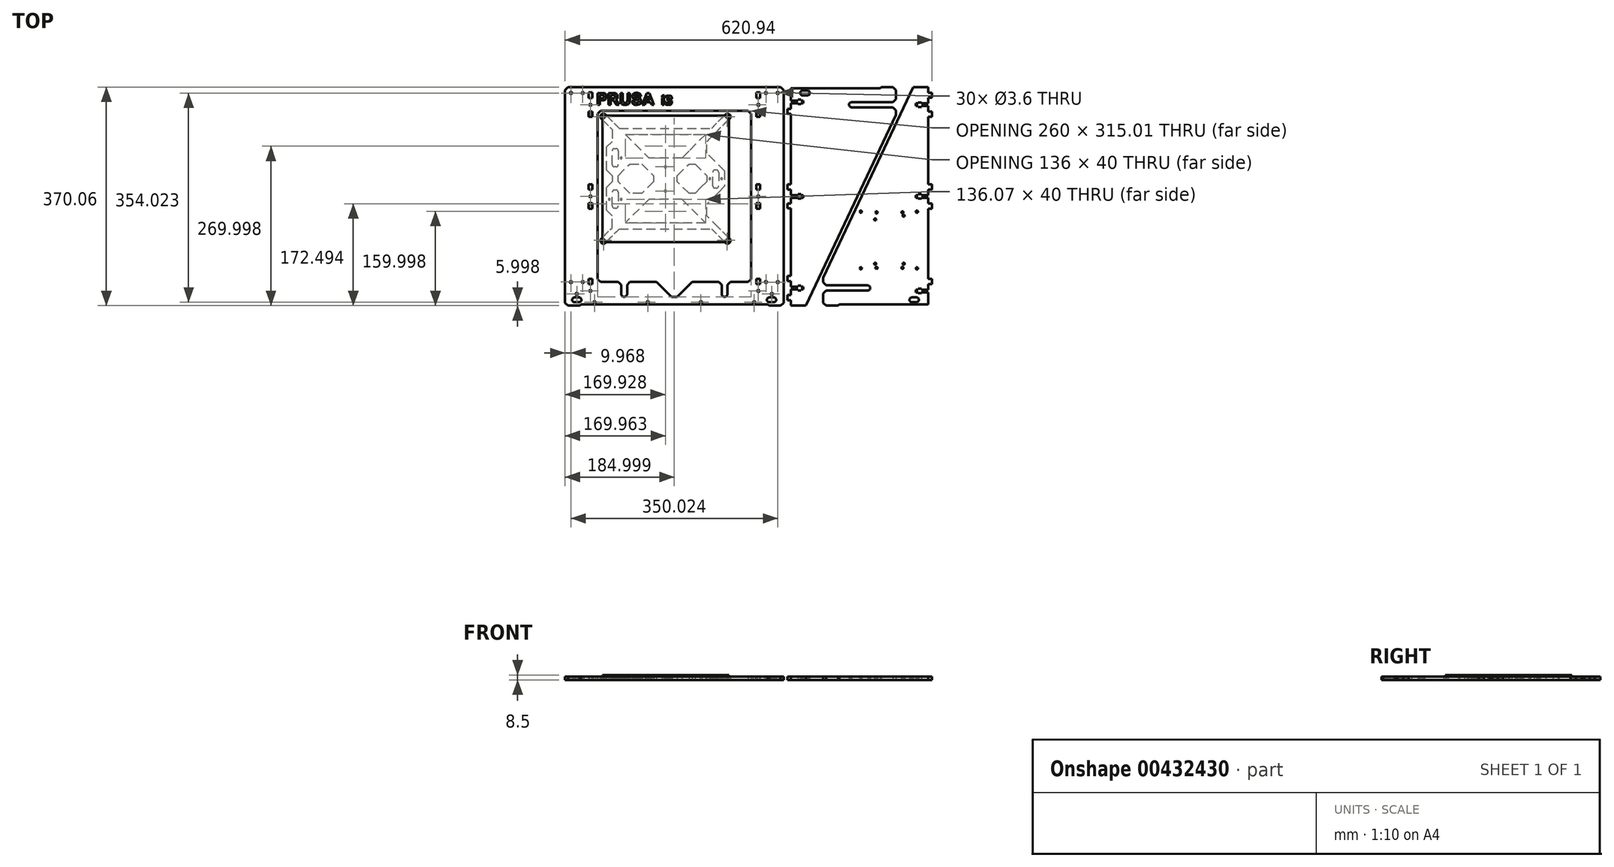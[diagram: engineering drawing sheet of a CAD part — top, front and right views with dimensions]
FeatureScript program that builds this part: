
annotation { "Feature Type Name" : "Feature", "Feature Type Description" : "" }
export const myFeature = defineFeature(function(context is Context, id is Id, definition is map)
    precondition{}
    {
        {
            var Q0;
            Q0=qCreatedBy(makeId("Top.planeOp"),FACE);
            var sketch = newSketch(context, id + "F0", { "sketchPlane" : qUnion([Q0])});
            skLineSegment(sketch, "E0", {"start": v(-112.47, -5.03) * mm, "end": v(-112.54, -5.03) * mm});
            skLineSegment(sketch, "E1", {"start": v(-72.47, -45.03) * mm, "end": v(-72.54, -45.03) * mm});
            skLineSegment(sketch, "E2", {"start": v(-168.47, -5.03) * mm, "end": v(-208.47, -45.03) * mm});
            skLineSegment(sketch, "E3", {"start": v(-112.47, -5.03) * mm, "end": v(-72.47, -45.03) * mm});
            skLineSegment(sketch, "E4", {"start": v(-112.54, -5.03) * mm, "end": v(-72.54, -45.03) * mm});
            skLineSegment(sketch, "E5", {"start": v(-168.54, -5.03) * mm, "end": v(-208.54, -45.03) * mm});
            skLineSegment(sketch, "E6", {"start": v(-208.47, -45.03) * mm, "end": v(-208.54, -45.03) * mm});
            skLineSegment(sketch, "E7", {"start": v(-168.47, -5.03) * mm, "end": v(-168.54, -5.03) * mm});
            skLineSegment(sketch, "E8", {"start": v(-305.47, -185.03) * mm, "end": v(-310.47, -180.22) * mm});
            skLineSegment(sketch, "E9", {"start": v(-310.47, 179.97) * mm, "end": v(-305.47, 184.97) * mm});
            skLineSegment(sketch, "E10", {"start": v(-305.47, 184.97) * mm, "end": v(54.53, 184.97) * mm});
            skLineSegment(sketch, "E11", {"start": v(54.53, 184.97) * mm, "end": v(59.53, 179.97) * mm});
            skLineSegment(sketch, "E12", {"start": v(59.53, -180.03) * mm, "end": v(54.53, -185.03) * mm});
            skLineSegment(sketch, "E13", {"start": v(34.53, -185.03) * mm, "end": v(32.53, -183.03) * mm});
            skLineSegment(sketch, "E14", {"start": v(32.53, -183.03) * mm, "end": v(-283.47, -183.03) * mm});
            skLineSegment(sketch, "E15", {"start": v(-283.47, -183.03) * mm, "end": v(-285.47, -185.03) * mm});
            skLineSegment(sketch, "E16", {"start": v(-230.47, -145.03) * mm, "end": v(-250.47, -145.03) * mm});
            skLineSegment(sketch, "E17", {"start": v(-250.47, -145.03) * mm, "end": v(-255.47, -140.03) * mm});
            skLineSegment(sketch, "E18", {"start": v(-255.47, -140.03) * mm, "end": v(-255.47, 139.97) * mm});
            skLineSegment(sketch, "E19", {"start": v(-255.47, 139.97) * mm, "end": v(-250.47, 144.97) * mm});
            skLineSegment(sketch, "E20", {"start": v(-250.47, 144.97) * mm, "end": v(-0.47, 144.97) * mm});
            skLineSegment(sketch, "E21", {"start": v(-0.47, 144.97) * mm, "end": v(4.53, 139.97) * mm});
            skLineSegment(sketch, "E22", {"start": v(4.53, 139.97) * mm, "end": v(4.53, -140.03) * mm});
            skLineSegment(sketch, "E23", {"start": v(4.53, -140.03) * mm, "end": v(-0.47, -145.03) * mm});
            skLineSegment(sketch, "E24", {"start": v(-0.47, -145.03) * mm, "end": v(-20.47, -145.03) * mm});
            skLineSegment(sketch, "E25", {"start": v(-130.47, -170.03) * mm, "end": v(-120.47, -170.03) * mm});
            skLineSegment(sketch, "E26", {"start": v(-120.47, -170.03) * mm, "end": v(-95.47, -145.03) * mm});
            skLineSegment(sketch, "E27", {"start": v(-130.47, -170.03) * mm, "end": v(-155.47, -145.03) * mm});
            skLineSegment(sketch, "E28", {"start": v(-200.47, -145.03) * mm, "end": v(-155.47, -145.03) * mm});
            skLineSegment(sketch, "E29", {"start": v(-95.47, -145.03) * mm, "end": v(-50.47, -145.03) * mm});
            skLineSegment(sketch, "E30", {"start": v(-80.47, 44.97) * mm, "end": v(-80.47, 44.9) * mm});
            skLineSegment(sketch, "E31", {"start": v(39.53, -179.03) * mm, "end": v(39.8, -179) * mm});
            skLineSegment(sketch, "E32", {"start": v(-310.47, -180.22) * mm, "end": v(-310.47, 179.97) * mm});
            skLineSegment(sketch, "E33", {"start": v(59.53, 179.97) * mm, "end": v(59.53, -180.03) * mm});
            skLineSegment(sketch, "E34", {"start": v(54.53, -185.03) * mm, "end": v(34.53, -185.03) * mm});
            skLineSegment(sketch, "E35", {"start": v(-285.47, -185.03) * mm, "end": v(-305.47, -185.03) * mm});
            skLineSegment(sketch, "E36", {"start": v(31.63, -173) * mm, "end": v(31.23, -173.96) * mm});
            skLineSegment(sketch, "E37", {"start": v(31.1, -175) * mm, "end": v(31.23, -176.03) * mm});
            skLineSegment(sketch, "E38", {"start": v(34.06, -171.13) * mm, "end": v(33.1, -171.53) * mm});
            skLineSegment(sketch, "E39", {"start": v(44.12, -171.13) * mm, "end": v(43.09, -171) * mm});
            skLineSegment(sketch, "E40", {"start": v(45.92, -177.82) * mm, "end": v(46.55, -177) * mm});
            skLineSegment(sketch, "E41", {"start": v(45.09, -178.46) * mm, "end": v(45.92, -177.82) * mm});
            skLineSegment(sketch, "E42", {"start": v(44.12, -178.86) * mm, "end": v(45.09, -178.46) * mm});
            skLineSegment(sketch, "E43", {"start": v(33.1, -178.46) * mm, "end": v(34.06, -178.86) * mm});
            skLineSegment(sketch, "E44", {"start": v(34.06, -178.86) * mm, "end": v(35.1, -179) * mm});
            skLineSegment(sketch, "E45", {"start": v(31.23, -176.03) * mm, "end": v(31.63, -177) * mm});
            skLineSegment(sketch, "E46", {"start": v(45.92, -172.17) * mm, "end": v(45.09, -171.53) * mm});
            skLineSegment(sketch, "E47", {"start": v(46.55, -173) * mm, "end": v(45.92, -172.17) * mm});
            skLineSegment(sketch, "E48", {"start": v(35.1, -171) * mm, "end": v(43.09, -171) * mm});
            skLineSegment(sketch, "E49", {"start": v(33.1, -171.53) * mm, "end": v(32.26, -172.17) * mm});
            skLineSegment(sketch, "E50", {"start": v(32.26, -172.17) * mm, "end": v(31.63, -173) * mm});
            skLineSegment(sketch, "E51", {"start": v(32.26, -177.82) * mm, "end": v(33.1, -178.46) * mm});
            skLineSegment(sketch, "E52", {"start": v(46.95, -173.96) * mm, "end": v(46.55, -173) * mm});
            skLineSegment(sketch, "E53", {"start": v(31.23, -173.96) * mm, "end": v(31.1, -175) * mm});
            skLineSegment(sketch, "E54", {"start": v(31.63, -177) * mm, "end": v(32.26, -177.82) * mm});
            skLineSegment(sketch, "E55", {"start": v(46.95, -176.03) * mm, "end": v(47.09, -175) * mm});
            skLineSegment(sketch, "E56", {"start": v(46.55, -177) * mm, "end": v(46.95, -176.03) * mm});
            skLineSegment(sketch, "E57", {"start": v(35.1, -171) * mm, "end": v(34.06, -171.13) * mm});
            skLineSegment(sketch, "E58", {"start": v(43.16, -179) * mm, "end": v(44.12, -178.86) * mm});
            skLineSegment(sketch, "E59", {"start": v(35.1, -179) * mm, "end": v(39.25, -179) * mm});
            skLineSegment(sketch, "E60", {"start": v(47.09, -175) * mm, "end": v(46.95, -173.96) * mm});
            skLineSegment(sketch, "E61", {"start": v(45.09, -171.53) * mm, "end": v(44.12, -171.13) * mm});
            skLineSegment(sketch, "E62", {"start": v(39.25, -179) * mm, "end": v(39.53, -179.03) * mm});
            skLineSegment(sketch, "E63", {"start": v(39.25, -179) * mm, "end": v(39.8, -179) * mm});
            skLineSegment(sketch, "E64", {"start": v(39.8, -179) * mm, "end": v(43.16, -179) * mm});
            skLineSegment(sketch, "E65", {"start": v(-298.44, -175) * mm, "end": v(-298.3, -176.03) * mm});
            skLineSegment(sketch, "E66", {"start": v(-297.9, -173) * mm, "end": v(-298.3, -173.96) * mm});
            skLineSegment(sketch, "E67", {"start": v(-295.48, -171.13) * mm, "end": v(-296.44, -171.53) * mm});
            skLineSegment(sketch, "E68", {"start": v(-285.41, -171.13) * mm, "end": v(-286.45, -171) * mm});
            skLineSegment(sketch, "E69", {"start": v(-283.62, -177.82) * mm, "end": v(-282.98, -177) * mm});
            skLineSegment(sketch, "E70", {"start": v(-284.45, -178.46) * mm, "end": v(-283.62, -177.82) * mm});
            skLineSegment(sketch, "E71", {"start": v(-285.41, -178.86) * mm, "end": v(-284.45, -178.46) * mm});
            skLineSegment(sketch, "E72", {"start": v(-296.44, -178.46) * mm, "end": v(-295.48, -178.86) * mm});
            skLineSegment(sketch, "E73", {"start": v(-295.48, -178.86) * mm, "end": v(-294.44, -179) * mm});
            skLineSegment(sketch, "E74", {"start": v(-298.3, -176.03) * mm, "end": v(-297.9, -177) * mm});
            skLineSegment(sketch, "E75", {"start": v(-283.62, -172.17) * mm, "end": v(-284.45, -171.53) * mm});
            skLineSegment(sketch, "E76", {"start": v(-282.98, -173) * mm, "end": v(-283.62, -172.17) * mm});
            skLineSegment(sketch, "E77", {"start": v(-294.44, -171) * mm, "end": v(-286.45, -171) * mm});
            skLineSegment(sketch, "E78", {"start": v(-296.44, -171.53) * mm, "end": v(-297.27, -172.17) * mm});
            skLineSegment(sketch, "E79", {"start": v(-297.27, -172.17) * mm, "end": v(-297.9, -173) * mm});
            skLineSegment(sketch, "E80", {"start": v(-297.27, -177.82) * mm, "end": v(-296.44, -178.46) * mm});
            skLineSegment(sketch, "E81", {"start": v(-282.59, -173.96) * mm, "end": v(-282.98, -173) * mm});
            skLineSegment(sketch, "E82", {"start": v(-298.3, -173.96) * mm, "end": v(-298.44, -175) * mm});
            skLineSegment(sketch, "E83", {"start": v(-297.9, -177) * mm, "end": v(-297.27, -177.82) * mm});
            skLineSegment(sketch, "E84", {"start": v(-282.59, -176.03) * mm, "end": v(-282.45, -175) * mm});
            skLineSegment(sketch, "E85", {"start": v(-282.98, -177) * mm, "end": v(-282.59, -176.03) * mm});
            skLineSegment(sketch, "E86", {"start": v(-294.44, -171) * mm, "end": v(-295.48, -171.13) * mm});
            skLineSegment(sketch, "E87", {"start": v(-286.38, -179) * mm, "end": v(-285.41, -178.86) * mm});
            skLineSegment(sketch, "E88", {"start": v(-294.44, -179) * mm, "end": v(-286.38, -179) * mm});
            skLineSegment(sketch, "E89", {"start": v(-282.45, -175) * mm, "end": v(-282.59, -173.96) * mm});
            skLineSegment(sketch, "E90", {"start": v(-284.45, -171.53) * mm, "end": v(-285.41, -171.13) * mm});
            skLineSegment(sketch, "E91", {"start": v(13.28, 166.71) * mm, "end": v(13.28, 175.71) * mm});
            skLineSegment(sketch, "E92", {"start": v(13.28, 175.71) * mm, "end": v(19.78, 175.71) * mm});
            skLineSegment(sketch, "E93", {"start": v(19.78, 175.71) * mm, "end": v(19.78, 166.71) * mm});
            skLineSegment(sketch, "E94", {"start": v(19.78, 166.71) * mm, "end": v(13.28, 166.71) * mm});
            skLineSegment(sketch, "E95", {"start": v(13.28, 134.41) * mm, "end": v(13.28, 143.41) * mm});
            skLineSegment(sketch, "E96", {"start": v(13.28, 143.41) * mm, "end": v(19.78, 143.41) * mm});
            skLineSegment(sketch, "E97", {"start": v(19.78, 143.41) * mm, "end": v(19.78, 134.41) * mm});
            skLineSegment(sketch, "E98", {"start": v(19.78, 134.41) * mm, "end": v(13.28, 134.41) * mm});
            skLineSegment(sketch, "E99", {"start": v(13.28, 11.62) * mm, "end": v(13.28, 20.62) * mm});
            skLineSegment(sketch, "E100", {"start": v(13.28, 20.62) * mm, "end": v(19.78, 20.62) * mm});
            skLineSegment(sketch, "E101", {"start": v(19.78, 20.62) * mm, "end": v(19.78, 11.62) * mm});
            skLineSegment(sketch, "E102", {"start": v(19.78, 11.62) * mm, "end": v(13.28, 11.62) * mm});
            skLineSegment(sketch, "E103", {"start": v(13.28, -20.68) * mm, "end": v(13.28, -11.68) * mm});
            skLineSegment(sketch, "E104", {"start": v(13.28, -11.68) * mm, "end": v(19.78, -11.68) * mm});
            skLineSegment(sketch, "E105", {"start": v(19.78, -11.68) * mm, "end": v(19.78, -20.68) * mm});
            skLineSegment(sketch, "E106", {"start": v(19.78, -20.68) * mm, "end": v(13.28, -20.68) * mm});
            skLineSegment(sketch, "E107", {"start": v(13.28, -148.38) * mm, "end": v(13.28, -139.38) * mm});
            skLineSegment(sketch, "E108", {"start": v(13.28, -139.38) * mm, "end": v(19.78, -139.38) * mm});
            skLineSegment(sketch, "E109", {"start": v(19.78, -139.38) * mm, "end": v(19.78, -148.38) * mm});
            skLineSegment(sketch, "E110", {"start": v(19.78, -148.38) * mm, "end": v(13.28, -148.38) * mm});
            skLineSegment(sketch, "E111", {"start": v(-270.72, 166.71) * mm, "end": v(-270.72, 175.71) * mm});
            skLineSegment(sketch, "E112", {"start": v(-270.72, 175.71) * mm, "end": v(-264.22, 175.71) * mm});
            skLineSegment(sketch, "E113", {"start": v(-264.22, 175.71) * mm, "end": v(-264.22, 166.71) * mm});
            skLineSegment(sketch, "E114", {"start": v(-264.22, 166.71) * mm, "end": v(-270.72, 166.71) * mm});
            skLineSegment(sketch, "E115", {"start": v(-270.72, 134.41) * mm, "end": v(-270.72, 143.41) * mm});
            skLineSegment(sketch, "E116", {"start": v(-270.72, 143.41) * mm, "end": v(-264.22, 143.41) * mm});
            skLineSegment(sketch, "E117", {"start": v(-264.22, 143.41) * mm, "end": v(-264.22, 134.41) * mm});
            skLineSegment(sketch, "E118", {"start": v(-264.22, 134.41) * mm, "end": v(-270.72, 134.41) * mm});
            skLineSegment(sketch, "E119", {"start": v(-270.72, 11.62) * mm, "end": v(-270.72, 20.62) * mm});
            skLineSegment(sketch, "E120", {"start": v(-270.72, 20.62) * mm, "end": v(-264.22, 20.62) * mm});
            skLineSegment(sketch, "E121", {"start": v(-264.22, 20.62) * mm, "end": v(-264.22, 11.62) * mm});
            skLineSegment(sketch, "E122", {"start": v(-264.22, 11.62) * mm, "end": v(-270.72, 11.62) * mm});
            skLineSegment(sketch, "E123", {"start": v(-270.72, -20.68) * mm, "end": v(-270.72, -11.68) * mm});
            skLineSegment(sketch, "E124", {"start": v(-270.72, -11.68) * mm, "end": v(-264.22, -11.68) * mm});
            skLineSegment(sketch, "E125", {"start": v(-264.22, -11.68) * mm, "end": v(-264.22, -20.68) * mm});
            skLineSegment(sketch, "E126", {"start": v(-264.22, -20.68) * mm, "end": v(-270.72, -20.68) * mm});
            skLineSegment(sketch, "E127", {"start": v(-270.72, -148.38) * mm, "end": v(-270.72, -139.38) * mm});
            skLineSegment(sketch, "E128", {"start": v(-270.72, -139.38) * mm, "end": v(-264.22, -139.38) * mm});
            skLineSegment(sketch, "E129", {"start": v(-264.22, -139.38) * mm, "end": v(-264.22, -148.38) * mm});
            skLineSegment(sketch, "E130", {"start": v(-264.22, -148.38) * mm, "end": v(-270.72, -148.38) * mm});
            skLineSegment(sketch, "E131", {"start": v(310.47, 134.51) * mm, "end": v(310.47, 143.31) * mm});
            skLineSegment(sketch, "E132", {"start": v(304.37, -148.28) * mm, "end": v(310.47, -148.28) * mm});
            skLineSegment(sketch, "E133", {"start": v(310.47, -148.28) * mm, "end": v(310.47, -139.48) * mm});
            skLineSegment(sketch, "E134", {"start": v(310.47, -139.48) * mm, "end": v(304.37, -139.48) * mm});
            skLineSegment(sketch, "E135", {"start": v(304.37, -139.48) * mm, "end": v(304.37, -20.58) * mm});
            skLineSegment(sketch, "E136", {"start": v(88.26, 177.03) * mm, "end": v(88.9, 177.86) * mm});
            skLineSegment(sketch, "E137", {"start": v(103.58, 176.07) * mm, "end": v(103.72, 175.03) * mm});
            skLineSegment(sketch, "E138", {"start": v(103.18, 177.03) * mm, "end": v(103.58, 176.07) * mm});
            skLineSegment(sketch, "E139", {"start": v(83.78, 2.23) * mm, "end": v(71.78, 2.23) * mm});
            skLineSegment(sketch, "E140", {"start": v(170.33, 156.17) * mm, "end": v(170.77, 157.23) * mm});
            skLineSegment(sketch, "E141", {"start": v(91.72, 171.03) * mm, "end": v(90.69, 171.17) * mm});
            skLineSegment(sketch, "E142", {"start": v(99.78, 179.03) * mm, "end": v(100.75, 178.9) * mm});
            skLineSegment(sketch, "E143", {"start": v(91.72, 179.03) * mm, "end": v(99.78, 179.03) * mm});
            skLineSegment(sketch, "E144", {"start": v(171.47, 151.92) * mm, "end": v(170.77, 152.83) * mm});
            skLineSegment(sketch, "E145", {"start": v(170.18, 155.03) * mm, "end": v(170.33, 156.17) * mm});
            skLineSegment(sketch, "E146", {"start": v(83.78, -3.97) * mm, "end": v(88.88, -3.97) * mm});
            skLineSegment(sketch, "E147", {"start": v(224.58, 185.03) * mm, "end": v(244.58, 185.03) * mm});
            skLineSegment(sketch, "E148", {"start": v(170.77, 157.23) * mm, "end": v(171.47, 158.14) * mm});
            skLineSegment(sketch, "E149", {"start": v(88.88, 162.24) * mm, "end": v(88.88, 164.04) * mm});
            skLineSegment(sketch, "E150", {"start": v(83.78, 162.24) * mm, "end": v(71.78, 162.24) * mm});
            skLineSegment(sketch, "E151", {"start": v(83.78, 164.04) * mm, "end": v(83.78, 162.24) * mm});
            skLineSegment(sketch, "E152", {"start": v(71.78, 157.84) * mm, "end": v(71.78, 148.28) * mm});
            skLineSegment(sketch, "E153", {"start": v(83.78, -151.05) * mm, "end": v(83.78, -152.85) * mm});
            skLineSegment(sketch, "E154", {"start": v(83.78, -157.25) * mm, "end": v(83.78, -159.05) * mm});
            skLineSegment(sketch, "E155", {"start": v(92.88, -157.25) * mm, "end": v(92.88, -152.85) * mm});
            skLineSegment(sketch, "E156", {"start": v(88.88, -157.25) * mm, "end": v(92.88, -157.25) * mm});
            skLineSegment(sketch, "E157", {"start": v(88.88, -157.25) * mm, "end": v(88.88, -159.05) * mm});
            skLineSegment(sketch, "E158", {"start": v(71.78, -157.25) * mm, "end": v(83.78, -157.25) * mm});
            skLineSegment(sketch, "E159", {"start": v(92.88, -152.85) * mm, "end": v(88.88, -152.85) * mm});
            skLineSegment(sketch, "E160", {"start": v(83.78, -152.85) * mm, "end": v(71.78, -152.85) * mm});
            skLineSegment(sketch, "E161", {"start": v(88.88, -151.05) * mm, "end": v(83.78, -151.05) * mm});
            skLineSegment(sketch, "E162", {"start": v(304.37, -183.03) * mm, "end": v(153.57, -183.03) * mm});
            skLineSegment(sketch, "E163", {"start": v(273.61, -172.2) * mm, "end": v(274.44, -171.57) * mm});
            skLineSegment(sketch, "E164", {"start": v(272.97, -173.03) * mm, "end": v(273.61, -172.2) * mm});
            skLineSegment(sketch, "E165", {"start": v(284.43, -171.03) * mm, "end": v(276.44, -171.03) * mm});
            skLineSegment(sketch, "E166", {"start": v(203.77, -151.22) * mm, "end": v(204.68, -151.92) * mm});
            skLineSegment(sketch, "E167", {"start": v(283.27, -2.23) * mm, "end": v(287.27, -2.23) * mm});
            skLineSegment(sketch, "E168", {"start": v(202.71, -150.78) * mm, "end": v(203.77, -151.22) * mm});
            skLineSegment(sketch, "E169", {"start": v(287.27, -4.03) * mm, "end": v(292.37, -4.03) * mm});
            skLineSegment(sketch, "E170", {"start": v(286.43, -171.57) * mm, "end": v(287.26, -172.2) * mm});
            skLineSegment(sketch, "E171", {"start": v(304.37, -157.84) * mm, "end": v(292.37, -157.84) * mm});
            skLineSegment(sketch, "E172", {"start": v(292.37, -157.84) * mm, "end": v(292.37, -156.04) * mm});
            skLineSegment(sketch, "E173", {"start": v(283.27, -162.24) * mm, "end": v(287.27, -162.24) * mm});
            skLineSegment(sketch, "E174", {"start": v(287.27, -164.04) * mm, "end": v(292.37, -164.04) * mm});
            skLineSegment(sketch, "E175", {"start": v(292.37, -156.04) * mm, "end": v(287.27, -156.04) * mm});
            skLineSegment(sketch, "E176", {"start": v(287.27, -162.24) * mm, "end": v(287.27, -164.04) * mm});
            skLineSegment(sketch, "E177", {"start": v(292.37, -162.24) * mm, "end": v(304.37, -162.24) * mm});
            skLineSegment(sketch, "E178", {"start": v(292.37, -164.04) * mm, "end": v(292.37, -162.24) * mm});
            skLineSegment(sketch, "E179", {"start": v(304.37, -157.84) * mm, "end": v(304.37, -148.28) * mm});
            skLineSegment(sketch, "E180", {"start": v(103.58, 174) * mm, "end": v(103.18, 173.03) * mm});
            skLineSegment(sketch, "E181", {"start": v(273.61, -177.86) * mm, "end": v(272.97, -177.03) * mm});
            skLineSegment(sketch, "E182", {"start": v(274.44, -178.5) * mm, "end": v(273.61, -177.86) * mm});
            skLineSegment(sketch, "E183", {"start": v(275.4, -178.9) * mm, "end": v(274.44, -178.5) * mm});
            skLineSegment(sketch, "E184", {"start": v(304.37, 2.17) * mm, "end": v(292.37, 2.17) * mm});
            skLineSegment(sketch, "E185", {"start": v(286.43, -178.5) * mm, "end": v(285.47, -178.9) * mm});
            skLineSegment(sketch, "E186", {"start": v(285.47, -178.9) * mm, "end": v(284.43, -179.03) * mm});
            skLineSegment(sketch, "E187", {"start": v(288.3, -176.07) * mm, "end": v(287.9, -177.03) * mm});
            skLineSegment(sketch, "E188", {"start": v(203.77, -158.84) * mm, "end": v(202.71, -159.28) * mm});
            skLineSegment(sketch, "E189", {"start": v(71.78, -175.61) * mm, "end": v(71.78, -184.97) * mm});
            skLineSegment(sketch, "E190", {"start": v(65.68, -143.31) * mm, "end": v(71.78, -143.31) * mm});
            skLineSegment(sketch, "E191", {"start": v(71.78, -134.51) * mm, "end": v(65.68, -134.51) * mm});
            skLineSegment(sketch, "E192", {"start": v(65.68, -134.51) * mm, "end": v(65.68, -143.31) * mm});
            skLineSegment(sketch, "E193", {"start": v(71.78, 148.28) * mm, "end": v(65.68, 148.28) * mm});
            skLineSegment(sketch, "E194", {"start": v(65.68, 148.28) * mm, "end": v(65.68, 139.48) * mm});
            skLineSegment(sketch, "E195", {"start": v(65.68, 139.48) * mm, "end": v(71.78, 139.48) * mm});
            skLineSegment(sketch, "E196", {"start": v(71.78, 139.48) * mm, "end": v(71.78, 20.58) * mm});
            skLineSegment(sketch, "E197", {"start": v(83.78, -2.17) * mm, "end": v(83.78, -3.97) * mm});
            skLineSegment(sketch, "E198", {"start": v(244.58, 185.03) * mm, "end": v(249.58, 180.03) * mm});
            skLineSegment(sketch, "E199", {"start": v(222.58, 183.03) * mm, "end": v(224.58, 185.03) * mm});
            skLineSegment(sketch, "E200", {"start": v(87.86, 174) * mm, "end": v(87.72, 175.03) * mm});
            skLineSegment(sketch, "E201", {"start": v(310.47, 20.52) * mm, "end": v(304.37, 20.52) * mm});
            skLineSegment(sketch, "E202", {"start": v(304.37, 20.52) * mm, "end": v(304.37, 134.51) * mm});
            skLineSegment(sketch, "E203", {"start": v(310.47, -11.78) * mm, "end": v(304.37, -11.78) * mm});
            skLineSegment(sketch, "E204", {"start": v(304.37, -20.58) * mm, "end": v(310.47, -20.58) * mm});
            skLineSegment(sketch, "E205", {"start": v(310.47, -20.58) * mm, "end": v(310.47, -11.78) * mm});
            skLineSegment(sketch, "E206", {"start": v(304.37, 11.72) * mm, "end": v(304.37, 2.17) * mm});
            skLineSegment(sketch, "E207", {"start": v(304.37, -2.23) * mm, "end": v(304.37, -11.78) * mm});
            skLineSegment(sketch, "E208", {"start": v(304.37, 166.81) * mm, "end": v(310.47, 166.81) * mm});
            skLineSegment(sketch, "E209", {"start": v(310.47, 166.81) * mm, "end": v(310.47, 175.61) * mm});
            skLineSegment(sketch, "E210", {"start": v(310.47, 175.61) * mm, "end": v(304.37, 175.61) * mm});
            skLineSegment(sketch, "E211", {"start": v(304.37, 175.61) * mm, "end": v(304.37, 184.97) * mm});
            skLineSegment(sketch, "E212", {"start": v(310.47, 143.31) * mm, "end": v(304.37, 143.31) * mm});
            skLineSegment(sketch, "E213", {"start": v(304.37, 134.51) * mm, "end": v(310.47, 134.51) * mm});
            skLineSegment(sketch, "E214", {"start": v(92.88, -2.17) * mm, "end": v(92.88, 2.23) * mm});
            skLineSegment(sketch, "E215", {"start": v(249.58, 138.03) * mm, "end": v(97.18, -184.97) * mm});
            skLineSegment(sketch, "E216", {"start": v(88.88, -2.17) * mm, "end": v(92.88, -2.17) * mm});
            skLineSegment(sketch, "E217", {"start": v(88.88, -2.17) * mm, "end": v(88.88, -3.97) * mm});
            skLineSegment(sketch, "E218", {"start": v(100.75, 171.17) * mm, "end": v(99.72, 171.03) * mm});
            skLineSegment(sketch, "E219", {"start": v(71.78, -184.97) * mm, "end": v(97.18, -184.97) * mm});
            skLineSegment(sketch, "E220", {"start": v(71.78, 2.23) * mm, "end": v(71.78, 11.78) * mm});
            skLineSegment(sketch, "E221", {"start": v(71.78, -166.81) * mm, "end": v(65.68, -166.81) * mm});
            skLineSegment(sketch, "E222", {"start": v(65.68, -166.81) * mm, "end": v(65.68, -175.61) * mm});
            skLineSegment(sketch, "E223", {"start": v(65.68, -175.61) * mm, "end": v(71.78, -175.61) * mm});
            skLineSegment(sketch, "E224", {"start": v(126.57, -180.03) * mm, "end": v(126.57, -164.43) * mm});
            skLineSegment(sketch, "E225", {"start": v(287.9, -173.03) * mm, "end": v(288.3, -174) * mm});
            skLineSegment(sketch, "E226", {"start": v(288.43, -175.03) * mm, "end": v(288.3, -176.07) * mm});
            skLineSegment(sketch, "E227", {"start": v(285.47, -171.17) * mm, "end": v(286.43, -171.57) * mm});
            skLineSegment(sketch, "E228", {"start": v(292.37, -4.03) * mm, "end": v(292.37, -2.23) * mm});
            skLineSegment(sketch, "E229", {"start": v(83.78, -159.05) * mm, "end": v(88.88, -159.05) * mm});
            skLineSegment(sketch, "E230", {"start": v(88.88, -152.85) * mm, "end": v(88.88, -151.05) * mm});
            skLineSegment(sketch, "E231", {"start": v(71.78, -157.25) * mm, "end": v(71.78, -166.81) * mm});
            skLineSegment(sketch, "E232", {"start": v(71.78, -152.85) * mm, "end": v(71.78, -143.31) * mm});
            skLineSegment(sketch, "E233", {"start": v(92.88, 157.84) * mm, "end": v(92.88, 162.24) * mm});
            skLineSegment(sketch, "E234", {"start": v(88.88, 157.84) * mm, "end": v(92.88, 157.84) * mm});
            skLineSegment(sketch, "E235", {"start": v(88.88, 157.84) * mm, "end": v(88.88, 156.04) * mm});
            skLineSegment(sketch, "E236", {"start": v(71.78, 157.84) * mm, "end": v(83.78, 157.84) * mm});
            skLineSegment(sketch, "E237", {"start": v(83.78, 157.84) * mm, "end": v(83.78, 156.04) * mm});
            skLineSegment(sketch, "E238", {"start": v(92.88, 162.24) * mm, "end": v(88.88, 162.24) * mm});
            skLineSegment(sketch, "E239", {"start": v(174.58, 150.63) * mm, "end": v(173.45, 150.78) * mm});
            skLineSegment(sketch, "E240", {"start": v(102.55, 177.86) * mm, "end": v(103.18, 177.03) * mm});
            skLineSegment(sketch, "E241", {"start": v(101.72, 178.5) * mm, "end": v(102.55, 177.86) * mm});
            skLineSegment(sketch, "E242", {"start": v(100.75, 178.9) * mm, "end": v(101.72, 178.5) * mm});
            skLineSegment(sketch, "E243", {"start": v(71.78, -2.17) * mm, "end": v(83.78, -2.17) * mm});
            skLineSegment(sketch, "E244", {"start": v(89.72, 178.5) * mm, "end": v(90.69, 178.9) * mm});
            skLineSegment(sketch, "E245", {"start": v(90.69, 178.9) * mm, "end": v(91.72, 179.03) * mm});
            skLineSegment(sketch, "E246", {"start": v(87.86, 176.07) * mm, "end": v(88.26, 177.03) * mm});
            skLineSegment(sketch, "E247", {"start": v(172.38, 158.84) * mm, "end": v(173.45, 159.28) * mm});
            skLineSegment(sketch, "E248", {"start": v(283.27, 2.17) * mm, "end": v(283.27, -2.23) * mm});
            skLineSegment(sketch, "E249", {"start": v(126.57, -138.03) * mm, "end": v(278.97, 184.97) * mm});
            skLineSegment(sketch, "E250", {"start": v(287.27, 2.17) * mm, "end": v(283.27, 2.17) * mm});
            skLineSegment(sketch, "E251", {"start": v(287.27, 2.17) * mm, "end": v(287.27, 3.97) * mm});
            skLineSegment(sketch, "E252", {"start": v(275.4, -171.17) * mm, "end": v(276.44, -171.03) * mm});
            skLineSegment(sketch, "E253", {"start": v(304.37, 184.97) * mm, "end": v(278.97, 184.97) * mm});
            skLineSegment(sketch, "E254", {"start": v(201.57, -150.63) * mm, "end": v(202.71, -150.78) * mm});
            skLineSegment(sketch, "E255", {"start": v(272.97, -177.03) * mm, "end": v(272.57, -176.07) * mm});
            skLineSegment(sketch, "E256", {"start": v(292.37, -2.23) * mm, "end": v(304.37, -2.23) * mm});
            skLineSegment(sketch, "E257", {"start": v(205.82, -156.17) * mm, "end": v(205.38, -157.23) * mm});
            skLineSegment(sketch, "E258", {"start": v(284.43, -171.03) * mm, "end": v(285.47, -171.17) * mm});
            skLineSegment(sketch, "E259", {"start": v(276.37, -179.03) * mm, "end": v(275.4, -178.9) * mm});
            skLineSegment(sketch, "E260", {"start": v(284.43, -179.03) * mm, "end": v(276.37, -179.03) * mm});
            skLineSegment(sketch, "E261", {"start": v(204.68, -151.92) * mm, "end": v(205.38, -152.83) * mm});
            skLineSegment(sketch, "E262", {"start": v(205.97, -155.03) * mm, "end": v(205.82, -156.17) * mm});
            skLineSegment(sketch, "E263", {"start": v(292.37, 3.97) * mm, "end": v(287.27, 3.97) * mm});
            skLineSegment(sketch, "E264", {"start": v(151.57, -185.03) * mm, "end": v(131.57, -185.03) * mm});
            skLineSegment(sketch, "E265", {"start": v(205.38, -157.23) * mm, "end": v(204.68, -158.14) * mm});
            skLineSegment(sketch, "E266", {"start": v(287.27, -2.23) * mm, "end": v(287.27, -4.03) * mm});
            skLineSegment(sketch, "E267", {"start": v(283.27, 157.25) * mm, "end": v(283.27, 152.85) * mm});
            skLineSegment(sketch, "E268", {"start": v(287.27, 157.25) * mm, "end": v(283.27, 157.25) * mm});
            skLineSegment(sketch, "E269", {"start": v(287.27, 157.25) * mm, "end": v(287.27, 159.05) * mm});
            skLineSegment(sketch, "E270", {"start": v(304.37, 157.25) * mm, "end": v(292.37, 157.25) * mm});
            skLineSegment(sketch, "E271", {"start": v(283.27, 152.85) * mm, "end": v(287.27, 152.85) * mm});
            skLineSegment(sketch, "E272", {"start": v(292.37, 152.85) * mm, "end": v(304.37, 152.85) * mm});
            skLineSegment(sketch, "E273", {"start": v(287.27, 151.05) * mm, "end": v(292.37, 151.05) * mm});
            skLineSegment(sketch, "E274", {"start": v(292.37, 159.05) * mm, "end": v(287.27, 159.05) * mm});
            skLineSegment(sketch, "E275", {"start": v(287.27, 152.85) * mm, "end": v(287.27, 151.05) * mm});
            skLineSegment(sketch, "E276", {"start": v(304.37, 157.25) * mm, "end": v(304.37, 166.81) * mm});
            skLineSegment(sketch, "E277", {"start": v(304.37, 152.85) * mm, "end": v(304.37, 143.31) * mm});
            skLineSegment(sketch, "E278", {"start": v(283.27, -157.84) * mm, "end": v(283.27, -162.24) * mm});
            skLineSegment(sketch, "E279", {"start": v(287.27, -157.84) * mm, "end": v(283.27, -157.84) * mm});
            skLineSegment(sketch, "E280", {"start": v(287.27, -157.84) * mm, "end": v(287.27, -156.04) * mm});
            skLineSegment(sketch, "E281", {"start": v(292.37, 151.05) * mm, "end": v(292.37, 152.85) * mm});
            skLineSegment(sketch, "E282", {"start": v(292.37, 157.25) * mm, "end": v(292.37, 159.05) * mm});
            skLineSegment(sketch, "E283", {"start": v(88.88, 2.23) * mm, "end": v(88.88, 4.03) * mm});
            skLineSegment(sketch, "E284", {"start": v(171.47, 158.14) * mm, "end": v(172.38, 158.84) * mm});
            skLineSegment(sketch, "E285", {"start": v(103.72, 175.03) * mm, "end": v(103.58, 174) * mm});
            skLineSegment(sketch, "E286", {"start": v(101.72, 171.57) * mm, "end": v(100.75, 171.17) * mm});
            skLineSegment(sketch, "E287", {"start": v(244.58, 159.43) * mm, "end": v(174.58, 159.43) * mm});
            skLineSegment(sketch, "E288", {"start": v(244.58, 159.43) * mm, "end": v(249.58, 164.43) * mm});
            skLineSegment(sketch, "E289", {"start": v(244.58, 150.63) * mm, "end": v(174.58, 150.63) * mm});
            skLineSegment(sketch, "E290", {"start": v(249.58, 145.63) * mm, "end": v(249.58, 138.03) * mm});
            skLineSegment(sketch, "E291", {"start": v(244.58, 150.63) * mm, "end": v(249.58, 145.63) * mm});
            skLineSegment(sketch, "E292", {"start": v(71.78, -11.72) * mm, "end": v(65.68, -11.72) * mm});
            skLineSegment(sketch, "E293", {"start": v(65.68, -11.72) * mm, "end": v(65.68, -20.52) * mm});
            skLineSegment(sketch, "E294", {"start": v(65.68, -20.52) * mm, "end": v(71.78, -20.52) * mm});
            skLineSegment(sketch, "E295", {"start": v(71.78, -20.52) * mm, "end": v(71.78, -134.51) * mm});
            skLineSegment(sketch, "E296", {"start": v(65.68, 11.78) * mm, "end": v(71.78, 11.78) * mm});
            skLineSegment(sketch, "E297", {"start": v(71.78, 20.58) * mm, "end": v(65.68, 20.58) * mm});
            skLineSegment(sketch, "E298", {"start": v(65.68, 20.58) * mm, "end": v(65.68, 11.78) * mm});
            skLineSegment(sketch, "E299", {"start": v(71.78, -11.72) * mm, "end": v(71.78, -2.17) * mm});
            skLineSegment(sketch, "E300", {"start": v(88.88, 164.04) * mm, "end": v(83.78, 164.04) * mm});
            skLineSegment(sketch, "E301", {"start": v(91.72, 171.03) * mm, "end": v(99.72, 171.03) * mm});
            skLineSegment(sketch, "E302", {"start": v(172.38, 151.22) * mm, "end": v(171.47, 151.92) * mm});
            skLineSegment(sketch, "E303", {"start": v(92.88, 2.23) * mm, "end": v(88.88, 2.23) * mm});
            skLineSegment(sketch, "E304", {"start": v(173.45, 150.78) * mm, "end": v(172.38, 151.22) * mm});
            skLineSegment(sketch, "E305", {"start": v(88.88, 4.03) * mm, "end": v(83.78, 4.03) * mm});
            skLineSegment(sketch, "E306", {"start": v(83.78, 156.04) * mm, "end": v(88.88, 156.04) * mm});
            skLineSegment(sketch, "E307", {"start": v(89.72, 171.57) * mm, "end": v(88.9, 172.2) * mm});
            skLineSegment(sketch, "E308", {"start": v(88.9, 172.2) * mm, "end": v(88.26, 173.03) * mm});
            skLineSegment(sketch, "E309", {"start": v(88.9, 177.86) * mm, "end": v(89.72, 178.5) * mm});
            skLineSegment(sketch, "E310", {"start": v(170.77, 152.83) * mm, "end": v(170.33, 153.9) * mm});
            skLineSegment(sketch, "E311", {"start": v(170.33, 153.9) * mm, "end": v(170.18, 155.03) * mm});
            skLineSegment(sketch, "E312", {"start": v(71.78, 183.03) * mm, "end": v(71.78, 162.24) * mm});
            skLineSegment(sketch, "E313", {"start": v(173.45, 159.28) * mm, "end": v(174.58, 159.43) * mm});
            skLineSegment(sketch, "E314", {"start": v(249.58, 180.03) * mm, "end": v(249.58, 164.43) * mm});
            skLineSegment(sketch, "E315", {"start": v(88.26, 173.03) * mm, "end": v(87.86, 174) * mm});
            skLineSegment(sketch, "E316", {"start": v(87.72, 175.03) * mm, "end": v(87.86, 176.07) * mm});
            skLineSegment(sketch, "E317", {"start": v(90.69, 171.17) * mm, "end": v(89.72, 171.57) * mm});
            skLineSegment(sketch, "E318", {"start": v(83.78, 4.03) * mm, "end": v(83.78, 2.23) * mm});
            skLineSegment(sketch, "E319", {"start": v(204.68, -158.14) * mm, "end": v(203.77, -158.84) * mm});
            skLineSegment(sketch, "E320", {"start": v(272.44, -175.03) * mm, "end": v(272.57, -174) * mm});
            skLineSegment(sketch, "E321", {"start": v(274.44, -171.57) * mm, "end": v(275.4, -171.17) * mm});
            skLineSegment(sketch, "E322", {"start": v(131.57, -159.43) * mm, "end": v(201.57, -159.43) * mm});
            skLineSegment(sketch, "E323", {"start": v(131.57, -159.43) * mm, "end": v(126.57, -164.43) * mm});
            skLineSegment(sketch, "E324", {"start": v(131.57, -150.63) * mm, "end": v(201.57, -150.63) * mm});
            skLineSegment(sketch, "E325", {"start": v(126.57, -145.63) * mm, "end": v(126.57, -138.03) * mm});
            skLineSegment(sketch, "E326", {"start": v(131.57, -150.63) * mm, "end": v(126.57, -145.63) * mm});
            skLineSegment(sketch, "E327", {"start": v(304.37, 11.72) * mm, "end": v(310.47, 11.72) * mm});
            skLineSegment(sketch, "E328", {"start": v(310.47, 11.72) * mm, "end": v(310.47, 20.52) * mm});
            skLineSegment(sketch, "E329", {"start": v(287.26, -172.2) * mm, "end": v(287.9, -173.03) * mm});
            skLineSegment(sketch, "E330", {"start": v(287.26, -177.86) * mm, "end": v(286.43, -178.5) * mm});
            skLineSegment(sketch, "E331", {"start": v(205.38, -152.83) * mm, "end": v(205.82, -153.9) * mm});
            skLineSegment(sketch, "E332", {"start": v(205.82, -153.9) * mm, "end": v(205.97, -155.03) * mm});
            skLineSegment(sketch, "E333", {"start": v(272.57, -174) * mm, "end": v(272.97, -173.03) * mm});
            skLineSegment(sketch, "E334", {"start": v(292.37, 2.17) * mm, "end": v(292.37, 3.97) * mm});
            skLineSegment(sketch, "E335", {"start": v(131.57, -185.03) * mm, "end": v(126.57, -180.03) * mm});
            skLineSegment(sketch, "E336", {"start": v(153.57, -183.03) * mm, "end": v(151.57, -185.03) * mm});
            skLineSegment(sketch, "E337", {"start": v(288.3, -174) * mm, "end": v(288.43, -175.03) * mm});
            skLineSegment(sketch, "E338", {"start": v(287.9, -177.03) * mm, "end": v(287.26, -177.86) * mm});
            skLineSegment(sketch, "E339", {"start": v(272.57, -176.07) * mm, "end": v(272.44, -175.03) * mm});
            skLineSegment(sketch, "E340", {"start": v(304.37, -183.03) * mm, "end": v(304.37, -162.24) * mm});
            skLineSegment(sketch, "E341", {"start": v(202.71, -159.28) * mm, "end": v(201.57, -159.43) * mm});
            skLineSegment(sketch, "E342", {"start": v(71.78, 183.03) * mm, "end": v(222.58, 183.03) * mm});
            skLineSegment(sketch, "E343", {"start": v(102.55, 172.2) * mm, "end": v(101.72, 171.57) * mm});
            skLineSegment(sketch, "E344", {"start": v(103.18, 173.03) * mm, "end": v(102.55, 172.2) * mm});
            skLineSegment(sketch, "E345", {"start": v(188.2, -26.36) * mm, "end": v(188.15, -25.9) * mm});
            skLineSegment(sketch, "E346", {"start": v(286.7, -121.34) * mm, "end": v(286.76, -121.8) * mm});
            skLineSegment(sketch, "E347", {"start": v(286.52, -120.9) * mm, "end": v(286.7, -121.34) * mm});
            skLineSegment(sketch, "E348", {"start": v(286.24, -120.54) * mm, "end": v(286.52, -120.9) * mm});
            skLineSegment(sketch, "E349", {"start": v(191.68, -26.36) * mm, "end": v(191.5, -26.8) * mm});
            skLineSegment(sketch, "E350", {"start": v(191.24, -123.04) * mm, "end": v(190.87, -123.33) * mm});
            skLineSegment(sketch, "E351", {"start": v(191.53, -122.67) * mm, "end": v(191.24, -123.04) * mm});
            skLineSegment(sketch, "E352", {"start": v(189.07, -123.32) * mm, "end": v(188.7, -123.04) * mm});
            skLineSegment(sketch, "E353", {"start": v(188.41, -122.67) * mm, "end": v(188.23, -122.23) * mm});
            skLineSegment(sketch, "E354", {"start": v(189.5, -120.03) * mm, "end": v(189.9, -119.98) * mm});
            skLineSegment(sketch, "E355", {"start": v(286.74, -25.85) * mm, "end": v(286.68, -26.32) * mm});
            skLineSegment(sketch, "E356", {"start": v(285.4, -27.6) * mm, "end": v(284.94, -27.65) * mm});
            skLineSegment(sketch, "E357", {"start": v(188.39, -25) * mm, "end": v(188.67, -24.63) * mm});
            skLineSegment(sketch, "E358", {"start": v(189.9, -27.7) * mm, "end": v(189.48, -27.64) * mm});
            skLineSegment(sketch, "E359", {"start": v(284.04, -27.41) * mm, "end": v(283.67, -27.13) * mm});
            skLineSegment(sketch, "E360", {"start": v(283.17, -121.84) * mm, "end": v(283.16, -121.8) * mm});
            skLineSegment(sketch, "E361", {"start": v(189.48, -24.16) * mm, "end": v(189.95, -24.1) * mm});
            skLineSegment(sketch, "E362", {"start": v(284.06, -123.37) * mm, "end": v(283.69, -123.08) * mm});
            skLineSegment(sketch, "E363", {"start": v(213.85, -37.27) * mm, "end": v(214.31, -37.2) * mm});
            skLineSegment(sketch, "E364", {"start": v(212.75, -38.1) * mm, "end": v(213.04, -37.74) * mm});
            skLineSegment(sketch, "E365", {"start": v(189.04, -27.46) * mm, "end": v(188.67, -27.17) * mm});
            skLineSegment(sketch, "E366", {"start": v(216.08, -114.42) * mm, "end": v(215.9, -114.85) * mm});
            skLineSegment(sketch, "E367", {"start": v(215.9, -114.85) * mm, "end": v(215.62, -115.23) * mm});
            skLineSegment(sketch, "E368", {"start": v(190.41, -24.16) * mm, "end": v(190.85, -24.34) * mm});
            skLineSegment(sketch, "E369", {"start": v(285.43, -120.07) * mm, "end": v(285.86, -120.25) * mm});
            skLineSegment(sketch, "E370", {"start": v(283.69, -120.54) * mm, "end": v(284.06, -120.25) * mm});
            skLineSegment(sketch, "E371", {"start": v(283.4, -120.9) * mm, "end": v(283.69, -120.54) * mm});
            skLineSegment(sketch, "E372", {"start": v(283.22, -121.34) * mm, "end": v(283.4, -120.9) * mm});
            skLineSegment(sketch, "E373", {"start": v(189.95, -24.1) * mm, "end": v(190.41, -24.16) * mm});
            skLineSegment(sketch, "E374", {"start": v(213.07, -115.23) * mm, "end": v(212.79, -114.85) * mm});
            skLineSegment(sketch, "E375", {"start": v(212.79, -114.85) * mm, "end": v(212.6, -114.42) * mm});
            skLineSegment(sketch, "E376", {"start": v(263.48, -34.27) * mm, "end": v(263.04, -34.45) * mm});
            skLineSegment(sketch, "E377", {"start": v(259.04, -108.12) * mm, "end": v(259.04, -110.32) * mm});
            skLineSegment(sketch, "E378", {"start": v(259.04, -110.32) * mm, "end": v(258.74, -110.32) * mm});
            skLineSegment(sketch, "E379", {"start": v(259.04, -110.32) * mm, "end": v(259.36, -110.32) * mm});
            skLineSegment(sketch, "E380", {"start": v(188.23, -122.23) * mm, "end": v(188.17, -121.77) * mm});
            skLineSegment(sketch, "E381", {"start": v(189.07, -120.2) * mm, "end": v(189.5, -120.03) * mm});
            skLineSegment(sketch, "E382", {"start": v(261.02, -33.6) * mm, "end": v(260.84, -33.17) * mm});
            skLineSegment(sketch, "E383", {"start": v(262.11, -30.97) * mm, "end": v(262.58, -30.9) * mm});
            skLineSegment(sketch, "E384", {"start": v(263.48, -31.15) * mm, "end": v(263.62, -31.26) * mm});
            skLineSegment(sketch, "E385", {"start": v(264.14, -31.8) * mm, "end": v(264.32, -32.24) * mm});
            skLineSegment(sketch, "E386", {"start": v(286.76, -121.8) * mm, "end": v(286.7, -122.28) * mm});
            skLineSegment(sketch, "E387", {"start": v(190.41, -27.64) * mm, "end": v(189.94, -27.7) * mm});
            skLineSegment(sketch, "E388", {"start": v(189.94, -27.7) * mm, "end": v(189.9, -27.7) * mm});
            skLineSegment(sketch, "E389", {"start": v(191.48, -31.81) * mm, "end": v(192.63, -31.81) * mm});
            skLineSegment(sketch, "E390", {"start": v(191.48, -31.81) * mm, "end": v(191.48, -30.71) * mm});
            skLineSegment(sketch, "E391", {"start": v(262.11, -34.45) * mm, "end": v(261.75, -34.3) * mm});
            skLineSegment(sketch, "E392", {"start": v(216.05, -38.54) * mm, "end": v(216.11, -39) * mm});
            skLineSegment(sketch, "E393", {"start": v(213.04, -37.74) * mm, "end": v(213.41, -37.45) * mm});
            skLineSegment(sketch, "E394", {"start": v(213.41, -37.45) * mm, "end": v(213.85, -37.27) * mm});
            skLineSegment(sketch, "E395", {"start": v(190.44, -120.03) * mm, "end": v(190.87, -120.2) * mm});
            skLineSegment(sketch, "E396", {"start": v(189.97, -119.97) * mm, "end": v(190.44, -120.03) * mm});
            skLineSegment(sketch, "E397", {"start": v(284.96, -120) * mm, "end": v(285.43, -120.07) * mm});
            skLineSegment(sketch, "E398", {"start": v(283.22, -122.28) * mm, "end": v(283.17, -121.84) * mm});
            skLineSegment(sketch, "E399", {"start": v(215.87, -39.9) * mm, "end": v(215.59, -40.28) * mm});
            skLineSegment(sketch, "E400", {"start": v(214.78, -40.75) * mm, "end": v(214.31, -40.8) * mm});
            skLineSegment(sketch, "E401", {"start": v(259.18, -36) * mm, "end": v(258.88, -36.3) * mm});
            skLineSegment(sketch, "E402", {"start": v(216.99, -42.2) * mm, "end": v(216.69, -42.51) * mm});
            skLineSegment(sketch, "E403", {"start": v(216.99, -44.4) * mm, "end": v(217.3, -44.4) * mm});
            skLineSegment(sketch, "E404", {"start": v(216.99, -44.4) * mm, "end": v(216.69, -44.4) * mm});
            skLineSegment(sketch, "E405", {"start": v(283.16, -121.8) * mm, "end": v(283.22, -121.34) * mm});
            skLineSegment(sketch, "E406", {"start": v(284.5, -123.55) * mm, "end": v(284.06, -123.37) * mm});
            skLineSegment(sketch, "E407", {"start": v(283.2, -25.39) * mm, "end": v(283.38, -24.95) * mm});
            skLineSegment(sketch, "E408", {"start": v(191.75, -25.9) * mm, "end": v(191.68, -26.36) * mm});
            skLineSegment(sketch, "E409", {"start": v(261.3, -31.44) * mm, "end": v(261.68, -31.15) * mm});
            skLineSegment(sketch, "E410", {"start": v(261.02, -31.8) * mm, "end": v(261.3, -31.44) * mm});
            skLineSegment(sketch, "E411", {"start": v(188.2, -25.43) * mm, "end": v(188.39, -25) * mm});
            skLineSegment(sketch, "E412", {"start": v(260.84, -33.17) * mm, "end": v(260.78, -32.7) * mm});
            skLineSegment(sketch, "E413", {"start": v(193.58, -116.54) * mm, "end": v(194.73, -116.54) * mm});
            skLineSegment(sketch, "E414", {"start": v(193.58, -117.64) * mm, "end": v(194.73, -117.64) * mm});
            skLineSegment(sketch, "E415", {"start": v(194.73, -115.44) * mm, "end": v(193.58, -115.44) * mm});
            skLineSegment(sketch, "E416", {"start": v(193.58, -117.64) * mm, "end": v(193.58, -116.54) * mm});
            skLineSegment(sketch, "E417", {"start": v(282.06, -116.37) * mm, "end": v(282.06, -115.27) * mm});
            skLineSegment(sketch, "E418", {"start": v(280.9, -116.37) * mm, "end": v(282.06, -116.37) * mm});
            skLineSegment(sketch, "E419", {"start": v(280.9, -117.47) * mm, "end": v(280.9, -116.37) * mm});
            skLineSegment(sketch, "E420", {"start": v(191.76, -121.84) * mm, "end": v(191.7, -122.23) * mm});
            skLineSegment(sketch, "E421", {"start": v(283.38, -26.75) * mm, "end": v(283.2, -26.32) * mm});
            skLineSegment(sketch, "E422", {"start": v(191.22, -27.17) * mm, "end": v(190.84, -27.46) * mm});
            skLineSegment(sketch, "E423", {"start": v(264.31, -33.17) * mm, "end": v(264.13, -33.6) * mm});
            skLineSegment(sketch, "E424", {"start": v(285.86, -123.37) * mm, "end": v(285.43, -123.55) * mm});
            skLineSegment(sketch, "E425", {"start": v(286.24, -123.08) * mm, "end": v(285.86, -123.37) * mm});
            skLineSegment(sketch, "E426", {"start": v(286.52, -122.7) * mm, "end": v(286.24, -123.08) * mm});
            skLineSegment(sketch, "E427", {"start": v(286.7, -122.28) * mm, "end": v(286.52, -122.7) * mm});
            skLineSegment(sketch, "E428", {"start": v(264.13, -33.6) * mm, "end": v(263.85, -33.98) * mm});
            skLineSegment(sketch, "E429", {"start": v(263.04, -34.45) * mm, "end": v(262.58, -34.5) * mm});
            skLineSegment(sketch, "E430", {"start": v(212.6, -114.42) * mm, "end": v(212.55, -113.95) * mm});
            skLineSegment(sketch, "E431", {"start": v(215.9, -113.05) * mm, "end": v(216.08, -113.49) * mm});
            skLineSegment(sketch, "E432", {"start": v(261.68, -31.15) * mm, "end": v(262.11, -30.97) * mm});
            skLineSegment(sketch, "E433", {"start": v(261.68, -34.27) * mm, "end": v(261.53, -34.13) * mm});
            skLineSegment(sketch, "E434", {"start": v(285.84, -27.41) * mm, "end": v(285.4, -27.6) * mm});
            skLineSegment(sketch, "E435", {"start": v(286.68, -26.32) * mm, "end": v(286.5, -26.75) * mm});
            skLineSegment(sketch, "E436", {"start": v(283.38, -24.95) * mm, "end": v(283.67, -24.58) * mm});
            skLineSegment(sketch, "E437", {"start": v(280.9, -117.47) * mm, "end": v(282.06, -117.47) * mm});
            skLineSegment(sketch, "E438", {"start": v(282.06, -115.27) * mm, "end": v(280.9, -115.27) * mm});
            skLineSegment(sketch, "E439", {"start": v(259.18, -38.2) * mm, "end": v(259.5, -38.2) * mm});
            skLineSegment(sketch, "E440", {"start": v(259.18, -38.2) * mm, "end": v(258.88, -38.2) * mm});
            skLineSegment(sketch, "E441", {"start": v(259.18, -36) * mm, "end": v(259.18, -38.2) * mm});
            skLineSegment(sketch, "E442", {"start": v(215.25, -112.4) * mm, "end": v(215.36, -112.48) * mm});
            skLineSegment(sketch, "E443", {"start": v(190.84, -27.46) * mm, "end": v(190.41, -27.64) * mm});
            skLineSegment(sketch, "E444", {"start": v(188.39, -26.8) * mm, "end": v(188.2, -26.36) * mm});
            skLineSegment(sketch, "E445", {"start": v(190.87, -120.2) * mm, "end": v(191.24, -120.5) * mm});
            skLineSegment(sketch, "E446", {"start": v(218.12, -110.06) * mm, "end": v(218.44, -110.06) * mm});
            skLineSegment(sketch, "E447", {"start": v(218.12, -107.86) * mm, "end": v(217.82, -108.17) * mm});
            skLineSegment(sketch, "E448", {"start": v(218.12, -110.06) * mm, "end": v(217.82, -110.06) * mm});
            skLineSegment(sketch, "E449", {"start": v(218.12, -107.86) * mm, "end": v(218.12, -110.06) * mm});
            skLineSegment(sketch, "E450", {"start": v(259.04, -108.12) * mm, "end": v(258.74, -108.43) * mm});
            skLineSegment(sketch, "E451", {"start": v(263.04, -30.97) * mm, "end": v(263.48, -31.15) * mm});
            skLineSegment(sketch, "E452", {"start": v(283.4, -122.7) * mm, "end": v(283.22, -122.28) * mm});
            skLineSegment(sketch, "E453", {"start": v(284.5, -120.07) * mm, "end": v(284.9, -120.02) * mm});
            skLineSegment(sketch, "E454", {"start": v(212.57, -39.47) * mm, "end": v(212.51, -39) * mm});
            skLineSegment(sketch, "E455", {"start": v(261.7, -112.47) * mm, "end": v(262.14, -112.29) * mm});
            skLineSegment(sketch, "E456", {"start": v(260.87, -114.5) * mm, "end": v(260.8, -114.02) * mm});
            skLineSegment(sketch, "E457", {"start": v(213.07, -112.68) * mm, "end": v(213.45, -112.4) * mm});
            skLineSegment(sketch, "E458", {"start": v(214.31, -40.8) * mm, "end": v(213.85, -40.75) * mm});
            skLineSegment(sketch, "E459", {"start": v(213.85, -40.75) * mm, "end": v(213.46, -40.59) * mm});
            skLineSegment(sketch, "E460", {"start": v(264.32, -32.24) * mm, "end": v(264.38, -32.7) * mm});
            skLineSegment(sketch, "E461", {"start": v(262.14, -115.76) * mm, "end": v(261.96, -115.67) * mm});
            skLineSegment(sketch, "E462", {"start": v(261.7, -115.58) * mm, "end": v(261.33, -115.3) * mm});
            skLineSegment(sketch, "E463", {"start": v(261.33, -115.3) * mm, "end": v(261.05, -114.92) * mm});
            skLineSegment(sketch, "E464", {"start": v(190.85, -24.34) * mm, "end": v(191.22, -24.63) * mm});
            skLineSegment(sketch, "E465", {"start": v(191.22, -24.63) * mm, "end": v(191.5, -25) * mm});
            skLineSegment(sketch, "E466", {"start": v(213.41, -40.57) * mm, "end": v(213.3, -40.47) * mm});
            skLineSegment(sketch, "E467", {"start": v(213.04, -40.28) * mm, "end": v(212.75, -39.9) * mm});
            skLineSegment(sketch, "E468", {"start": v(212.75, -39.9) * mm, "end": v(212.57, -39.47) * mm});
            skLineSegment(sketch, "E469", {"start": v(190.87, -123.33) * mm, "end": v(190.44, -123.5) * mm});
            skLineSegment(sketch, "E470", {"start": v(190.44, -123.5) * mm, "end": v(189.97, -123.57) * mm});
            skLineSegment(sketch, "E471", {"start": v(189.97, -123.57) * mm, "end": v(189.5, -123.5) * mm});
            skLineSegment(sketch, "E472", {"start": v(284.06, -120.25) * mm, "end": v(284.5, -120.07) * mm});
            skLineSegment(sketch, "E473", {"start": v(188.17, -121.77) * mm, "end": v(188.23, -121.3) * mm});
            skLineSegment(sketch, "E474", {"start": v(189.5, -123.5) * mm, "end": v(189.07, -123.32) * mm});
            skLineSegment(sketch, "E475", {"start": v(189.9, -119.98) * mm, "end": v(189.97, -119.97) * mm});
            skLineSegment(sketch, "E476", {"start": v(284.96, -123.6) * mm, "end": v(284.5, -123.55) * mm});
            skLineSegment(sketch, "E477", {"start": v(188.15, -25.9) * mm, "end": v(188.2, -25.43) * mm});
            skLineSegment(sketch, "E478", {"start": v(285.43, -123.55) * mm, "end": v(284.96, -123.6) * mm});
            skLineSegment(sketch, "E479", {"start": v(188.7, -120.5) * mm, "end": v(189.07, -120.2) * mm});
            skLineSegment(sketch, "E480", {"start": v(188.41, -120.87) * mm, "end": v(188.7, -120.5) * mm});
            skLineSegment(sketch, "E481", {"start": v(188.23, -121.3) * mm, "end": v(188.41, -120.87) * mm});
            skLineSegment(sketch, "E482", {"start": v(213.88, -112.21) * mm, "end": v(214.35, -112.15) * mm});
            skLineSegment(sketch, "E483", {"start": v(214.35, -112.15) * mm, "end": v(214.81, -112.21) * mm});
            skLineSegment(sketch, "E484", {"start": v(213.45, -112.4) * mm, "end": v(213.88, -112.21) * mm});
            skLineSegment(sketch, "E485", {"start": v(212.79, -113.05) * mm, "end": v(213.07, -112.68) * mm});
            skLineSegment(sketch, "E486", {"start": v(284.47, -24.11) * mm, "end": v(284.94, -24.05) * mm});
            skLineSegment(sketch, "E487", {"start": v(215.87, -38.1) * mm, "end": v(216.05, -38.54) * mm});
            skLineSegment(sketch, "E488", {"start": v(216.05, -39.48) * mm, "end": v(215.87, -39.9) * mm});
            skLineSegment(sketch, "E489", {"start": v(214.81, -115.7) * mm, "end": v(214.35, -115.75) * mm});
            skLineSegment(sketch, "E490", {"start": v(214.35, -115.75) * mm, "end": v(213.88, -115.7) * mm});
            skLineSegment(sketch, "E491", {"start": v(212.57, -38.54) * mm, "end": v(212.75, -38.1) * mm});
            skLineSegment(sketch, "E492", {"start": v(212.51, -39) * mm, "end": v(212.57, -38.54) * mm});
            skLineSegment(sketch, "E493", {"start": v(280.79, -32.1) * mm, "end": v(280.79, -31) * mm});
            skLineSegment(sketch, "E494", {"start": v(280.79, -31) * mm, "end": v(281.94, -31) * mm});
            skLineSegment(sketch, "E495", {"start": v(281.94, -29.9) * mm, "end": v(280.79, -29.9) * mm});
            skLineSegment(sketch, "E496", {"start": v(280.79, -32.1) * mm, "end": v(281.94, -32.1) * mm});
            skLineSegment(sketch, "E497", {"start": v(194.73, -116.54) * mm, "end": v(194.73, -115.44) * mm});
            skLineSegment(sketch, "E498", {"start": v(189.05, -24.34) * mm, "end": v(189.48, -24.16) * mm});
            skLineSegment(sketch, "E499", {"start": v(262.6, -112.22) * mm, "end": v(263.07, -112.29) * mm});
            skLineSegment(sketch, "E500", {"start": v(263.07, -112.29) * mm, "end": v(263.27, -112.37) * mm});
            skLineSegment(sketch, "E501", {"start": v(263.5, -112.47) * mm, "end": v(263.88, -112.75) * mm});
            skLineSegment(sketch, "E502", {"start": v(263.88, -112.75) * mm, "end": v(264.17, -113.13) * mm});
            skLineSegment(sketch, "E503", {"start": v(264.38, -32.7) * mm, "end": v(264.31, -33.17) * mm});
            skLineSegment(sketch, "E504", {"start": v(264.34, -114.5) * mm, "end": v(264.16, -114.93) * mm});
            skLineSegment(sketch, "E505", {"start": v(264.16, -114.93) * mm, "end": v(263.88, -115.3) * mm});
            skLineSegment(sketch, "E506", {"start": v(263.88, -115.3) * mm, "end": v(263.5, -115.58) * mm});
            skLineSegment(sketch, "E507", {"start": v(262.14, -112.29) * mm, "end": v(262.6, -112.22) * mm});
            skLineSegment(sketch, "E508", {"start": v(263.85, -33.98) * mm, "end": v(263.48, -34.27) * mm});
            skLineSegment(sketch, "E509", {"start": v(212.6, -113.49) * mm, "end": v(212.79, -113.05) * mm});
            skLineSegment(sketch, "E510", {"start": v(212.55, -113.95) * mm, "end": v(212.6, -113.49) * mm});
            skLineSegment(sketch, "E511", {"start": v(262.58, -30.9) * mm, "end": v(263.04, -30.97) * mm});
            skLineSegment(sketch, "E512", {"start": v(283.14, -25.85) * mm, "end": v(283.2, -25.39) * mm});
            skLineSegment(sketch, "E513", {"start": v(285.84, -24.3) * mm, "end": v(286.21, -24.58) * mm});
            skLineSegment(sketch, "E514", {"start": v(284.04, -24.3) * mm, "end": v(284.47, -24.11) * mm});
            skLineSegment(sketch, "E515", {"start": v(284.9, -120.02) * mm, "end": v(284.96, -120) * mm});
            skLineSegment(sketch, "E516", {"start": v(188.67, -27.17) * mm, "end": v(188.39, -26.8) * mm});
            skLineSegment(sketch, "E517", {"start": v(188.7, -123.04) * mm, "end": v(188.41, -122.67) * mm});
            skLineSegment(sketch, "E518", {"start": v(263.5, -115.58) * mm, "end": v(263.07, -115.76) * mm});
            skLineSegment(sketch, "E519", {"start": v(263.07, -115.76) * mm, "end": v(262.6, -115.82) * mm});
            skLineSegment(sketch, "E520", {"start": v(262.6, -115.82) * mm, "end": v(262.2, -115.77) * mm});
            skLineSegment(sketch, "E521", {"start": v(215.62, -115.23) * mm, "end": v(215.25, -115.51) * mm});
            skLineSegment(sketch, "E522", {"start": v(215.25, -115.51) * mm, "end": v(214.81, -115.7) * mm});
            skLineSegment(sketch, "E523", {"start": v(191.5, -26.8) * mm, "end": v(191.22, -27.17) * mm});
            skLineSegment(sketch, "E524", {"start": v(284.9, -27.65) * mm, "end": v(284.47, -27.6) * mm});
            skLineSegment(sketch, "E525", {"start": v(189.48, -27.64) * mm, "end": v(189.04, -27.46) * mm});
            skLineSegment(sketch, "E526", {"start": v(285.86, -120.25) * mm, "end": v(286.24, -120.54) * mm});
            skLineSegment(sketch, "E527", {"start": v(285.4, -24.11) * mm, "end": v(285.84, -24.3) * mm});
            skLineSegment(sketch, "E528", {"start": v(286.5, -24.95) * mm, "end": v(286.68, -25.39) * mm});
            skLineSegment(sketch, "E529", {"start": v(191.7, -122.23) * mm, "end": v(191.53, -122.67) * mm});
            skLineSegment(sketch, "E530", {"start": v(191.77, -121.77) * mm, "end": v(191.76, -121.84) * mm});
            skLineSegment(sketch, "E531", {"start": v(213.88, -115.7) * mm, "end": v(213.52, -115.54) * mm});
            skLineSegment(sketch, "E532", {"start": v(213.45, -115.51) * mm, "end": v(213.26, -115.34) * mm});
            skLineSegment(sketch, "E533", {"start": v(214.31, -37.2) * mm, "end": v(214.78, -37.27) * mm});
            skLineSegment(sketch, "E534", {"start": v(214.78, -37.27) * mm, "end": v(215.21, -37.45) * mm});
            skLineSegment(sketch, "E535", {"start": v(215.21, -37.45) * mm, "end": v(215.43, -37.62) * mm});
            skLineSegment(sketch, "E536", {"start": v(284.94, -24.05) * mm, "end": v(285.4, -24.11) * mm});
            skLineSegment(sketch, "E537", {"start": v(283.2, -26.32) * mm, "end": v(283.14, -25.85) * mm});
            skLineSegment(sketch, "E538", {"start": v(283.67, -24.58) * mm, "end": v(284.04, -24.3) * mm});
            skLineSegment(sketch, "E539", {"start": v(216.08, -113.49) * mm, "end": v(216.15, -113.95) * mm});
            skLineSegment(sketch, "E540", {"start": v(216.15, -113.95) * mm, "end": v(216.08, -114.42) * mm});
            skLineSegment(sketch, "E541", {"start": v(192.63, -29.61) * mm, "end": v(191.48, -29.61) * mm});
            skLineSegment(sketch, "E542", {"start": v(191.48, -30.71) * mm, "end": v(192.63, -30.71) * mm});
            skLineSegment(sketch, "E543", {"start": v(192.63, -30.71) * mm, "end": v(192.63, -29.61) * mm});
            skLineSegment(sketch, "E544", {"start": v(281.94, -31) * mm, "end": v(281.94, -29.9) * mm});
            skLineSegment(sketch, "E545", {"start": v(260.8, -114.02) * mm, "end": v(260.87, -113.56) * mm});
            skLineSegment(sketch, "E546", {"start": v(260.87, -113.56) * mm, "end": v(261.05, -113.12) * mm});
            skLineSegment(sketch, "E547", {"start": v(261.05, -113.12) * mm, "end": v(261.33, -112.75) * mm});
            skLineSegment(sketch, "E548", {"start": v(261.33, -112.75) * mm, "end": v(261.7, -112.47) * mm});
            skLineSegment(sketch, "E549", {"start": v(191.7, -121.3) * mm, "end": v(191.77, -121.77) * mm});
            skLineSegment(sketch, "E550", {"start": v(191.53, -120.87) * mm, "end": v(191.7, -121.3) * mm});
            skLineSegment(sketch, "E551", {"start": v(191.24, -120.5) * mm, "end": v(191.53, -120.87) * mm});
            skLineSegment(sketch, "E552", {"start": v(283.69, -123.08) * mm, "end": v(283.4, -122.7) * mm});
            skLineSegment(sketch, "E553", {"start": v(188.67, -24.63) * mm, "end": v(189.05, -24.34) * mm});
            skLineSegment(sketch, "E554", {"start": v(191.5, -25) * mm, "end": v(191.68, -25.43) * mm});
            skLineSegment(sketch, "E555", {"start": v(191.68, -25.43) * mm, "end": v(191.74, -25.84) * mm});
            skLineSegment(sketch, "E556", {"start": v(191.74, -25.84) * mm, "end": v(191.75, -25.9) * mm});
            skLineSegment(sketch, "E557", {"start": v(286.21, -24.58) * mm, "end": v(286.5, -24.95) * mm});
            skLineSegment(sketch, "E558", {"start": v(286.21, -27.13) * mm, "end": v(285.84, -27.41) * mm});
            skLineSegment(sketch, "E559", {"start": v(286.5, -26.75) * mm, "end": v(286.21, -27.13) * mm});
            skLineSegment(sketch, "E560", {"start": v(215.21, -40.57) * mm, "end": v(214.78, -40.75) * mm});
            skLineSegment(sketch, "E561", {"start": v(215.59, -37.74) * mm, "end": v(215.87, -38.1) * mm});
            skLineSegment(sketch, "E562", {"start": v(260.84, -32.24) * mm, "end": v(261.02, -31.8) * mm});
            skLineSegment(sketch, "E563", {"start": v(260.78, -32.7) * mm, "end": v(260.84, -32.24) * mm});
            skLineSegment(sketch, "E564", {"start": v(261.05, -114.92) * mm, "end": v(260.87, -114.5) * mm});
            skLineSegment(sketch, "E565", {"start": v(264.17, -113.13) * mm, "end": v(264.34, -113.56) * mm});
            skLineSegment(sketch, "E566", {"start": v(264.34, -113.56) * mm, "end": v(264.4, -114.03) * mm});
            skLineSegment(sketch, "E567", {"start": v(264.4, -114.03) * mm, "end": v(264.34, -114.5) * mm});
            skLineSegment(sketch, "E568", {"start": v(263.85, -31.44) * mm, "end": v(264.14, -31.8) * mm});
            skLineSegment(sketch, "E569", {"start": v(261.3, -33.98) * mm, "end": v(261.02, -33.6) * mm});
            skLineSegment(sketch, "E570", {"start": v(262.58, -34.5) * mm, "end": v(262.11, -34.45) * mm});
            skLineSegment(sketch, "E571", {"start": v(216.11, -39) * mm, "end": v(216.05, -39.48) * mm});
            skLineSegment(sketch, "E572", {"start": v(215.59, -40.28) * mm, "end": v(215.21, -40.57) * mm});
            skLineSegment(sketch, "E573", {"start": v(283.67, -27.13) * mm, "end": v(283.38, -26.75) * mm});
            skLineSegment(sketch, "E574", {"start": v(284.94, -27.65) * mm, "end": v(284.9, -27.65) * mm});
            skLineSegment(sketch, "E575", {"start": v(284.47, -27.6) * mm, "end": v(284.04, -27.41) * mm});
            skLineSegment(sketch, "E576", {"start": v(286.68, -25.39) * mm, "end": v(286.74, -25.85) * mm});
            skLineSegment(sketch, "E577", {"start": v(214.81, -112.21) * mm, "end": v(215.25, -112.4) * mm});
            skLineSegment(sketch, "E578", {"start": v(215.62, -112.68) * mm, "end": v(215.9, -113.05) * mm});
            skLineSegment(sketch, "E579", {"start": v(263.62, -31.26) * mm, "end": v(263.7, -31.3) * mm});
            skLineSegment(sketch, "E580", {"start": v(261.75, -34.3) * mm, "end": v(261.68, -34.27) * mm});
            skLineSegment(sketch, "E581", {"start": v(261.53, -34.13) * mm, "end": v(261.3, -33.98) * mm});
            skLineSegment(sketch, "E582", {"start": v(215.43, -112.51) * mm, "end": v(215.62, -112.68) * mm});
            skLineSegment(sketch, "E583", {"start": v(215.36, -112.48) * mm, "end": v(215.43, -112.51) * mm});
            skLineSegment(sketch, "E584", {"start": v(213.46, -40.59) * mm, "end": v(213.41, -40.57) * mm});
            skLineSegment(sketch, "E585", {"start": v(261.96, -115.67) * mm, "end": v(261.7, -115.58) * mm});
            skLineSegment(sketch, "E586", {"start": v(213.3, -40.47) * mm, "end": v(213.04, -40.28) * mm});
            skLineSegment(sketch, "E587", {"start": v(263.33, -112.38) * mm, "end": v(263.5, -112.47) * mm});
            skLineSegment(sketch, "E588", {"start": v(263.27, -112.37) * mm, "end": v(263.33, -112.38) * mm});
            skLineSegment(sketch, "E589", {"start": v(262.2, -115.77) * mm, "end": v(262.14, -115.76) * mm});
            skLineSegment(sketch, "E590", {"start": v(213.52, -115.54) * mm, "end": v(213.45, -115.51) * mm});
            skLineSegment(sketch, "E591", {"start": v(213.26, -115.34) * mm, "end": v(213.07, -115.23) * mm});
            skLineSegment(sketch, "E592", {"start": v(215.48, -37.63) * mm, "end": v(215.59, -37.74) * mm});
            skLineSegment(sketch, "E593", {"start": v(215.43, -37.62) * mm, "end": v(215.48, -37.63) * mm});
            skLineSegment(sketch, "E594", {"start": v(263.7, -31.3) * mm, "end": v(263.85, -31.44) * mm});
            skLineSegment(sketch, "E595", {"start": v(-142.74, 154.97) * mm, "end": v(-146.26, 154.97) * mm});
            skLineSegment(sketch, "E596", {"start": v(-146.26, 154.97) * mm, "end": v(-146.26, 166.26) * mm});
            skLineSegment(sketch, "E597", {"start": v(-146.26, 166.26) * mm, "end": v(-142.74, 166.26) * mm});
            skLineSegment(sketch, "E598", {"start": v(-142.74, 166.26) * mm, "end": v(-142.74, 154.97) * mm});
            skLineSegment(sketch, "E599", {"start": v(-142.63, 167.87) * mm, "end": v(-146.36, 167.87) * mm});
            skLineSegment(sketch, "E600", {"start": v(-146.36, 167.87) * mm, "end": v(-146.36, 170.62) * mm});
            skLineSegment(sketch, "E601", {"start": v(-146.36, 170.62) * mm, "end": v(-142.63, 170.62) * mm});
            skLineSegment(sketch, "E602", {"start": v(-142.63, 170.62) * mm, "end": v(-142.63, 167.87) * mm});
            skLineSegment(sketch, "E603", {"start": v(-129.24, 159.82) * mm, "end": v(-129.34, 158.77) * mm});
            skLineSegment(sketch, "E604", {"start": v(-129.34, 158.77) * mm, "end": v(-129.64, 157.81) * mm});
            skLineSegment(sketch, "E605", {"start": v(-129.64, 157.81) * mm, "end": v(-130.15, 156.98) * mm});
            skLineSegment(sketch, "E606", {"start": v(-130.15, 156.98) * mm, "end": v(-130.84, 156.28) * mm});
            skLineSegment(sketch, "E607", {"start": v(-130.84, 156.28) * mm, "end": v(-131.7, 155.72) * mm});
            skLineSegment(sketch, "E608", {"start": v(-131.7, 155.72) * mm, "end": v(-132.7, 155.3) * mm});
            skLineSegment(sketch, "E609", {"start": v(-132.7, 155.3) * mm, "end": v(-133.9, 155.05) * mm});
            skLineSegment(sketch, "E610", {"start": v(-133.9, 155.05) * mm, "end": v(-135.31, 154.97) * mm});
            skLineSegment(sketch, "E611", {"start": v(-135.31, 154.97) * mm, "end": v(-136.94, 155.04) * mm});
            skLineSegment(sketch, "E612", {"start": v(-136.94, 155.04) * mm, "end": v(-138.31, 155.26) * mm});
            skLineSegment(sketch, "E613", {"start": v(-138.31, 155.26) * mm, "end": v(-140.35, 155.91) * mm});
            skLineSegment(sketch, "E614", {"start": v(-140.35, 155.91) * mm, "end": v(-140.35, 159.16) * mm});
            skLineSegment(sketch, "E615", {"start": v(-140.35, 159.16) * mm, "end": v(-139.99, 159.16) * mm});
            skLineSegment(sketch, "E616", {"start": v(-139.99, 159.16) * mm, "end": v(-139.1, 158.67) * mm});
            skLineSegment(sketch, "E617", {"start": v(-139.1, 158.67) * mm, "end": v(-138.05, 158.26) * mm});
            skLineSegment(sketch, "E618", {"start": v(-138.05, 158.26) * mm, "end": v(-137, 157.97) * mm});
            skLineSegment(sketch, "E619", {"start": v(-137, 157.97) * mm, "end": v(-136.03, 157.87) * mm});
            skLineSegment(sketch, "E620", {"start": v(-136.03, 157.87) * mm, "end": v(-134.84, 157.97) * mm});
            skLineSegment(sketch, "E621", {"start": v(-134.84, 157.97) * mm, "end": v(-134.26, 158.12) * mm});
            skLineSegment(sketch, "E622", {"start": v(-134.26, 158.12) * mm, "end": v(-133.77, 158.39) * mm});
            skLineSegment(sketch, "E623", {"start": v(-133.77, 158.39) * mm, "end": v(-133.23, 159) * mm});
            skLineSegment(sketch, "E624", {"start": v(-133.23, 159) * mm, "end": v(-133.07, 159.45) * mm});
            skLineSegment(sketch, "E625", {"start": v(-133.07, 159.45) * mm, "end": v(-133.02, 160.05) * mm});
            skLineSegment(sketch, "E626", {"start": v(-133.02, 160.05) * mm, "end": v(-133.1, 160.63) * mm});
            skLineSegment(sketch, "E627", {"start": v(-133.1, 160.63) * mm, "end": v(-133.31, 161.07) * mm});
            skLineSegment(sketch, "E628", {"start": v(-133.31, 161.07) * mm, "end": v(-133.65, 161.38) * mm});
            skLineSegment(sketch, "E629", {"start": v(-133.65, 161.38) * mm, "end": v(-134.09, 161.59) * mm});
            skLineSegment(sketch, "E630", {"start": v(-134.09, 161.59) * mm, "end": v(-135.24, 161.78) * mm});
            skLineSegment(sketch, "E631", {"start": v(-135.24, 161.78) * mm, "end": v(-136.43, 161.8) * mm});
            skLineSegment(sketch, "E632", {"start": v(-136.43, 161.8) * mm, "end": v(-137.07, 161.8) * mm});
            skLineSegment(sketch, "E633", {"start": v(-137.07, 161.8) * mm, "end": v(-137.07, 164.43) * mm});
            skLineSegment(sketch, "E634", {"start": v(-137.07, 164.43) * mm, "end": v(-136.48, 164.43) * mm});
            skLineSegment(sketch, "E635", {"start": v(-136.48, 164.43) * mm, "end": v(-135.22, 164.5) * mm});
            skLineSegment(sketch, "E636", {"start": v(-135.22, 164.5) * mm, "end": v(-134.25, 164.73) * mm});
            skLineSegment(sketch, "E637", {"start": v(-134.25, 164.73) * mm, "end": v(-133.62, 165.27) * mm});
            skLineSegment(sketch, "E638", {"start": v(-133.62, 165.27) * mm, "end": v(-133.45, 165.67) * mm});
            skLineSegment(sketch, "E639", {"start": v(-133.45, 165.67) * mm, "end": v(-133.4, 166.2) * mm});
            skLineSegment(sketch, "E640", {"start": v(-133.4, 166.2) * mm, "end": v(-133.44, 166.6) * mm});
            skLineSegment(sketch, "E641", {"start": v(-133.44, 166.6) * mm, "end": v(-133.6, 166.93) * mm});
            skLineSegment(sketch, "E642", {"start": v(-133.6, 166.93) * mm, "end": v(-134.13, 167.38) * mm});
            skLineSegment(sketch, "E643", {"start": v(-134.13, 167.38) * mm, "end": v(-134.97, 167.62) * mm});
            skLineSegment(sketch, "E644", {"start": v(-134.97, 167.62) * mm, "end": v(-135.8, 167.68) * mm});
            skLineSegment(sketch, "E645", {"start": v(-135.8, 167.68) * mm, "end": v(-136.92, 167.55) * mm});
            skLineSegment(sketch, "E646", {"start": v(-136.92, 167.55) * mm, "end": v(-138.04, 167.22) * mm});
            skLineSegment(sketch, "E647", {"start": v(-138.04, 167.22) * mm, "end": v(-138.92, 166.8) * mm});
            skLineSegment(sketch, "E648", {"start": v(-138.92, 166.8) * mm, "end": v(-139.6, 166.41) * mm});
            skLineSegment(sketch, "E649", {"start": v(-139.6, 166.41) * mm, "end": v(-139.92, 166.41) * mm});
            skLineSegment(sketch, "E650", {"start": v(-139.92, 166.41) * mm, "end": v(-139.92, 169.62) * mm});
            skLineSegment(sketch, "E651", {"start": v(-139.92, 169.62) * mm, "end": v(-137.83, 170.26) * mm});
            skLineSegment(sketch, "E652", {"start": v(-137.83, 170.26) * mm, "end": v(-136.5, 170.5) * mm});
            skLineSegment(sketch, "E653", {"start": v(-136.5, 170.5) * mm, "end": v(-135.15, 170.57) * mm});
            skLineSegment(sketch, "E654", {"start": v(-135.15, 170.57) * mm, "end": v(-133.9, 170.51) * mm});
            skLineSegment(sketch, "E655", {"start": v(-133.9, 170.51) * mm, "end": v(-132.83, 170.34) * mm});
            skLineSegment(sketch, "E656", {"start": v(-132.83, 170.34) * mm, "end": v(-131.92, 170.05) * mm});
            skLineSegment(sketch, "E657", {"start": v(-131.92, 170.05) * mm, "end": v(-131.16, 169.66) * mm});
            skLineSegment(sketch, "E658", {"start": v(-131.16, 169.66) * mm, "end": v(-130.49, 169.13) * mm});
            skLineSegment(sketch, "E659", {"start": v(-130.49, 169.13) * mm, "end": v(-130.01, 168.46) * mm});
            skLineSegment(sketch, "E660", {"start": v(-130.01, 168.46) * mm, "end": v(-129.73, 167.69) * mm});
            skLineSegment(sketch, "E661", {"start": v(-129.73, 167.69) * mm, "end": v(-129.63, 166.82) * mm});
            skLineSegment(sketch, "E662", {"start": v(-129.63, 166.82) * mm, "end": v(-129.81, 165.62) * mm});
            skLineSegment(sketch, "E663", {"start": v(-129.81, 165.62) * mm, "end": v(-130.37, 164.58) * mm});
            skLineSegment(sketch, "E664", {"start": v(-130.37, 164.58) * mm, "end": v(-131.23, 163.79) * mm});
            skLineSegment(sketch, "E665", {"start": v(-131.23, 163.79) * mm, "end": v(-132.32, 163.34) * mm});
            skLineSegment(sketch, "E666", {"start": v(-132.32, 163.34) * mm, "end": v(-132.32, 163.2) * mm});
            skLineSegment(sketch, "E667", {"start": v(-132.32, 163.2) * mm, "end": v(-131.27, 162.92) * mm});
            skLineSegment(sketch, "E668", {"start": v(-131.27, 162.92) * mm, "end": v(-130.28, 162.3) * mm});
            skLineSegment(sketch, "E669", {"start": v(-130.28, 162.3) * mm, "end": v(-129.87, 161.85) * mm});
            skLineSegment(sketch, "E670", {"start": v(-129.87, 161.85) * mm, "end": v(-129.53, 161.29) * mm});
            skLineSegment(sketch, "E671", {"start": v(-129.53, 161.29) * mm, "end": v(-129.31, 160.61) * mm});
            skLineSegment(sketch, "E672", {"start": v(-129.31, 160.61) * mm, "end": v(-129.24, 159.82) * mm});
            skLineSegment(sketch, "E673", {"start": v(216.99, -42.2) * mm, "end": v(216.99, -44.4) * mm});
            skLineSegment(sketch, "E674", {"start": v(214.86, -27.58) * mm, "end": v(214.8, -27.12) * mm});
            skLineSegment(sketch, "E675", {"start": v(215.7, -25.56) * mm, "end": v(216.14, -25.38) * mm});
            skLineSegment(sketch, "E676", {"start": v(215.33, -28.4) * mm, "end": v(215.04, -28.02) * mm});
            skLineSegment(sketch, "E677", {"start": v(218.16, -28.02) * mm, "end": v(217.87, -28.4) * mm});
            skLineSegment(sketch, "E678", {"start": v(216.13, -28.86) * mm, "end": v(215.7, -28.68) * mm});
            skLineSegment(sketch, "E679", {"start": v(215.33, -25.85) * mm, "end": v(215.7, -25.56) * mm});
            skLineSegment(sketch, "E680", {"start": v(217.07, -28.86) * mm, "end": v(216.6, -28.92) * mm});
            skLineSegment(sketch, "E681", {"start": v(216.6, -28.92) * mm, "end": v(216.55, -28.91) * mm});
            skLineSegment(sketch, "E682", {"start": v(218.4, -27.12) * mm, "end": v(218.34, -27.58) * mm});
            skLineSegment(sketch, "E683", {"start": v(214.86, -26.65) * mm, "end": v(215.04, -26.22) * mm});
            skLineSegment(sketch, "E684", {"start": v(217.87, -28.4) * mm, "end": v(217.5, -28.68) * mm});
            skLineSegment(sketch, "E685", {"start": v(218.16, -26.22) * mm, "end": v(218.34, -26.65) * mm});
            skLineSegment(sketch, "E686", {"start": v(218.34, -26.65) * mm, "end": v(218.4, -27.06) * mm});
            skLineSegment(sketch, "E687", {"start": v(218.4, -27.06) * mm, "end": v(218.4, -27.12) * mm});
            skLineSegment(sketch, "E688", {"start": v(217.5, -28.68) * mm, "end": v(217.07, -28.86) * mm});
            skLineSegment(sketch, "E689", {"start": v(215.04, -28.02) * mm, "end": v(214.86, -27.58) * mm});
            skLineSegment(sketch, "E690", {"start": v(217.5, -25.56) * mm, "end": v(217.87, -25.85) * mm});
            skLineSegment(sketch, "E691", {"start": v(217.87, -25.85) * mm, "end": v(218.16, -26.22) * mm});
            skLineSegment(sketch, "E692", {"start": v(214.8, -27.12) * mm, "end": v(214.86, -26.65) * mm});
            skLineSegment(sketch, "E693", {"start": v(216.55, -28.91) * mm, "end": v(216.13, -28.86) * mm});
            skLineSegment(sketch, "E694", {"start": v(216.14, -25.38) * mm, "end": v(216.6, -25.32) * mm});
            skLineSegment(sketch, "E695", {"start": v(215.7, -28.68) * mm, "end": v(215.33, -28.4) * mm});
            skLineSegment(sketch, "E696", {"start": v(217.07, -25.38) * mm, "end": v(217.5, -25.56) * mm});
            skLineSegment(sketch, "E697", {"start": v(216.6, -25.32) * mm, "end": v(217.07, -25.38) * mm});
            skLineSegment(sketch, "E698", {"start": v(215.04, -26.22) * mm, "end": v(215.33, -25.85) * mm});
            skLineSegment(sketch, "E699", {"start": v(218.34, -27.58) * mm, "end": v(218.16, -28.02) * mm});
            skLineSegment(sketch, "E700", {"start": v(260.38, -28.82) * mm, "end": v(259.97, -28.76) * mm});
            skLineSegment(sketch, "E701", {"start": v(258.64, -27.03) * mm, "end": v(258.7, -26.56) * mm});
            skLineSegment(sketch, "E702", {"start": v(259.54, -25.47) * mm, "end": v(259.97, -25.29) * mm});
            skLineSegment(sketch, "E703", {"start": v(259.16, -28.3) * mm, "end": v(258.88, -27.93) * mm});
            skLineSegment(sketch, "E704", {"start": v(262, -27.93) * mm, "end": v(261.7, -28.3) * mm});
            skLineSegment(sketch, "E705", {"start": v(259.97, -28.76) * mm, "end": v(259.53, -28.58) * mm});
            skLineSegment(sketch, "E706", {"start": v(259.16, -25.75) * mm, "end": v(259.54, -25.47) * mm});
            skLineSegment(sketch, "E707", {"start": v(261.7, -28.3) * mm, "end": v(261.33, -28.58) * mm});
            skLineSegment(sketch, "E708", {"start": v(258.7, -26.56) * mm, "end": v(258.88, -26.13) * mm});
            skLineSegment(sketch, "E709", {"start": v(261.33, -28.58) * mm, "end": v(260.9, -28.76) * mm});
            skLineSegment(sketch, "E710", {"start": v(258.88, -27.93) * mm, "end": v(258.7, -27.5) * mm});
            skLineSegment(sketch, "E711", {"start": v(261.34, -25.47) * mm, "end": v(261.7, -25.75) * mm});
            skLineSegment(sketch, "E712", {"start": v(261.7, -25.75) * mm, "end": v(262, -26.13) * mm});
            skLineSegment(sketch, "E713", {"start": v(262.24, -27.03) * mm, "end": v(262.17, -27.5) * mm});
            skLineSegment(sketch, "E714", {"start": v(260.43, -28.83) * mm, "end": v(260.38, -28.82) * mm});
            skLineSegment(sketch, "E715", {"start": v(260.9, -28.76) * mm, "end": v(260.54, -28.81) * mm});
            skLineSegment(sketch, "E716", {"start": v(260.44, -25.23) * mm, "end": v(260.9, -25.29) * mm});
            skLineSegment(sketch, "E717", {"start": v(260.9, -25.29) * mm, "end": v(261.34, -25.47) * mm});
            skLineSegment(sketch, "E718", {"start": v(258.88, -26.13) * mm, "end": v(259.16, -25.75) * mm});
            skLineSegment(sketch, "E719", {"start": v(262.17, -27.5) * mm, "end": v(262, -27.93) * mm});
            skLineSegment(sketch, "E720", {"start": v(258.7, -27.5) * mm, "end": v(258.64, -27.08) * mm});
            skLineSegment(sketch, "E721", {"start": v(259.97, -25.29) * mm, "end": v(260.44, -25.23) * mm});
            skLineSegment(sketch, "E722", {"start": v(262, -26.13) * mm, "end": v(262.17, -26.56) * mm});
            skLineSegment(sketch, "E723", {"start": v(262.17, -26.56) * mm, "end": v(262.23, -26.97) * mm});
            skLineSegment(sketch, "E724", {"start": v(262.23, -26.97) * mm, "end": v(262.24, -27.03) * mm});
            skLineSegment(sketch, "E725", {"start": v(259.53, -28.58) * mm, "end": v(259.16, -28.3) * mm});
            skLineSegment(sketch, "E726", {"start": v(260.54, -28.81) * mm, "end": v(260.43, -28.83) * mm});
            skLineSegment(sketch, "E727", {"start": v(258.64, -27.08) * mm, "end": v(258.64, -27.03) * mm});
            skLineSegment(sketch, "E728", {"start": v(215.63, -122.6) * mm, "end": v(215.26, -122.32) * mm});
            skLineSegment(sketch, "E729", {"start": v(214.98, -120.14) * mm, "end": v(215.26, -119.77) * mm});
            skLineSegment(sketch, "E730", {"start": v(218.27, -120.58) * mm, "end": v(218.33, -120.99) * mm});
            skLineSegment(sketch, "E731", {"start": v(218.33, -120.99) * mm, "end": v(218.34, -121.04) * mm});
            skLineSegment(sketch, "E732", {"start": v(217, -119.3) * mm, "end": v(217.44, -119.48) * mm});
            skLineSegment(sketch, "E733", {"start": v(214.74, -121.04) * mm, "end": v(214.8, -120.58) * mm});
            skLineSegment(sketch, "E734", {"start": v(215.64, -119.48) * mm, "end": v(216.07, -119.3) * mm});
            skLineSegment(sketch, "E735", {"start": v(215.26, -122.32) * mm, "end": v(214.98, -121.94) * mm});
            skLineSegment(sketch, "E736", {"start": v(218.1, -121.94) * mm, "end": v(217.8, -122.32) * mm});
            skLineSegment(sketch, "E737", {"start": v(216.07, -122.78) * mm, "end": v(215.63, -122.6) * mm});
            skLineSegment(sketch, "E738", {"start": v(215.26, -119.77) * mm, "end": v(215.64, -119.48) * mm});
            skLineSegment(sketch, "E739", {"start": v(218.1, -120.14) * mm, "end": v(218.27, -120.58) * mm});
            skLineSegment(sketch, "E740", {"start": v(214.8, -121.5) * mm, "end": v(214.74, -121.04) * mm});
            skLineSegment(sketch, "E741", {"start": v(214.8, -120.58) * mm, "end": v(214.98, -120.14) * mm});
            skLineSegment(sketch, "E742", {"start": v(216.54, -119.24) * mm, "end": v(217, -119.3) * mm});
            skLineSegment(sketch, "E743", {"start": v(217, -122.78) * mm, "end": v(216.53, -122.84) * mm});
            skLineSegment(sketch, "E744", {"start": v(216.07, -119.3) * mm, "end": v(216.54, -119.24) * mm});
            skLineSegment(sketch, "E745", {"start": v(217.8, -122.32) * mm, "end": v(217.43, -122.6) * mm});
            skLineSegment(sketch, "E746", {"start": v(217.43, -122.6) * mm, "end": v(217, -122.78) * mm});
            skLineSegment(sketch, "E747", {"start": v(214.98, -121.94) * mm, "end": v(214.8, -121.5) * mm});
            skLineSegment(sketch, "E748", {"start": v(218.27, -121.5) * mm, "end": v(218.1, -121.94) * mm});
            skLineSegment(sketch, "E749", {"start": v(216.48, -122.84) * mm, "end": v(216.07, -122.78) * mm});
            skLineSegment(sketch, "E750", {"start": v(217.44, -119.48) * mm, "end": v(217.8, -119.77) * mm});
            skLineSegment(sketch, "E751", {"start": v(217.8, -119.77) * mm, "end": v(218.1, -120.14) * mm});
            skLineSegment(sketch, "E752", {"start": v(216.53, -122.84) * mm, "end": v(216.48, -122.84) * mm});
            skLineSegment(sketch, "E753", {"start": v(218.34, -121.04) * mm, "end": v(218.33, -121.08) * mm});
            skLineSegment(sketch, "E754", {"start": v(218.33, -121.08) * mm, "end": v(218.27, -121.5) * mm});
            skLineSegment(sketch, "E755", {"start": v(261.37, -122.6) * mm, "end": v(260.93, -122.78) * mm});
            skLineSegment(sketch, "E756", {"start": v(258.9, -121.94) * mm, "end": v(258.73, -121.5) * mm});
            skLineSegment(sketch, "E757", {"start": v(261.37, -119.48) * mm, "end": v(261.74, -119.77) * mm});
            skLineSegment(sketch, "E758", {"start": v(261.74, -119.77) * mm, "end": v(262.03, -120.14) * mm});
            skLineSegment(sketch, "E759", {"start": v(258.67, -121.04) * mm, "end": v(258.73, -120.58) * mm});
            skLineSegment(sketch, "E760", {"start": v(259.57, -119.48) * mm, "end": v(260, -119.3) * mm});
            skLineSegment(sketch, "E761", {"start": v(259.2, -122.32) * mm, "end": v(258.9, -121.94) * mm});
            skLineSegment(sketch, "E762", {"start": v(262.03, -121.94) * mm, "end": v(261.74, -122.32) * mm});
            skLineSegment(sketch, "E763", {"start": v(260, -122.78) * mm, "end": v(259.57, -122.6) * mm});
            skLineSegment(sketch, "E764", {"start": v(259.2, -119.77) * mm, "end": v(259.57, -119.48) * mm});
            skLineSegment(sketch, "E765", {"start": v(262.03, -120.14) * mm, "end": v(262.2, -120.58) * mm});
            skLineSegment(sketch, "E766", {"start": v(262.2, -120.58) * mm, "end": v(262.26, -120.99) * mm});
            skLineSegment(sketch, "E767", {"start": v(262.26, -120.99) * mm, "end": v(262.27, -121.04) * mm});
            skLineSegment(sketch, "E768", {"start": v(260.93, -119.3) * mm, "end": v(261.37, -119.48) * mm});
            skLineSegment(sketch, "E769", {"start": v(260.47, -119.24) * mm, "end": v(260.54, -119.25) * mm});
            skLineSegment(sketch, "E770", {"start": v(260.93, -122.78) * mm, "end": v(260.47, -122.84) * mm});
            skLineSegment(sketch, "E771", {"start": v(259.57, -122.6) * mm, "end": v(259.2, -122.32) * mm});
            skLineSegment(sketch, "E772", {"start": v(258.73, -121.5) * mm, "end": v(258.67, -121.08) * mm});
            skLineSegment(sketch, "E773", {"start": v(262.2, -121.5) * mm, "end": v(262.03, -121.94) * mm});
            skLineSegment(sketch, "E774", {"start": v(260, -119.3) * mm, "end": v(260.47, -119.24) * mm});
            skLineSegment(sketch, "E775", {"start": v(260.47, -122.84) * mm, "end": v(260.41, -122.84) * mm});
            skLineSegment(sketch, "E776", {"start": v(262.27, -121.04) * mm, "end": v(262.2, -121.5) * mm});
            skLineSegment(sketch, "E777", {"start": v(258.73, -120.58) * mm, "end": v(258.9, -120.14) * mm});
            skLineSegment(sketch, "E778", {"start": v(261.74, -122.32) * mm, "end": v(261.37, -122.6) * mm});
            skLineSegment(sketch, "E779", {"start": v(258.9, -120.14) * mm, "end": v(259.2, -119.77) * mm});
            skLineSegment(sketch, "E780", {"start": v(260.41, -122.84) * mm, "end": v(260, -122.78) * mm});
            skLineSegment(sketch, "E781", {"start": v(260.54, -119.25) * mm, "end": v(260.93, -119.3) * mm});
            skLineSegment(sketch, "E782", {"start": v(258.67, -121.08) * mm, "end": v(258.67, -121.04) * mm});
            skLineSegment(sketch, "E783", {"start": v(218.2, -32.59) * mm, "end": v(219.35, -32.59) * mm});
            skLineSegment(sketch, "E784", {"start": v(218.2, -31.49) * mm, "end": v(219.35, -31.49) * mm});
            skLineSegment(sketch, "E785", {"start": v(219.35, -30.39) * mm, "end": v(218.2, -30.39) * mm});
            skLineSegment(sketch, "E786", {"start": v(219.35, -30.39) * mm, "end": v(219.35, -31.49) * mm});
            skLineSegment(sketch, "E787", {"start": v(219.35, -31.49) * mm, "end": v(219.35, -32.59) * mm});
            skLineSegment(sketch, "E788", {"start": v(257.86, -30.84) * mm, "end": v(257.86, -31.94) * mm});
            skLineSegment(sketch, "E789", {"start": v(257.86, -30.84) * mm, "end": v(256.71, -30.84) * mm});
            skLineSegment(sketch, "E790", {"start": v(257.86, -31.94) * mm, "end": v(257.86, -33.04) * mm});
            skLineSegment(sketch, "E791", {"start": v(256.71, -33.04) * mm, "end": v(257.86, -33.04) * mm});
            skLineSegment(sketch, "E792", {"start": v(256.71, -31.94) * mm, "end": v(257.86, -31.94) * mm});
            skLineSegment(sketch, "E793", {"start": v(255.87, -116.27) * mm, "end": v(257.02, -116.27) * mm});
            skLineSegment(sketch, "E794", {"start": v(257.02, -115.17) * mm, "end": v(257.02, -116.27) * mm});
            skLineSegment(sketch, "E795", {"start": v(255.87, -117.37) * mm, "end": v(257.02, -117.37) * mm});
            skLineSegment(sketch, "E796", {"start": v(257.02, -115.17) * mm, "end": v(255.87, -115.17) * mm});
            skLineSegment(sketch, "E797", {"start": v(257.02, -116.27) * mm, "end": v(257.02, -117.37) * mm});
            skLineSegment(sketch, "E798", {"start": v(221.1, -114.8) * mm, "end": v(221.1, -115.9) * mm});
            skLineSegment(sketch, "E799", {"start": v(221.1, -114.8) * mm, "end": v(219.94, -114.8) * mm});
            skLineSegment(sketch, "E800", {"start": v(221.1, -115.9) * mm, "end": v(221.1, -117) * mm});
            skLineSegment(sketch, "E801", {"start": v(219.94, -117) * mm, "end": v(221.1, -117) * mm});
            skLineSegment(sketch, "E802", {"start": v(219.94, -115.9) * mm, "end": v(221.1, -115.9) * mm});
            skLineSegment(sketch, "E803", {"start": v(-230.54, 112.97) * mm, "end": v(-230.54, 92.97) * mm});
            skLineSegment(sketch, "E804", {"start": v(-40.54, 16.97) * mm, "end": v(-50.54, 6.97) * mm});
            skLineSegment(sketch, "E805", {"start": v(-220.54, 76.98) * mm, "end": v(-220.54, 53.98) * mm});
            skLineSegment(sketch, "E806", {"start": v(-227.58, 10.83) * mm, "end": v(-228.07, 10.66) * mm});
            skLineSegment(sketch, "E807", {"start": v(-224.54, 49.98) * mm, "end": v(-226.54, 49.98) * mm});
            skLineSegment(sketch, "E808", {"start": v(-227.58, 80.84) * mm, "end": v(-228.07, 80.67) * mm});
            skLineSegment(sketch, "E809", {"start": v(-228.07, 10.66) * mm, "end": v(-228.54, 10.43) * mm});
            skLineSegment(sketch, "E810", {"start": v(-228.98, 10.14) * mm, "end": v(-229.37, 9.8) * mm});
            skLineSegment(sketch, "E811", {"start": v(-228.54, 10.43) * mm, "end": v(-228.98, 10.14) * mm});
            skLineSegment(sketch, "E812", {"start": v(-243.54, -80.03) * mm, "end": v(-218.54, -55.03) * mm});
            skLineSegment(sketch, "E813", {"start": v(-226.54, 80.98) * mm, "end": v(-227.06, 80.94) * mm});
            skLineSegment(sketch, "E814", {"start": v(-223.01, 50.28) * mm, "end": v(-222.54, 50.51) * mm});
            skLineSegment(sketch, "E815", {"start": v(-240.54, -23.03) * mm, "end": v(-230.54, -33.03) * mm});
            skLineSegment(sketch, "E816", {"start": v(-230.54, 92.97) * mm, "end": v(-240.54, 82.97) * mm});
            skLineSegment(sketch, "E817", {"start": v(-250.54, -73.03) * mm, "end": v(-250.54, -77.03) * mm});
            skLineSegment(sketch, "E818", {"start": v(-208.54, 104.97) * mm, "end": v(-72.54, 104.97) * mm});
            skLineSegment(sketch, "E819", {"start": v(-229.72, 9.4) * mm, "end": v(-230, 8.97) * mm});
            skLineSegment(sketch, "E820", {"start": v(-229.37, 9.8) * mm, "end": v(-229.72, 9.4) * mm});
            skLineSegment(sketch, "E821", {"start": v(-250.54, 134.97) * mm, "end": v(-250.54, 132.97) * mm});
            skLineSegment(sketch, "E822", {"start": v(-60.4, 16.8) * mm, "end": v(-60.24, 16.3) * mm});
            skLineSegment(sketch, "E823", {"start": v(-60.5, 17.3) * mm, "end": v(-60.4, 16.8) * mm});
            skLineSegment(sketch, "E824", {"start": v(-223.01, 80.67) * mm, "end": v(-223.5, 80.84) * mm});
            skLineSegment(sketch, "E825", {"start": v(-221.37, 9.4) * mm, "end": v(-221.71, 9.8) * mm});
            skLineSegment(sketch, "E826", {"start": v(-58.07, 14.14) * mm, "end": v(-57.58, 13.97) * mm});
            skLineSegment(sketch, "E827", {"start": v(-230.24, 52.44) * mm, "end": v(-230, 51.98) * mm});
            skLineSegment(sketch, "E828", {"start": v(-230, 51.98) * mm, "end": v(-229.72, 51.54) * mm});
            skLineSegment(sketch, "E829", {"start": v(-229.72, 51.54) * mm, "end": v(-229.37, 51.15) * mm});
            skLineSegment(sketch, "E830", {"start": v(-229.37, 51.15) * mm, "end": v(-228.98, 50.8) * mm});
            skLineSegment(sketch, "E831", {"start": v(-250.54, -73.03) * mm, "end": v(-230.54, -53.03) * mm});
            skLineSegment(sketch, "E832", {"start": v(-53.5, 13.97) * mm, "end": v(-53.01, 14.14) * mm});
            skLineSegment(sketch, "E833", {"start": v(-54.02, 13.87) * mm, "end": v(-53.5, 13.97) * mm});
            skLineSegment(sketch, "E834", {"start": v(-54.54, 13.83) * mm, "end": v(-54.02, 13.87) * mm});
            skLineSegment(sketch, "E835", {"start": v(-160.54, 34.97) * mm, "end": v(-160.54, 24.97) * mm});
            skLineSegment(sketch, "E836", {"start": v(-230.54, 34.97) * mm, "end": v(-230.54, 24.97) * mm});
            skLineSegment(sketch, "E837", {"start": v(-230.54, 53.98) * mm, "end": v(-230.54, 76.98) * mm});
            skLineSegment(sketch, "E838", {"start": v(-37.54, -80.03) * mm, "end": v(-35.47, -80.03) * mm});
            skLineSegment(sketch, "E839", {"start": v(-228.54, 50.51) * mm, "end": v(-228.07, 50.28) * mm});
            skLineSegment(sketch, "E840", {"start": v(-228.98, 50.8) * mm, "end": v(-228.54, 50.51) * mm});
            skLineSegment(sketch, "E841", {"start": v(-230.4, 52.94) * mm, "end": v(-230.24, 52.44) * mm});
            skLineSegment(sketch, "E842", {"start": v(-230.54, 53.98) * mm, "end": v(-230.5, 53.45) * mm});
            skLineSegment(sketch, "E843", {"start": v(-224.02, 80.94) * mm, "end": v(-224.54, 80.98) * mm});
            skLineSegment(sketch, "E844", {"start": v(-223.5, 80.84) * mm, "end": v(-224.02, 80.94) * mm});
            skLineSegment(sketch, "E845", {"start": v(-222.1, 80.15) * mm, "end": v(-222.54, 80.44) * mm});
            skLineSegment(sketch, "E846", {"start": v(-221.71, 79.8) * mm, "end": v(-222.1, 80.15) * mm});
            skLineSegment(sketch, "E847", {"start": v(-221.08, 78.98) * mm, "end": v(-221.37, 79.41) * mm});
            skLineSegment(sketch, "E848", {"start": v(-223.5, -19.9) * mm, "end": v(-223.01, -19.73) * mm});
            skLineSegment(sketch, "E849", {"start": v(-33.54, -80.03) * mm, "end": v(-30.54, -77.03) * mm});
            skLineSegment(sketch, "E850", {"start": v(-220.85, -17.56) * mm, "end": v(-220.68, -17.07) * mm});
            skLineSegment(sketch, "E851", {"start": v(-220.68, -17.07) * mm, "end": v(-220.58, -16.55) * mm});
            skLineSegment(sketch, "E852", {"start": v(-220.58, -16.55) * mm, "end": v(-220.54, -16.03) * mm});
            skLineSegment(sketch, "E853", {"start": v(-218.54, 114.97) * mm, "end": v(-62.54, 114.97) * mm});
            skLineSegment(sketch, "E854", {"start": v(-223.01, -19.73) * mm, "end": v(-222.54, -19.5) * mm});
            skLineSegment(sketch, "E855", {"start": v(-222.54, -19.5) * mm, "end": v(-222.1, -19.2) * mm});
            skLineSegment(sketch, "E856", {"start": v(-222.1, -19.2) * mm, "end": v(-221.71, -18.86) * mm});
            skLineSegment(sketch, "E857", {"start": v(-220.54, 24.97) * mm, "end": v(-220.54, 34.97) * mm});
            skLineSegment(sketch, "E858", {"start": v(-230.54, 24.97) * mm, "end": v(-240.54, 14.97) * mm});
            skLineSegment(sketch, "E859", {"start": v(-57.58, 13.97) * mm, "end": v(-57.06, 13.87) * mm});
            skLineSegment(sketch, "E860", {"start": v(-57.06, 13.87) * mm, "end": v(-56.54, 13.83) * mm});
            skLineSegment(sketch, "E861", {"start": v(-54.54, 13.83) * mm, "end": v(-56.54, 13.83) * mm});
            skLineSegment(sketch, "E862", {"start": v(-221.71, -18.86) * mm, "end": v(-221.37, -18.47) * mm});
            skLineSegment(sketch, "E863", {"start": v(-221.37, -18.47) * mm, "end": v(-221.08, -18.03) * mm});
            skLineSegment(sketch, "E864", {"start": v(-221.08, -18.03) * mm, "end": v(-220.85, -17.56) * mm});
            skLineSegment(sketch, "E865", {"start": v(-180.54, 54.97) * mm, "end": v(-160.54, 34.97) * mm});
            skLineSegment(sketch, "E866", {"start": v(-230.4, -17.07) * mm, "end": v(-230.24, -17.56) * mm});
            skLineSegment(sketch, "E867", {"start": v(-59.72, 15.4) * mm, "end": v(-59.37, 15) * mm});
            skLineSegment(sketch, "E868", {"start": v(-240.54, 44.97) * mm, "end": v(-230.54, 34.97) * mm});
            skLineSegment(sketch, "E869", {"start": v(-223.01, 10.66) * mm, "end": v(-223.5, 10.83) * mm});
            skLineSegment(sketch, "E870", {"start": v(-223.5, 10.83) * mm, "end": v(-224.02, 10.93) * mm});
            skLineSegment(sketch, "E871", {"start": v(-224.02, 10.93) * mm, "end": v(-224.54, 10.97) * mm});
            skLineSegment(sketch, "E872", {"start": v(-250.54, 136.97) * mm, "end": v(-250.54, 134.97) * mm});
            skLineSegment(sketch, "E873", {"start": v(-250.54, -77.03) * mm, "end": v(-247.54, -80.03) * mm});
            skLineSegment(sketch, "E874", {"start": v(-60.54, 17.83) * mm, "end": v(-60.5, 17.3) * mm});
            skLineSegment(sketch, "E875", {"start": v(-226.54, 10.97) * mm, "end": v(-227.06, 10.93) * mm});
            skLineSegment(sketch, "E876", {"start": v(-227.06, 10.93) * mm, "end": v(-227.58, 10.83) * mm});
            skLineSegment(sketch, "E877", {"start": v(-230.54, -16.03) * mm, "end": v(-230.54, 6.97) * mm});
            skLineSegment(sketch, "E878", {"start": v(-230.54, -16.03) * mm, "end": v(-230.5, -16.55) * mm});
            skLineSegment(sketch, "E879", {"start": v(-230.5, -16.55) * mm, "end": v(-230.4, -17.07) * mm});
            skLineSegment(sketch, "E880", {"start": v(-50.54, 6.97) * mm, "end": v(-70.54, -13.03) * mm});
            skLineSegment(sketch, "E881", {"start": v(-30.54, 136.97) * mm, "end": v(-33.54, 139.97) * mm});
            skLineSegment(sketch, "E882", {"start": v(-240.54, 82.97) * mm, "end": v(-240.54, 44.97) * mm});
            skLineSegment(sketch, "E883", {"start": v(-224.54, -20.03) * mm, "end": v(-224.02, -20) * mm});
            skLineSegment(sketch, "E884", {"start": v(-227.58, -19.9) * mm, "end": v(-227.06, -20) * mm});
            skLineSegment(sketch, "E885", {"start": v(-227.06, -20) * mm, "end": v(-226.54, -20.03) * mm});
            skLineSegment(sketch, "E886", {"start": v(-30.54, -73.03) * mm, "end": v(-50.54, -53.03) * mm});
            skLineSegment(sketch, "E887", {"start": v(-50.54, -53.03) * mm, "end": v(-70.54, -33.03) * mm});
            skLineSegment(sketch, "E888", {"start": v(-70.54, -33.03) * mm, "end": v(-70.54, -13.03) * mm});
            skLineSegment(sketch, "E889", {"start": v(-50.58, 41.35) * mm, "end": v(-50.68, 41.87) * mm});
            skLineSegment(sketch, "E890", {"start": v(-50.54, 40.83) * mm, "end": v(-50.58, 41.35) * mm});
            skLineSegment(sketch, "E891", {"start": v(-222.54, 10.43) * mm, "end": v(-223.01, 10.66) * mm});
            skLineSegment(sketch, "E892", {"start": v(-222.1, 10.14) * mm, "end": v(-222.54, 10.43) * mm});
            skLineSegment(sketch, "E893", {"start": v(-221.71, 9.8) * mm, "end": v(-222.1, 10.14) * mm});
            skLineSegment(sketch, "E894", {"start": v(-37.54, 139.97) * mm, "end": v(-60.54, 116.97) * mm});
            skLineSegment(sketch, "E895", {"start": v(-180.54, 4.97) * mm, "end": v(-200.54, 4.97) * mm});
            skLineSegment(sketch, "E896", {"start": v(-247.54, 139.97) * mm, "end": v(-250.54, 136.97) * mm});
            skLineSegment(sketch, "E897", {"start": v(-33.54, 139.97) * mm, "end": v(-37.54, 139.97) * mm});
            skLineSegment(sketch, "E898", {"start": v(-245.54, 139.97) * mm, "end": v(-245.47, 139.97) * mm});
            skLineSegment(sketch, "E899", {"start": v(-243.54, -80.03) * mm, "end": v(-245.47, -80.03) * mm});
            skLineSegment(sketch, "E900", {"start": v(-30.54, 132.97) * mm, "end": v(-70.54, 92.97) * mm});
            skLineSegment(sketch, "E901", {"start": v(-59.37, 43.66) * mm, "end": v(-59.72, 43.27) * mm});
            skLineSegment(sketch, "E902", {"start": v(-58.98, 44) * mm, "end": v(-59.37, 43.66) * mm});
            skLineSegment(sketch, "E903", {"start": v(-58.07, 44.53) * mm, "end": v(-58.54, 44.3) * mm});
            skLineSegment(sketch, "E904", {"start": v(-57.58, 44.7) * mm, "end": v(-58.07, 44.53) * mm});
            skLineSegment(sketch, "E905", {"start": v(-52.1, 14.66) * mm, "end": v(-51.71, 15) * mm});
            skLineSegment(sketch, "E906", {"start": v(-220.85, 8.5) * mm, "end": v(-221.08, 8.97) * mm});
            skLineSegment(sketch, "E907", {"start": v(-221.08, 8.97) * mm, "end": v(-221.37, 9.4) * mm});
            skLineSegment(sketch, "E908", {"start": v(-30.54, -73.03) * mm, "end": v(-30.54, -77.03) * mm});
            skLineSegment(sketch, "E909", {"start": v(-230.54, -53.03) * mm, "end": v(-230.54, -33.03) * mm});
            skLineSegment(sketch, "E910", {"start": v(-245.54, 139.97) * mm, "end": v(-247.54, 139.97) * mm});
            skLineSegment(sketch, "E911", {"start": v(-70.54, 72.97) * mm, "end": v(-70.54, 92.97) * mm});
            skLineSegment(sketch, "E912", {"start": v(-50.54, 52.97) * mm, "end": v(-70.54, 72.97) * mm});
            skLineSegment(sketch, "E913", {"start": v(-50.58, 17.3) * mm, "end": v(-50.54, 17.83) * mm});
            skLineSegment(sketch, "E914", {"start": v(-50.54, 40.83) * mm, "end": v(-50.54, 17.83) * mm});
            skLineSegment(sketch, "E915", {"start": v(-54.02, 44.8) * mm, "end": v(-54.54, 44.83) * mm});
            skLineSegment(sketch, "E916", {"start": v(-53.5, 44.7) * mm, "end": v(-54.02, 44.8) * mm});
            skLineSegment(sketch, "E917", {"start": v(-218.54, -55.03) * mm, "end": v(-62.54, -55.03) * mm});
            skLineSegment(sketch, "E918", {"start": v(-230.24, 8.5) * mm, "end": v(-230.4, 8) * mm});
            skLineSegment(sketch, "E919", {"start": v(-230.4, 8) * mm, "end": v(-230.5, 7.5) * mm});
            skLineSegment(sketch, "E920", {"start": v(-230.5, 7.5) * mm, "end": v(-230.54, 6.97) * mm});
            skLineSegment(sketch, "E921", {"start": v(-226.54, 10.97) * mm, "end": v(-224.54, 10.97) * mm});
            skLineSegment(sketch, "E922", {"start": v(-37.54, -80.03) * mm, "end": v(-62.54, -55.03) * mm});
            skLineSegment(sketch, "E923", {"start": v(-40.54, 42.97) * mm, "end": v(-50.54, 52.97) * mm});
            skLineSegment(sketch, "E924", {"start": v(-30.54, 135.97) * mm, "end": v(-30.54, 136.97) * mm});
            skLineSegment(sketch, "E925", {"start": v(-243.54, 139.97) * mm, "end": v(-218.54, 114.97) * mm});
            skLineSegment(sketch, "E926", {"start": v(-40.54, 42.97) * mm, "end": v(-40.54, 16.97) * mm});
            skLineSegment(sketch, "E927", {"start": v(-35.47, -80.03) * mm, "end": v(-33.54, -80.03) * mm});
            skLineSegment(sketch, "E928", {"start": v(-240.54, 14.97) * mm, "end": v(-240.54, -23.03) * mm});
            skLineSegment(sketch, "E929", {"start": v(-245.47, 139.97) * mm, "end": v(-243.54, 139.97) * mm});
            skLineSegment(sketch, "E930", {"start": v(-245.47, -80.03) * mm, "end": v(-247.54, -80.03) * mm});
            skLineSegment(sketch, "E931", {"start": v(-30.54, 135.97) * mm, "end": v(-30.54, 132.97) * mm});
            skLineSegment(sketch, "E932", {"start": v(-250.54, 132.97) * mm, "end": v(-230.54, 112.97) * mm});
            skLineSegment(sketch, "E933", {"start": v(-60.54, 116.97) * mm, "end": v(-62.54, 114.97) * mm});
            skLineSegment(sketch, "E934", {"start": v(-100.54, 76.97) * mm, "end": v(-102.54, 74.97) * mm});
            skLineSegment(sketch, "E935", {"start": v(-102.54, 74.97) * mm, "end": v(-112.54, 64.97) * mm});
            skLineSegment(sketch, "E936", {"start": v(-72.54, 104.97) * mm, "end": v(-100.54, 76.97) * mm});
            skLineSegment(sketch, "E937", {"start": v(-112.47, 64.97) * mm, "end": v(-112.54, 64.97) * mm});
            skLineSegment(sketch, "E938", {"start": v(-112.54, 64.97) * mm, "end": v(-168.54, 64.97) * mm});
            skLineSegment(sketch, "E939", {"start": v(-208.54, 104.97) * mm, "end": v(-168.54, 64.97) * mm});
            skLineSegment(sketch, "E940", {"start": v(-160.54, 24.97) * mm, "end": v(-180.54, 4.97) * mm});
            skLineSegment(sketch, "E941", {"start": v(-180.54, 54.97) * mm, "end": v(-180.47, 54.97) * mm});
            skLineSegment(sketch, "E942", {"start": v(-220.54, 34.97) * mm, "end": v(-200.54, 54.97) * mm});
            skLineSegment(sketch, "E943", {"start": v(-200.54, 54.97) * mm, "end": v(-180.54, 54.97) * mm});
            skLineSegment(sketch, "E944", {"start": v(-200.54, 4.97) * mm, "end": v(-220.54, 24.97) * mm});
            skLineSegment(sketch, "E945", {"start": v(-70.54, 34.97) * mm, "end": v(-70.54, 24.97) * mm});
            skLineSegment(sketch, "E946", {"start": v(-120.54, 24.97) * mm, "end": v(-120.54, 34.97) * mm});
            skLineSegment(sketch, "E947", {"start": v(-80.47, 44.9) * mm, "end": v(-70.54, 34.97) * mm});
            skLineSegment(sketch, "E948", {"start": v(-90.54, 54.97) * mm, "end": v(-80.47, 44.9) * mm});
            skLineSegment(sketch, "E949", {"start": v(-70.54, 24.97) * mm, "end": v(-80.47, 15.04) * mm});
            skLineSegment(sketch, "E950", {"start": v(-100.54, 4.97) * mm, "end": v(-120.54, 24.97) * mm});
            skLineSegment(sketch, "E951", {"start": v(-120.54, 34.97) * mm, "end": v(-100.54, 54.97) * mm});
            skLineSegment(sketch, "E952", {"start": v(-80.47, 15.04) * mm, "end": v(-90.54, 4.97) * mm});
            skLineSegment(sketch, "E953", {"start": v(-100.54, 54.97) * mm, "end": v(-90.54, 54.97) * mm});
            skLineSegment(sketch, "E954", {"start": v(-80.47, 15.04) * mm, "end": v(-80.47, 14.97) * mm});
            skLineSegment(sketch, "E955", {"start": v(-90.54, 4.97) * mm, "end": v(-100.54, 4.97) * mm});
            skLineSegment(sketch, "E956", {"start": v(-72.54, -45.03) * mm, "end": v(-208.47, -45.03) * mm});
            skLineSegment(sketch, "E957", {"start": v(-112.54, -5.03) * mm, "end": v(-168.47, -5.03) * mm});
            skLineSegment(sketch, "E958", {"start": v(-72.54, 104.97) * mm, "end": v(-72.47, 104.97) * mm});
            skLineSegment(sketch, "E959", {"start": v(-50.68, 41.87) * mm, "end": v(-50.85, 42.36) * mm});
            skLineSegment(sketch, "E960", {"start": v(-60.5, 41.35) * mm, "end": v(-60.54, 40.83) * mm});
            skLineSegment(sketch, "E961", {"start": v(-59.72, 43.27) * mm, "end": v(-60, 42.83) * mm});
            skLineSegment(sketch, "E962", {"start": v(-57.06, 44.8) * mm, "end": v(-57.58, 44.7) * mm});
            skLineSegment(sketch, "E963", {"start": v(-56.54, 44.83) * mm, "end": v(-57.06, 44.8) * mm});
            skLineSegment(sketch, "E964", {"start": v(-56.54, 44.83) * mm, "end": v(-54.54, 44.83) * mm});
            skLineSegment(sketch, "E965", {"start": v(-60.54, 17.83) * mm, "end": v(-60.54, 40.83) * mm});
            skLineSegment(sketch, "E966", {"start": v(-60, 15.83) * mm, "end": v(-59.72, 15.4) * mm});
            skLineSegment(sketch, "E967", {"start": v(-60.4, 41.87) * mm, "end": v(-60.5, 41.35) * mm});
            skLineSegment(sketch, "E968", {"start": v(-60.24, 42.36) * mm, "end": v(-60.4, 41.87) * mm});
            skLineSegment(sketch, "E969", {"start": v(-60, 42.83) * mm, "end": v(-60.24, 42.36) * mm});
            skLineSegment(sketch, "E970", {"start": v(-52.1, 44) * mm, "end": v(-52.54, 44.3) * mm});
            skLineSegment(sketch, "E971", {"start": v(-52.54, 44.3) * mm, "end": v(-53.01, 44.53) * mm});
            skLineSegment(sketch, "E972", {"start": v(-53.01, 44.53) * mm, "end": v(-53.5, 44.7) * mm});
            skLineSegment(sketch, "E973", {"start": v(-50.85, 42.36) * mm, "end": v(-51.08, 42.83) * mm});
            skLineSegment(sketch, "E974", {"start": v(-59.37, 15) * mm, "end": v(-58.98, 14.66) * mm});
            skLineSegment(sketch, "E975", {"start": v(-51.08, 42.83) * mm, "end": v(-51.37, 43.27) * mm});
            skLineSegment(sketch, "E976", {"start": v(-51.37, 43.27) * mm, "end": v(-51.71, 43.66) * mm});
            skLineSegment(sketch, "E977", {"start": v(-51.71, 43.66) * mm, "end": v(-52.1, 44) * mm});
            skLineSegment(sketch, "E978", {"start": v(-51.37, 15.4) * mm, "end": v(-51.08, 15.83) * mm});
            skLineSegment(sketch, "E979", {"start": v(-58.54, 44.3) * mm, "end": v(-58.98, 44) * mm});
            skLineSegment(sketch, "E980", {"start": v(-60.24, 16.3) * mm, "end": v(-60, 15.83) * mm});
            skLineSegment(sketch, "E981", {"start": v(-51.08, 15.83) * mm, "end": v(-50.85, 16.3) * mm});
            skLineSegment(sketch, "E982", {"start": v(-50.85, 16.3) * mm, "end": v(-50.68, 16.8) * mm});
            skLineSegment(sketch, "E983", {"start": v(-50.68, 16.8) * mm, "end": v(-50.58, 17.3) * mm});
            skLineSegment(sketch, "E984", {"start": v(-51.71, 15) * mm, "end": v(-51.37, 15.4) * mm});
            skLineSegment(sketch, "E985", {"start": v(-52.54, 14.37) * mm, "end": v(-52.1, 14.66) * mm});
            skLineSegment(sketch, "E986", {"start": v(-53.01, 14.14) * mm, "end": v(-52.54, 14.37) * mm});
            skLineSegment(sketch, "E987", {"start": v(-58.54, 14.37) * mm, "end": v(-58.07, 14.14) * mm});
            skLineSegment(sketch, "E988", {"start": v(-58.98, 14.66) * mm, "end": v(-58.54, 14.37) * mm});
            skLineSegment(sketch, "E989", {"start": v(-220.58, 53.45) * mm, "end": v(-220.54, 53.98) * mm});
            skLineSegment(sketch, "E990", {"start": v(-220.68, 52.94) * mm, "end": v(-220.58, 53.45) * mm});
            skLineSegment(sketch, "E991", {"start": v(-224.02, 50) * mm, "end": v(-223.5, 50.11) * mm});
            skLineSegment(sketch, "E992", {"start": v(-222.54, 50.51) * mm, "end": v(-222.1, 50.8) * mm});
            skLineSegment(sketch, "E993", {"start": v(-222.1, 50.8) * mm, "end": v(-221.71, 51.15) * mm});
            skLineSegment(sketch, "E994", {"start": v(-221.71, 51.15) * mm, "end": v(-221.37, 51.54) * mm});
            skLineSegment(sketch, "E995", {"start": v(-220.85, 52.44) * mm, "end": v(-220.68, 52.94) * mm});
            skLineSegment(sketch, "E996", {"start": v(-221.37, 51.54) * mm, "end": v(-221.08, 51.98) * mm});
            skLineSegment(sketch, "E997", {"start": v(-221.08, 51.98) * mm, "end": v(-220.85, 52.44) * mm});
            skLineSegment(sketch, "E998", {"start": v(-228.54, 80.44) * mm, "end": v(-228.98, 80.15) * mm});
            skLineSegment(sketch, "E999", {"start": v(-228.98, 80.15) * mm, "end": v(-229.37, 79.8) * mm});
            skLineSegment(sketch, "E1000", {"start": v(-229.37, 79.8) * mm, "end": v(-229.72, 79.41) * mm});
            skLineSegment(sketch, "E1001", {"start": v(-229.72, 79.41) * mm, "end": v(-230, 78.98) * mm});
            skLineSegment(sketch, "E1002", {"start": v(-230, 78.98) * mm, "end": v(-230.24, 78.5) * mm});
            skLineSegment(sketch, "E1003", {"start": v(-230.24, 78.5) * mm, "end": v(-230.4, 78.01) * mm});
            skLineSegment(sketch, "E1004", {"start": v(-230.4, 78.01) * mm, "end": v(-230.5, 77.5) * mm});
            skLineSegment(sketch, "E1005", {"start": v(-230.5, 77.5) * mm, "end": v(-230.54, 76.98) * mm});
            skLineSegment(sketch, "E1006", {"start": v(-220.58, 77.5) * mm, "end": v(-220.68, 78.01) * mm});
            skLineSegment(sketch, "E1007", {"start": v(-220.68, 78.01) * mm, "end": v(-220.85, 78.5) * mm});
            skLineSegment(sketch, "E1008", {"start": v(-220.85, 78.5) * mm, "end": v(-221.08, 78.98) * mm});
            skLineSegment(sketch, "E1009", {"start": v(-221.37, 79.41) * mm, "end": v(-221.71, 79.8) * mm});
            skLineSegment(sketch, "E1010", {"start": v(-228.07, 50.28) * mm, "end": v(-227.58, 50.11) * mm});
            skLineSegment(sketch, "E1011", {"start": v(-227.58, 50.11) * mm, "end": v(-227.06, 50) * mm});
            skLineSegment(sketch, "E1012", {"start": v(-227.06, 50) * mm, "end": v(-226.54, 49.98) * mm});
            skLineSegment(sketch, "E1013", {"start": v(-220.54, 76.98) * mm, "end": v(-220.58, 77.5) * mm});
            skLineSegment(sketch, "E1014", {"start": v(-227.06, 80.94) * mm, "end": v(-227.58, 80.84) * mm});
            skLineSegment(sketch, "E1015", {"start": v(-230.5, 53.45) * mm, "end": v(-230.4, 52.94) * mm});
            skLineSegment(sketch, "E1016", {"start": v(-223.5, 50.11) * mm, "end": v(-223.01, 50.28) * mm});
            skLineSegment(sketch, "E1017", {"start": v(-226.54, 80.98) * mm, "end": v(-224.54, 80.98) * mm});
            skLineSegment(sketch, "E1018", {"start": v(-222.54, 80.44) * mm, "end": v(-223.01, 80.67) * mm});
            skLineSegment(sketch, "E1019", {"start": v(-224.54, 49.98) * mm, "end": v(-224.02, 50) * mm});
            skLineSegment(sketch, "E1020", {"start": v(-228.07, 80.67) * mm, "end": v(-228.54, 80.44) * mm});
            skLineSegment(sketch, "E1021", {"start": v(-228.07, -19.73) * mm, "end": v(-227.58, -19.9) * mm});
            skLineSegment(sketch, "E1022", {"start": v(-228.54, -19.5) * mm, "end": v(-228.07, -19.73) * mm});
            skLineSegment(sketch, "E1023", {"start": v(-228.98, -19.2) * mm, "end": v(-228.54, -19.5) * mm});
            skLineSegment(sketch, "E1024", {"start": v(-229.37, -18.86) * mm, "end": v(-228.98, -19.2) * mm});
            skLineSegment(sketch, "E1025", {"start": v(-224.54, -20.03) * mm, "end": v(-226.54, -20.03) * mm});
            skLineSegment(sketch, "E1026", {"start": v(-220.68, 8) * mm, "end": v(-220.85, 8.5) * mm});
            skLineSegment(sketch, "E1027", {"start": v(-220.58, 7.5) * mm, "end": v(-220.68, 8) * mm});
            skLineSegment(sketch, "E1028", {"start": v(-220.54, 6.97) * mm, "end": v(-220.58, 7.5) * mm});
            skLineSegment(sketch, "E1029", {"start": v(-224.02, -20) * mm, "end": v(-223.5, -19.9) * mm});
            skLineSegment(sketch, "E1030", {"start": v(-230.24, -17.56) * mm, "end": v(-230, -18.03) * mm});
            skLineSegment(sketch, "E1031", {"start": v(-230, -18.03) * mm, "end": v(-229.72, -18.47) * mm});
            skLineSegment(sketch, "E1032", {"start": v(-229.72, -18.47) * mm, "end": v(-229.37, -18.86) * mm});
            skLineSegment(sketch, "E1033", {"start": v(-220.54, 6.97) * mm, "end": v(-220.54, -16.03) * mm});
            skLineSegment(sketch, "E1034", {"start": v(-230, 8.97) * mm, "end": v(-230.24, 8.5) * mm});
            skLineSegment(sketch, "E1035", {"start": v(-191.55, 164.03) * mm, "end": v(-186.98, 162.9) * mm});
            skLineSegment(sketch, "E1036", {"start": v(-186.98, 162.9) * mm, "end": v(-185.72, 162.15) * mm});
            skLineSegment(sketch, "E1037", {"start": v(-185.72, 162.15) * mm, "end": v(-185.36, 161.13) * mm});
            skLineSegment(sketch, "E1038", {"start": v(-185.36, 161.13) * mm, "end": v(-185.41, 159.97) * mm});
            skLineSegment(sketch, "E1039", {"start": v(-185.41, 159.97) * mm, "end": v(-186.22, 158.9) * mm});
            skLineSegment(sketch, "E1040", {"start": v(-186.22, 158.9) * mm, "end": v(-187.44, 158.19) * mm});
            skLineSegment(sketch, "E1041", {"start": v(-187.44, 158.19) * mm, "end": v(-189.07, 158.04) * mm});
            skLineSegment(sketch, "E1042", {"start": v(-189.07, 158.04) * mm, "end": v(-191, 158.4) * mm});
            skLineSegment(sketch, "E1043", {"start": v(-191, 158.4) * mm, "end": v(-192.47, 159.3) * mm});
            skLineSegment(sketch, "E1044", {"start": v(-192.47, 159.3) * mm, "end": v(-193.38, 160.88) * mm});
            skLineSegment(sketch, "E1045", {"start": v(-193.38, 160.88) * mm, "end": v(-193.58, 161.74) * mm});
            skLineSegment(sketch, "E1046", {"start": v(-193.58, 161.74) * mm, "end": v(-197.49, 161.39) * mm});
            skLineSegment(sketch, "E1047", {"start": v(-224.67, 174.37) * mm, "end": v(-225.57, 174.67) * mm});
            skLineSegment(sketch, "E1048", {"start": v(-225.57, 174.67) * mm, "end": v(-227.07, 174.87) * mm});
            skLineSegment(sketch, "E1049", {"start": v(-227.07, 174.87) * mm, "end": v(-228.47, 174.97) * mm});
            skLineSegment(sketch, "E1050", {"start": v(-228.47, 174.97) * mm, "end": v(-236.87, 174.97) * mm});
            skLineSegment(sketch, "E1051", {"start": v(-236.87, 174.97) * mm, "end": v(-236.87, 154.97) * mm});
            skLineSegment(sketch, "E1052", {"start": v(-236.87, 154.97) * mm, "end": v(-232.87, 154.97) * mm});
            skLineSegment(sketch, "E1053", {"start": v(-232.87, 154.97) * mm, "end": v(-232.87, 171.57) * mm});
            skLineSegment(sketch, "E1054", {"start": v(-232.87, 171.57) * mm, "end": v(-228.57, 171.57) * mm});
            skLineSegment(sketch, "E1055", {"start": v(-228.57, 171.57) * mm, "end": v(-227.57, 171.37) * mm});
            skLineSegment(sketch, "E1056", {"start": v(-227.57, 171.37) * mm, "end": v(-226.77, 170.97) * mm});
            skLineSegment(sketch, "E1057", {"start": v(-226.77, 170.97) * mm, "end": v(-226.17, 170.37) * mm});
            skLineSegment(sketch, "E1058", {"start": v(-226.17, 170.37) * mm, "end": v(-225.87, 169.77) * mm});
            skLineSegment(sketch, "E1059", {"start": v(-223.74, 154.97) * mm, "end": v(-228.98, 162.57) * mm});
            skLineSegment(sketch, "E1060", {"start": v(-204.77, 163.02) * mm, "end": v(-204.9, 161.3) * mm});
            skLineSegment(sketch, "E1061", {"start": v(-204.9, 161.3) * mm, "end": v(-205.26, 159.57) * mm});
            skLineSegment(sketch, "E1062", {"start": v(-205.26, 159.57) * mm, "end": v(-206.16, 158.69) * mm});
            skLineSegment(sketch, "E1063", {"start": v(-206.16, 158.69) * mm, "end": v(-207.36, 158.17) * mm});
            skLineSegment(sketch, "E1064", {"start": v(-207.36, 158.17) * mm, "end": v(-208.8, 158.07) * mm});
            skLineSegment(sketch, "E1065", {"start": v(-208.8, 158.07) * mm, "end": v(-210.3, 158.32) * mm});
            skLineSegment(sketch, "E1066", {"start": v(-210.3, 158.32) * mm, "end": v(-211.52, 159.05) * mm});
            skLineSegment(sketch, "E1067", {"start": v(-211.52, 159.05) * mm, "end": v(-212.33, 160.28) * mm});
            skLineSegment(sketch, "E1068", {"start": v(-212.33, 160.28) * mm, "end": v(-212.65, 162.18) * mm});
            skLineSegment(sketch, "E1069", {"start": v(-212.65, 162.18) * mm, "end": v(-212.62, 170.14) * mm});
            skLineSegment(sketch, "E1070", {"start": v(-212.62, 170.14) * mm, "end": v(-212.62, 174.96) * mm});
            skLineSegment(sketch, "E1071", {"start": v(-212.62, 174.96) * mm, "end": v(-216.67, 174.97) * mm});
            skLineSegment(sketch, "E1072", {"start": v(-179.93, 154.94) * mm, "end": v(-172.06, 174.89) * mm});
            skLineSegment(sketch, "E1073", {"start": v(-186.63, 166.87) * mm, "end": v(-190.18, 167.78) * mm});
            skLineSegment(sketch, "E1074", {"start": v(-190.18, 167.78) * mm, "end": v(-192.52, 168.8) * mm});
            skLineSegment(sketch, "E1075", {"start": v(-192.52, 168.8) * mm, "end": v(-192.82, 169.7) * mm});
            skLineSegment(sketch, "E1076", {"start": v(-192.82, 169.7) * mm, "end": v(-192.82, 170.47) * mm});
            skLineSegment(sketch, "E1077", {"start": v(-192.82, 170.47) * mm, "end": v(-192.35, 171.18) * mm});
            skLineSegment(sketch, "E1078", {"start": v(-192.35, 171.18) * mm, "end": v(-191.5, 171.68) * mm});
            skLineSegment(sketch, "E1079", {"start": v(-191.5, 171.68) * mm, "end": v(-190.47, 171.94) * mm});
            skLineSegment(sketch, "E1080", {"start": v(-190.47, 171.94) * mm, "end": v(-189.09, 172) * mm});
            skLineSegment(sketch, "E1081", {"start": v(-189.09, 172) * mm, "end": v(-187.8, 171.8) * mm});
            skLineSegment(sketch, "E1082", {"start": v(-187.8, 171.8) * mm, "end": v(-186.65, 171.15) * mm});
            skLineSegment(sketch, "E1083", {"start": v(-186.65, 171.15) * mm, "end": v(-186.12, 170.3) * mm});
            skLineSegment(sketch, "E1084", {"start": v(-186.12, 170.3) * mm, "end": v(-185.83, 169) * mm});
            skLineSegment(sketch, "E1085", {"start": v(-185.83, 169) * mm, "end": v(-181.76, 169.25) * mm});
            skLineSegment(sketch, "E1086", {"start": v(-183.28, 173.21) * mm, "end": v(-184.85, 174.33) * mm});
            skLineSegment(sketch, "E1087", {"start": v(-184.85, 174.33) * mm, "end": v(-186.88, 175.09) * mm});
            skLineSegment(sketch, "E1088", {"start": v(-186.88, 175.09) * mm, "end": v(-189.01, 175.24) * mm});
            skLineSegment(sketch, "E1089", {"start": v(-189.01, 175.24) * mm, "end": v(-190.69, 175.24) * mm});
            skLineSegment(sketch, "E1090", {"start": v(-190.69, 175.24) * mm, "end": v(-193.33, 174.63) * mm});
            skLineSegment(sketch, "E1091", {"start": v(-193.33, 174.63) * mm, "end": v(-195.2, 173.47) * mm});
            skLineSegment(sketch, "E1092", {"start": v(-195.2, 173.47) * mm, "end": v(-196.42, 171.64) * mm});
            skLineSegment(sketch, "E1093", {"start": v(-196.42, 171.64) * mm, "end": v(-196.83, 170.32) * mm});
            skLineSegment(sketch, "E1094", {"start": v(-196.83, 170.32) * mm, "end": v(-196.63, 168.34) * mm});
            skLineSegment(sketch, "E1095", {"start": v(-196.63, 168.34) * mm, "end": v(-195.81, 166.56) * mm});
            skLineSegment(sketch, "E1096", {"start": v(-195.81, 166.56) * mm, "end": v(-194.4, 165.3) * mm});
            skLineSegment(sketch, "E1097", {"start": v(-194.4, 165.3) * mm, "end": v(-191.55, 164.03) * mm});
            skLineSegment(sketch, "E1098", {"start": v(-213.33, 155.56) * mm, "end": v(-211.6, 154.93) * mm});
            skLineSegment(sketch, "E1099", {"start": v(-211.6, 154.93) * mm, "end": v(-208.98, 154.58) * mm});
            skLineSegment(sketch, "E1100", {"start": v(-208.98, 154.58) * mm, "end": v(-206.36, 154.78) * mm});
            skLineSegment(sketch, "E1101", {"start": v(-206.36, 154.78) * mm, "end": v(-204.25, 155.44) * mm});
            skLineSegment(sketch, "E1102", {"start": v(-204.25, 155.44) * mm, "end": v(-202.93, 156.3) * mm});
            skLineSegment(sketch, "E1103", {"start": v(-202.93, 156.3) * mm, "end": v(-201.78, 157.42) * mm});
            skLineSegment(sketch, "E1104", {"start": v(-201.78, 157.42) * mm, "end": v(-201.05, 159.47) * mm});
            skLineSegment(sketch, "E1105", {"start": v(-201.05, 159.47) * mm, "end": v(-200.7, 162.23) * mm});
            skLineSegment(sketch, "E1106", {"start": v(-200.7, 162.23) * mm, "end": v(-200.7, 166.15) * mm});
            skLineSegment(sketch, "E1107", {"start": v(-200.7, 166.15) * mm, "end": v(-200.73, 174.96) * mm});
            skLineSegment(sketch, "E1108", {"start": v(-200.73, 174.96) * mm, "end": v(-204.8, 174.96) * mm});
            skLineSegment(sketch, "E1109", {"start": v(-204.8, 174.96) * mm, "end": v(-204.77, 163.02) * mm});
            skLineSegment(sketch, "E1110", {"start": v(-246.17, 171.37) * mm, "end": v(-245.37, 170.97) * mm});
            skLineSegment(sketch, "E1111", {"start": v(-245.37, 170.97) * mm, "end": v(-244.77, 170.37) * mm});
            skLineSegment(sketch, "E1112", {"start": v(-244.77, 170.37) * mm, "end": v(-244.47, 169.77) * mm});
            skLineSegment(sketch, "E1113", {"start": v(-244.47, 169.77) * mm, "end": v(-244.27, 168.97) * mm});
            skLineSegment(sketch, "E1114", {"start": v(-244.27, 168.97) * mm, "end": v(-244.37, 168.07) * mm});
            skLineSegment(sketch, "E1115", {"start": v(-244.37, 168.07) * mm, "end": v(-244.77, 167.27) * mm});
            skLineSegment(sketch, "E1116", {"start": v(-244.77, 167.27) * mm, "end": v(-245.27, 166.67) * mm});
            skLineSegment(sketch, "E1117", {"start": v(-245.27, 166.67) * mm, "end": v(-246.17, 166.17) * mm});
            skLineSegment(sketch, "E1118", {"start": v(-246.17, 166.17) * mm, "end": v(-247.07, 165.97) * mm});
            skLineSegment(sketch, "E1119", {"start": v(-247.07, 165.97) * mm, "end": v(-248.37, 165.97) * mm});
            skLineSegment(sketch, "E1120", {"start": v(-248.37, 165.97) * mm, "end": v(-249.97, 165.97) * mm});
            skLineSegment(sketch, "E1121", {"start": v(-241.97, 173.47) * mm, "end": v(-243.27, 174.37) * mm});
            skLineSegment(sketch, "E1122", {"start": v(-243.27, 174.37) * mm, "end": v(-244.17, 174.67) * mm});
            skLineSegment(sketch, "E1123", {"start": v(-244.17, 174.67) * mm, "end": v(-245.67, 174.87) * mm});
            skLineSegment(sketch, "E1124", {"start": v(-245.67, 174.87) * mm, "end": v(-247.07, 174.97) * mm});
            skLineSegment(sketch, "E1125", {"start": v(-247.07, 174.97) * mm, "end": v(-255.47, 174.97) * mm});
            skLineSegment(sketch, "E1126", {"start": v(-225.87, 169.77) * mm, "end": v(-225.67, 168.97) * mm});
            skLineSegment(sketch, "E1127", {"start": v(-225.67, 168.97) * mm, "end": v(-225.77, 168.07) * mm});
            skLineSegment(sketch, "E1128", {"start": v(-225.77, 168.07) * mm, "end": v(-226.17, 167.27) * mm});
            skLineSegment(sketch, "E1129", {"start": v(-226.17, 167.27) * mm, "end": v(-226.67, 166.67) * mm});
            skLineSegment(sketch, "E1130", {"start": v(-226.67, 166.67) * mm, "end": v(-227.57, 166.17) * mm});
            skLineSegment(sketch, "E1131", {"start": v(-227.57, 166.17) * mm, "end": v(-228.47, 165.97) * mm});
            skLineSegment(sketch, "E1132", {"start": v(-228.47, 165.97) * mm, "end": v(-229.77, 165.97) * mm});
            skLineSegment(sketch, "E1133", {"start": v(-172.06, 174.89) * mm, "end": v(-167.8, 174.89) * mm});
            skLineSegment(sketch, "E1134", {"start": v(-167.8, 174.89) * mm, "end": v(-159.88, 155) * mm});
            skLineSegment(sketch, "E1135", {"start": v(-159.88, 155) * mm, "end": v(-164.2, 155.04) * mm});
            skLineSegment(sketch, "E1136", {"start": v(-179.93, 154.94) * mm, "end": v(-175.57, 154.94) * mm});
            skLineSegment(sketch, "E1137", {"start": v(-175.57, 154.94) * mm, "end": v(-170.03, 170.22) * mm});
            skLineSegment(sketch, "E1138", {"start": v(-170.03, 170.22) * mm, "end": v(-167.24, 162.9) * mm});
            skLineSegment(sketch, "E1139", {"start": v(-167.24, 162.9) * mm, "end": v(-171.6, 162.86) * mm});
            skLineSegment(sketch, "E1140", {"start": v(-171.6, 162.86) * mm, "end": v(-172.77, 159.56) * mm});
            skLineSegment(sketch, "E1141", {"start": v(-172.77, 159.56) * mm, "end": v(-165.92, 159.56) * mm});
            skLineSegment(sketch, "E1142", {"start": v(-165.92, 159.56) * mm, "end": v(-164.2, 155.04) * mm});
            skLineSegment(sketch, "E1143", {"start": v(-181.76, 169.25) * mm, "end": v(-182.16, 171.23) * mm});
            skLineSegment(sketch, "E1144", {"start": v(-182.16, 171.23) * mm, "end": v(-183.28, 173.21) * mm});
            skLineSegment(sketch, "E1145", {"start": v(-197.49, 161.39) * mm, "end": v(-196.88, 159.1) * mm});
            skLineSegment(sketch, "E1146", {"start": v(-196.88, 159.1) * mm, "end": v(-195.4, 156.72) * mm});
            skLineSegment(sketch, "E1147", {"start": v(-195.4, 156.72) * mm, "end": v(-192.92, 155.2) * mm});
            skLineSegment(sketch, "E1148", {"start": v(-192.92, 155.2) * mm, "end": v(-190.28, 154.64) * mm});
            skLineSegment(sketch, "E1149", {"start": v(-190.28, 154.64) * mm, "end": v(-187.75, 154.74) * mm});
            skLineSegment(sketch, "E1150", {"start": v(-187.75, 154.74) * mm, "end": v(-184.45, 155.55) * mm});
            skLineSegment(sketch, "E1151", {"start": v(-184.45, 155.55) * mm, "end": v(-182.32, 157.43) * mm});
            skLineSegment(sketch, "E1152", {"start": v(-182.32, 157.43) * mm, "end": v(-181.3, 159.36) * mm});
            skLineSegment(sketch, "E1153", {"start": v(-181.3, 159.36) * mm, "end": v(-181.3, 161.9) * mm});
            skLineSegment(sketch, "E1154", {"start": v(-181.3, 161.9) * mm, "end": v(-182.01, 163.92) * mm});
            skLineSegment(sketch, "E1155", {"start": v(-182.01, 163.92) * mm, "end": v(-183.63, 165.7) * mm});
            skLineSegment(sketch, "E1156", {"start": v(-183.63, 165.7) * mm, "end": v(-186.63, 166.87) * mm});
            skLineSegment(sketch, "E1157", {"start": v(-249.97, 165.97) * mm, "end": v(-249.97, 162.57) * mm});
            skLineSegment(sketch, "E1158", {"start": v(-249.97, 162.57) * mm, "end": v(-247.07, 162.57) * mm});
            skLineSegment(sketch, "E1159", {"start": v(-247.07, 162.57) * mm, "end": v(-245.37, 162.67) * mm});
            skLineSegment(sketch, "E1160", {"start": v(-245.37, 162.67) * mm, "end": v(-243.37, 163.27) * mm});
            skLineSegment(sketch, "E1161", {"start": v(-243.37, 163.27) * mm, "end": v(-241.87, 164.27) * mm});
            skLineSegment(sketch, "E1162", {"start": v(-241.87, 164.27) * mm, "end": v(-240.97, 165.37) * mm});
            skLineSegment(sketch, "E1163", {"start": v(-240.97, 165.37) * mm, "end": v(-240.37, 166.67) * mm});
            skLineSegment(sketch, "E1164", {"start": v(-240.37, 166.67) * mm, "end": v(-240.17, 167.97) * mm});
            skLineSegment(sketch, "E1165", {"start": v(-240.17, 167.97) * mm, "end": v(-240.17, 169.67) * mm});
            skLineSegment(sketch, "E1166", {"start": v(-240.17, 169.67) * mm, "end": v(-240.47, 171.17) * mm});
            skLineSegment(sketch, "E1167", {"start": v(-240.47, 171.17) * mm, "end": v(-241.17, 172.47) * mm});
            skLineSegment(sketch, "E1168", {"start": v(-241.17, 172.47) * mm, "end": v(-241.97, 173.47) * mm});
            skLineSegment(sketch, "E1169", {"start": v(-223.74, 154.97) * mm, "end": v(-218.86, 154.97) * mm});
            skLineSegment(sketch, "E1170", {"start": v(-218.86, 154.97) * mm, "end": v(-223.04, 161.62) * mm});
            skLineSegment(sketch, "E1171", {"start": v(-223.04, 161.62) * mm, "end": v(-224, 162.58) * mm});
            skLineSegment(sketch, "E1172", {"start": v(-224, 162.58) * mm, "end": v(-224.77, 163.27) * mm});
            skLineSegment(sketch, "E1173", {"start": v(-231.37, 162.57) * mm, "end": v(-228.98, 162.57) * mm});
            skLineSegment(sketch, "E1174", {"start": v(-216.67, 174.97) * mm, "end": v(-216.71, 163.98) * mm});
            skLineSegment(sketch, "E1175", {"start": v(-216.71, 163.98) * mm, "end": v(-216.5, 160.36) * mm});
            skLineSegment(sketch, "E1176", {"start": v(-216.5, 160.36) * mm, "end": v(-216.1, 158.7) * mm});
            skLineSegment(sketch, "E1177", {"start": v(-216.1, 158.7) * mm, "end": v(-215.51, 157.5) * mm});
            skLineSegment(sketch, "E1178", {"start": v(-215.51, 157.5) * mm, "end": v(-214.58, 156.4) * mm});
            skLineSegment(sketch, "E1179", {"start": v(-214.58, 156.4) * mm, "end": v(-213.33, 155.56) * mm});
            skLineSegment(sketch, "E1180", {"start": v(-229.77, 165.97) * mm, "end": v(-231.37, 165.97) * mm});
            skLineSegment(sketch, "E1181", {"start": v(-231.37, 165.97) * mm, "end": v(-231.37, 162.57) * mm});
            skLineSegment(sketch, "E1182", {"start": v(-224.77, 163.27) * mm, "end": v(-223.27, 164.27) * mm});
            skLineSegment(sketch, "E1183", {"start": v(-223.27, 164.27) * mm, "end": v(-222.37, 165.37) * mm});
            skLineSegment(sketch, "E1184", {"start": v(-222.37, 165.37) * mm, "end": v(-221.77, 166.67) * mm});
            skLineSegment(sketch, "E1185", {"start": v(-221.77, 166.67) * mm, "end": v(-221.57, 167.97) * mm});
            skLineSegment(sketch, "E1186", {"start": v(-221.57, 167.97) * mm, "end": v(-221.57, 169.67) * mm});
            skLineSegment(sketch, "E1187", {"start": v(-221.57, 169.67) * mm, "end": v(-221.87, 171.17) * mm});
            skLineSegment(sketch, "E1188", {"start": v(-221.87, 171.17) * mm, "end": v(-222.57, 172.47) * mm});
            skLineSegment(sketch, "E1189", {"start": v(-222.57, 172.47) * mm, "end": v(-223.37, 173.47) * mm});
            skLineSegment(sketch, "E1190", {"start": v(-223.37, 173.47) * mm, "end": v(-224.67, 174.37) * mm});
            skLineSegment(sketch, "E1191", {"start": v(-255.47, 174.97) * mm, "end": v(-255.47, 154.97) * mm});
            skLineSegment(sketch, "E1192", {"start": v(-255.47, 154.97) * mm, "end": v(-251.47, 154.97) * mm});
            skLineSegment(sketch, "E1193", {"start": v(-251.47, 154.97) * mm, "end": v(-251.47, 171.57) * mm});
            skLineSegment(sketch, "E1194", {"start": v(-251.47, 171.57) * mm, "end": v(-247.17, 171.57) * mm});
            skLineSegment(sketch, "E1195", {"start": v(-247.17, 171.57) * mm, "end": v(-246.17, 171.37) * mm});
            skLineSegment(sketch, "E1196", {"start": v(-215.47, -151.03) * mm, "end": v(-215.47, -165.1) * mm});
            skLineSegment(sketch, "E1197", {"start": v(-205.47, -165.1) * mm, "end": v(-205.47, -151.03) * mm});
            skLineSegment(sketch, "E1198", {"start": v(-215.47, -151.03) * mm, "end": v(-215.47, -150.03) * mm});
            skLineSegment(sketch, "E1199", {"start": v(-205.47, -150.03) * mm, "end": v(-200.47, -145.03) * mm});
            skLineSegment(sketch, "E1200", {"start": v(-205.47, -151.03) * mm, "end": v(-205.47, -150.03) * mm});
            skLineSegment(sketch, "E1201", {"start": v(-45.47, -151.03) * mm, "end": v(-45.47, -165.1) * mm});
            skLineSegment(sketch, "E1202", {"start": v(-35.47, -165.1) * mm, "end": v(-35.47, -151.03) * mm});
            skLineSegment(sketch, "E1203", {"start": v(-45.47, -150.03) * mm, "end": v(-50.47, -145.03) * mm});
            skLineSegment(sketch, "E1204", {"start": v(-45.47, -151.03) * mm, "end": v(-45.47, -150.03) * mm});
            skLineSegment(sketch, "E1205", {"start": v(-35.47, -151.03) * mm, "end": v(-35.47, -150.03) * mm});
            skLineSegment(sketch, "E1206", {"start": v(-230.47, -145.03) * mm, "end": v(-220.47, -145.03) * mm});
            skLineSegment(sketch, "E1207", {"start": v(-220.47, -145.03) * mm, "end": v(-215.47, -150.03) * mm});
            skLineSegment(sketch, "E1208", {"start": v(-20.47, -145.03) * mm, "end": v(-30.47, -145.03) * mm});
            skLineSegment(sketch, "E1209", {"start": v(-35.47, -150.03) * mm, "end": v(-30.47, -145.03) * mm});
            skCircle(sketch, "E1210", {"center": v(29.54, -145.04) * mm, "radius": 1.8 * mm});
            skCircle(sketch, "E1211", {"center": v(49.52, -145.09) * mm, "radius": 1.8 * mm});
            skCircle(sketch, "E1212", {"center": v(39.53, -165.06) * mm, "radius": 1.8 * mm});
            skCircle(sketch, "E1213", {"center": v(16.53, -160.03) * mm, "radius": 1.8 * mm});
            skCircle(sketch, "E1214", {"center": v(-290.5, -165.02) * mm, "radius": 1.8 * mm});
            skCircle(sketch, "E1215", {"center": v(-267.49, -160.02) * mm, "radius": 1.8 * mm});
            skCircle(sketch, "E1216", {"center": v(-280.49, -145.01) * mm, "radius": 1.8 * mm});
            skCircle(sketch, "E1217", {"center": v(-300.5, -145.01) * mm, "radius": 1.8 * mm});
            skArc(sketch, "E1218", {"start": v(-215.47, -165.1) * mm, "mid": v(-210.47, -170.04) * mm, "end": v(-205.47, -165.1) * mm});
            skArc(sketch, "E1219", {"start": v(-45.47, -165.1) * mm, "mid": v(-40.47, -170.04) * mm, "end": v(-35.47, -165.1) * mm});
            skCircle(sketch, "E1220", {"center": v(-245.05, -74.52) * mm, "radius": 1.8 * mm});
            skCircle(sketch, "E1221", {"center": v(-36.03, -74.54) * mm, "radius": 1.8 * mm});
            skCircle(sketch, "E1222", {"center": v(-45.54, 29.97) * mm, "radius": 1.5 * mm});
            skCircle(sketch, "E1223", {"center": v(-65.54, 29.97) * mm, "radius": 1.5 * mm});
            skCircle(sketch, "E1224", {"center": v(-140.5, 49.95) * mm, "radius": 1.8 * mm});
            skCircle(sketch, "E1225", {"center": v(-140.5, 8.97) * mm, "radius": 1.8 * mm});
            skCircle(sketch, "E1226", {"center": v(-215.54, -5.03) * mm, "radius": 1.5 * mm});
            skCircle(sketch, "E1227", {"center": v(-235.54, -5.03) * mm, "radius": 1.5 * mm});
            skCircle(sketch, "E1228", {"center": v(-215.54, 64.97) * mm, "radius": 1.5 * mm});
            skCircle(sketch, "E1229", {"center": v(-245.05, 134.48) * mm, "radius": 1.8 * mm});
            skCircle(sketch, "E1230", {"center": v(-36.03, 134.48) * mm, "radius": 1.8 * mm});
            skCircle(sketch, "E1231", {"center": v(-267.45, -0.03) * mm, "radius": 1.8 * mm});
            skCircle(sketch, "E1232", {"center": v(-267.45, 154.96) * mm, "radius": 1.8 * mm});
            skCircle(sketch, "E1233", {"center": v(-280.45, 174.98) * mm, "radius": 1.8 * mm});
            skCircle(sketch, "E1234", {"center": v(-300.47, 174.98) * mm, "radius": 1.8 * mm});
            skCircle(sketch, "E1235", {"center": v(16.54, 154.96) * mm, "radius": 1.8 * mm});
            skCircle(sketch, "E1236", {"center": v(29.53, 174.96) * mm, "radius": 1.8 * mm});
            skCircle(sketch, "E1237", {"center": v(49.5, 175) * mm, "radius": 1.8 * mm});
            skCircle(sketch, "E1238", {"center": v(16.53, -0.03) * mm, "radius": 1.8 * mm});
            skCircle(sketch, "E1239", {"center": v(9.53, -179.03) * mm, "radius": 1.8 * mm});
            skCircle(sketch, "E1240", {"center": v(-80.47, -179.03) * mm, "radius": 1.8 * mm});
            skCircle(sketch, "E1241", {"center": v(-170.47, -179.03) * mm, "radius": 1.8 * mm});
            skCircle(sketch, "E1242", {"center": v(-260.47, -179.03) * mm, "radius": 1.8 * mm});
            skPoint(sketch, "E1243", {"position": v(16.53, -143.88) * mm});
            skPoint(sketch, "E1243.positionSnap0", {"position": v(16.53, -139.38) * mm});
            skPoint(sketch, "E1243.positionSnap1", {"position": v(19.78, -143.88) * mm});
            skPoint(sketch, "E1244", {"position": v(16.53, 171.21) * mm});
            skPoint(sketch, "E1244.positionSnap0", {"position": v(13.28, 171.21) * mm});
            skPoint(sketch, "E1244.positionSnap1", {"position": v(16.53, 175.71) * mm});
            skPoint(sketch, "E1245", {"position": v(-267.47, 171.21) * mm});
            skPoint(sketch, "E1245.positionSnap0", {"position": v(-267.47, 175.71) * mm});
            skPoint(sketch, "E1245.positionSnap1", {"position": v(-270.72, 171.21) * mm});
            skPoint(sketch, "E1246", {"position": v(-267.47, -143.88) * mm});
            skPoint(sketch, "E1246.positionSnap0", {"position": v(-267.47, -148.38) * mm});
            skPoint(sketch, "E1246.positionSnap1", {"position": v(-264.22, -143.88) * mm});
            skSolve(sketch);
        }
        {
            var Q0;
            Q0=makeQuery(id+"F0.imprint","IMPRINT",FACE,{"disambiguationData":[TD([[makeQuery(id+"F0.imprint","IMPRINT",EDGE,{"derivedFrom":sQuery(id+"F0.wireOp",EDGE,"E0")}),-1.0]])]});
            var Q1;
            Q1=sQuery(id+"F0.wireOp",EDGE,"E925");
            var Q2;
            Q2=sQuery(id+"F0.wireOp",EDGE,"E914");
            var Q3;
            Q3=sQuery(id+"F0.wireOp",EDGE,"E938");
            var Q4;
            Q4=sQuery(id+"F0.wireOp",EDGE,"E911");
            var Q5;
            Q5=sQuery(id+"F0.wireOp",EDGE,"E928");
            var Q6;
            Q6=sQuery(id+"F0.wireOp",EDGE,"E900");
            var Q7;
            Q7=sQuery(id+"F0.wireOp",EDGE,"E888");
            var Q8;
            Q8=sQuery(id+"F0.wireOp",EDGE,"E831");
            var Q9;
            Q9=sQuery(id+"F0.wireOp",EDGE,"E942");
            var Q10;
            Q10=sQuery(id+"F0.wireOp",EDGE,"E949");
            var Q11;
            Q11=sQuery(id+"F0.wireOp",EDGE,"E944");
            var Q12;
            Q12=sQuery(id+"F0.wireOp",EDGE,"E951");
            var Q13;
            Q13=sQuery(id+"F0.wireOp",EDGE,"E935");
            var Q14;
            Q14=sQuery(id+"F0.wireOp",EDGE,"E5");
            var Q15;
            Q15=sQuery(id+"F0.wireOp",EDGE,"E4");
            var Q16;
            Q16=sQuery(id+"F0.wireOp",EDGE,"E3");
            var Q17;
            Q17=sQuery(id+"F0.wireOp",EDGE,"E957");
            var Q18;
            Q18=sQuery(id+"F0.wireOp",EDGE,"E948");
            var Q19;
            Q19=sQuery(id+"F0.wireOp",EDGE,"E932");
            var Q20;
            Q20=sQuery(id+"F0.wireOp",EDGE,"E909");
            var Q21;
            Q21=sQuery(id+"F0.wireOp",EDGE,"E887");
            var Q22;
            Q22=sQuery(id+"F0.wireOp",EDGE,"E858");
            var Q23;
            Q23=sQuery(id+"F0.wireOp",EDGE,"E804");
            var Q24;
            Q24=sQuery(id+"F0.wireOp",EDGE,"E880");
            var Q25;
            Q25=sQuery(id+"F0.wireOp",EDGE,"E965");
            var Q26;
            Q26=sQuery(id+"F0.wireOp",EDGE,"E952");
            var Q27;
            Q27=sQuery(id+"F0.wireOp",EDGE,"E936");
            var Q28;
            Q28=sQuery(id+"F0.wireOp",EDGE,"E956");
            var Q29;
            Q29=sQuery(id+"F0.wireOp",EDGE,"E940");
            var Q30;
            Q30=sQuery(id+"F0.wireOp",EDGE,"E947");
            var Q31;
            Q31=sQuery(id+"F0.wireOp",EDGE,"E894");
            var Q32;
            Q32=sQuery(id+"F0.wireOp",EDGE,"E926");
            var Q33;
            Q33=sQuery(id+"F0.wireOp",EDGE,"E882");
            var Q34;
            Q34=sQuery(id+"F0.wireOp",EDGE,"E939");
            var Q35;
            Q35=sQuery(id+"F0.wireOp",EDGE,"E923");
            var Q36;
            Q36=sQuery(id+"F0.wireOp",EDGE,"E917");
            var Q37;
            Q37=sQuery(id+"F0.wireOp",EDGE,"E877");
            var Q38;
            Q38=sQuery(id+"F0.wireOp",EDGE,"E803");
            var Q39;
            Q39=sQuery(id+"F0.wireOp",EDGE,"E922");
            var Q40;
            Q40=sQuery(id+"F0.wireOp",EDGE,"E865");
            var Q41;
            Q41=sQuery(id+"F0.wireOp",EDGE,"E912");
            var Q42;
            Q42=sQuery(id+"F0.wireOp",EDGE,"E895");
            var Q43;
            Q43=sQuery(id+"F0.wireOp",EDGE,"E886");
            var Q44;
            Q44=sQuery(id+"F0.wireOp",EDGE,"E868");
            var Q45;
            Q45=sQuery(id+"F0.wireOp",EDGE,"E853");
            var Q46;
            Q46=sQuery(id+"F0.wireOp",EDGE,"E812");
            var Q47;
            Q47=sQuery(id+"F0.wireOp",EDGE,"E818");
            var Q48;
            Q48=sQuery(id+"F0.wireOp",EDGE,"E943");
            var Q49;
            Q49=sQuery(id+"F0.wireOp",EDGE,"E950");
            var Q50;
            Q50=sQuery(id+"F0.wireOp",EDGE,"E2");
            var Q51;
            Q51=sQuery(id+"F0.wireOp",EDGE,"E857");
            var Q52;
            Q52=sQuery(id+"F0.wireOp",EDGE,"E815");
            var Q53;
            Q53=sQuery(id+"F0.wireOp",EDGE,"E933");
            var Q54;
            Q54=sQuery(id+"F0.wireOp",EDGE,"E817");
            var Q55;
            Q55=sQuery(id+"F0.wireOp",EDGE,"E835");
            var Q56;
            Q56=sQuery(id+"F0.wireOp",EDGE,"E953");
            var Q57;
            Q57=sQuery(id+"F0.wireOp",EDGE,"E836");
            var Q58;
            Q58=sQuery(id+"F0.wireOp",EDGE,"E955");
            var Q59;
            Q59=sQuery(id+"F0.wireOp",EDGE,"E946");
            var Q60;
            Q60=sQuery(id+"F0.wireOp",EDGE,"E816");
            var Q61;
            Q61=sQuery(id+"F0.wireOp",EDGE,"E934");
            var Q62;
            Q62=sQuery(id+"F0.wireOp",EDGE,"E954");
            var Q63;
            Q63=sQuery(id+"F0.wireOp",EDGE,"E30");
            var Q64;
            Q64=sQuery(id+"F0.wireOp",EDGE,"E958");
            var Q65;
            Q65=sQuery(id+"F0.wireOp",EDGE,"E1033");
            var Q66;
            Q66=sQuery(id+"F0.wireOp",EDGE,"E805");
            var Q67;
            Q67=sQuery(id+"F0.wireOp",EDGE,"E941");
            var Q68;
            Q68=sQuery(id+"F0.wireOp",EDGE,"E837");
            var Q69;
            Q69=sQuery(id+"F0.wireOp",EDGE,"E937");
            var Q70;
            Q70=sQuery(id+"F0.wireOp",EDGE,"E821");
            var Q71;
            Q71=sQuery(id+"F0.wireOp",EDGE,"E7");
            var Q72;
            Q72=sQuery(id+"F0.wireOp",EDGE,"E6");
            var Q73;
            Q73=sQuery(id+"F0.wireOp",EDGE,"E1");
            var Q74;
            Q74=sQuery(id+"F0.wireOp",EDGE,"E0");
            var Q75;
            Q75=sQuery(id+"F0.wireOp",EDGE,"E872");
            var Q76;
            Q76=sQuery(id+"F0.wireOp",EDGE,"E806");
            var Q77;
            Q77=sQuery(id+"F0.wireOp",EDGE,"E1034");
            var Q78;
            Q78=sQuery(id+"F0.wireOp",EDGE,"E820");
            var Q79;
            Q79=sQuery(id+"F0.wireOp",EDGE,"E918");
            var Q80;
            Q80=sQuery(id+"F0.wireOp",EDGE,"E876");
            var Q81;
            Q81=sQuery(id+"F0.wireOp",EDGE,"E920");
            var Q82;
            Q82=sQuery(id+"F0.wireOp",EDGE,"E819");
            var Q83;
            Q83=sQuery(id+"F0.wireOp",EDGE,"E811");
            var Q84;
            Q84=sQuery(id+"F0.wireOp",EDGE,"E885");
            var Q85;
            Q85=sQuery(id+"F0.wireOp",EDGE,"E921");
            var Q86;
            Q86=sQuery(id+"F0.wireOp",EDGE,"E913");
            var Q87;
            Q87=sQuery(id+"F0.wireOp",EDGE,"E851");
            var Q88;
            Q88=sQuery(id+"F0.wireOp",EDGE,"E907");
            var Q89;
            Q89=sQuery(id+"F0.wireOp",EDGE,"E871");
            var Q90;
            Q90=sQuery(id+"F0.wireOp",EDGE,"E834");
            var Q91;
            Q91=sQuery(id+"F0.wireOp",EDGE,"E862");
            var Q92;
            Q92=sQuery(id+"F0.wireOp",EDGE,"E1023");
            var Q93;
            Q93=sQuery(id+"F0.wireOp",EDGE,"E982");
            var Q94;
            Q94=sQuery(id+"F0.wireOp",EDGE,"E974");
            var Q95;
            Q95=sQuery(id+"F0.wireOp",EDGE,"E961");
            var Q96;
            Q96=sQuery(id+"F0.wireOp",EDGE,"E833");
            var Q97;
            Q97=sQuery(id+"F0.wireOp",EDGE,"E861");
            var Q98;
            Q98=sQuery(id+"F0.wireOp",EDGE,"E924");
            var Q99;
            Q99=sQuery(id+"F0.wireOp",EDGE,"E1032");
            var Q100;
            Q100=sQuery(id+"F0.wireOp",EDGE,"E969");
            var Q101;
            Q101=sQuery(id+"F0.wireOp",EDGE,"E981");
            var Q102;
            Q102=sQuery(id+"F0.wireOp",EDGE,"E884");
            var Q103;
            Q103=sQuery(id+"F0.wireOp",EDGE,"E878");
            var Q104;
            Q104=sQuery(id+"F0.wireOp",EDGE,"E850");
            var Q105;
            Q105=sQuery(id+"F0.wireOp",EDGE,"E870");
            var Q106;
            Q106=sQuery(id+"F0.wireOp",EDGE,"E1028");
            var Q107;
            Q107=sQuery(id+"F0.wireOp",EDGE,"E968");
            var Q108;
            Q108=sQuery(id+"F0.wireOp",EDGE,"E988");
            var Q109;
            Q109=sQuery(id+"F0.wireOp",EDGE,"E980");
            var Q110;
            Q110=sQuery(id+"F0.wireOp",EDGE,"E822");
            var Q111;
            Q111=sQuery(id+"F0.wireOp",EDGE,"E866");
            var Q112;
            Q112=sQuery(id+"F0.wireOp",EDGE,"E1025");
            var Q113;
            Q113=sQuery(id+"F0.wireOp",EDGE,"E810");
            var Q114;
            Q114=sQuery(id+"F0.wireOp",EDGE,"E931");
            var Q115;
            Q115=sQuery(id+"F0.wireOp",EDGE,"E849");
            var Q116;
            Q116=sQuery(id+"F0.wireOp",EDGE,"E869");
            var Q117;
            Q117=sQuery(id+"F0.wireOp",EDGE,"E905");
            var Q118;
            Q118=sQuery(id+"F0.wireOp",EDGE,"E832");
            var Q119;
            Q119=sQuery(id+"F0.wireOp",EDGE,"E875");
            var Q120;
            Q120=sQuery(id+"F0.wireOp",EDGE,"E1027");
            var Q121;
            Q121=sQuery(id+"F0.wireOp",EDGE,"E979");
            var Q122;
            Q122=sQuery(id+"F0.wireOp",EDGE,"E967");
            var Q123;
            Q123=sQuery(id+"F0.wireOp",EDGE,"E883");
            var Q124;
            Q124=sQuery(id+"F0.wireOp",EDGE,"E908");
            var Q125;
            Q125=sQuery(id+"F0.wireOp",EDGE,"E919");
            var Q126;
            Q126=sQuery(id+"F0.wireOp",EDGE,"E809");
            var Q127;
            Q127=sQuery(id+"F0.wireOp",EDGE,"E848");
            var Q128;
            Q128=sQuery(id+"F0.wireOp",EDGE,"E881");
            var Q129;
            Q129=sQuery(id+"F0.wireOp",EDGE,"E826");
            var Q130;
            Q130=sQuery(id+"F0.wireOp",EDGE,"E903");
            var Q131;
            Q131=sQuery(id+"F0.wireOp",EDGE,"E840");
            var Q132;
            Q132=sQuery(id+"F0.wireOp",EDGE,"E874");
            var Q133;
            Q133=sQuery(id+"F0.wireOp",EDGE,"E966");
            var Q134;
            Q134=sQuery(id+"F0.wireOp",EDGE,"E978");
            var Q135;
            Q135=sQuery(id+"F0.wireOp",EDGE,"cdc0a224-aea8-41c6-a81f-871d923c7d92");
            var Q136;
            Q136=sQuery(id+"F0.wireOp",EDGE,"E893");
            var Q137;
            Q137=sQuery(id+"F0.wireOp",EDGE,"bc39cccc-46bb-4995-b1c6-2d97363e9930");
            var Q138;
            Q138=sQuery(id+"F0.wireOp",EDGE,"E838");
            var Q139;
            Q139=sQuery(id+"F0.wireOp",EDGE,"E844");
            var Q140;
            Q140=sQuery(id+"F0.wireOp",EDGE,"43ff72d7-fdd7-47b5-8dc7-33902472c25b");
            var Q141;
            Q141=sQuery(id+"F0.wireOp",EDGE,"9a1018fb-7509-48c5-9983-983c4e2f5393");
            var Q142;
            Q142=sQuery(id+"F0.wireOp",EDGE,"312ed6c2-6fb5-4807-85d1-3ac4b1190a24");
            var Q143;
            Q143=sQuery(id+"F0.wireOp",EDGE,"E1017");
            var Q144;
            Q144=sQuery(id+"F0.wireOp",EDGE,"c983bd9c-7af0-4034-918c-bd9357f90098");
            var Q145;
            Q145=sQuery(id+"F0.wireOp",EDGE,"E1001");
            var Q146;
            Q146=sQuery(id+"F0.wireOp",EDGE,"E962");
            var Q147;
            Q147=sQuery(id+"F0.wireOp",EDGE,"e36aca62-5309-4241-a6a4-e7c9d19b2996");
            var Q148;
            Q148=sQuery(id+"F0.wireOp",EDGE,"b2061277-c1e9-47e3-8b0b-c7ee70998474");
            var Q149;
            Q149=sQuery(id+"F0.wireOp",EDGE,"472061d3-1b85-4f8c-91b7-9786c5c18222");
            var Q150;
            Q150=sQuery(id+"F0.wireOp",EDGE,"E1005");
            var Q151;
            Q151=sQuery(id+"F0.wireOp",EDGE,"E986");
            var Q152;
            Q152=sQuery(id+"F0.wireOp",EDGE,"E830");
            var Q153;
            Q153=sQuery(id+"F0.wireOp",EDGE,"E964");
            var Q154;
            Q154=sQuery(id+"F0.wireOp",EDGE,"E976");
            var Q155;
            Q155=sQuery(id+"F0.wireOp",EDGE,"E1022");
            var Q156;
            Q156=sQuery(id+"F0.wireOp",EDGE,"E1009");
            var Q157;
            Q157=sQuery(id+"F0.wireOp",EDGE,"6d931976-14f4-42fa-a9cf-b36e56378210");
            var Q158;
            Q158=sQuery(id+"F0.wireOp",EDGE,"E902");
            var Q159;
            Q159=sQuery(id+"F0.wireOp",EDGE,"29d0a25d-e4a0-4b36-a27e-578b47d1bdb7");
            var Q160;
            Q160=sQuery(id+"F0.wireOp",EDGE,"b1ade15e-ac78-4de9-8870-3ebd057eae47");
            var Q161;
            Q161=sQuery(id+"F0.wireOp",EDGE,"E890");
            var Q162;
            Q162=sQuery(id+"F0.wireOp",EDGE,"E927");
            var Q163;
            Q163=sQuery(id+"F0.wireOp",EDGE,"E906");
            var Q164;
            Q164=sQuery(id+"F0.wireOp",EDGE,"E846");
            var Q165;
            Q165=sQuery(id+"F0.wireOp",EDGE,"099a45de-8323-4931-8ac2-2f65142ab7f5");
            var Q166;
            Q166=sQuery(id+"F0.wireOp",EDGE,"fa67e3ec-6e7e-4efd-9874-503e8d5aa896");
            var Q167;
            Q167=sQuery(id+"F0.wireOp",EDGE,"cbbc4eb4-0ef0-4003-91c5-345c761bc047");
            var Q168;
            Q168=sQuery(id+"F0.wireOp",EDGE,"E864");
            var Q169;
            Q169=sQuery(id+"F0.wireOp",EDGE,"E1031");
            var Q170;
            Q170=sQuery(id+"F0.wireOp",EDGE,"E855");
            var Q171;
            Q171=sQuery(id+"F0.wireOp",EDGE,"E1029");
            var Q172;
            Q172=sQuery(id+"F0.wireOp",EDGE,"5f8e1ba7-8a23-4369-a411-7742abd484a9");
            var Q173;
            Q173=sQuery(id+"F0.wireOp",EDGE,"E1015");
            var Q174;
            Q174=sQuery(id+"F0.wireOp",EDGE,"E1004");
            var Q175;
            Q175=sQuery(id+"F0.wireOp",EDGE,"E960");
            var Q176;
            Q176=sQuery(id+"F0.wireOp",EDGE,"E973");
            var Q177;
            Q177=sQuery(id+"F0.wireOp",EDGE,"71c39cb7-5196-4dc6-ab58-8d6bdb40f9c6");
            var Q178;
            Q178=sQuery(id+"F0.wireOp",EDGE,"E916");
            var Q179;
            Q179=sQuery(id+"F0.wireOp",EDGE,"E842");
            var Q180;
            Q180=sQuery(id+"F0.wireOp",EDGE,"E813");
            var Q181;
            Q181=sQuery(id+"F0.wireOp",EDGE,"E860");
            var Q182;
            Q182=sQuery(id+"F0.wireOp",EDGE,"e863e419-e6b4-4ea0-b17f-5765d6024846");
            var Q183;
            Q183=sQuery(id+"F0.wireOp",EDGE,"e8690d2a-224f-4857-bd98-dc8a85aa94e4");
            var Q184;
            Q184=sQuery(id+"F0.wireOp",EDGE,"E1020");
            var Q185;
            Q185=sQuery(id+"F0.wireOp",EDGE,"E1007");
            var Q186;
            Q186=sQuery(id+"F0.wireOp",EDGE,"E987");
            var Q187;
            Q187=sQuery(id+"F0.wireOp",EDGE,"E998");
            var Q188;
            Q188=sQuery(id+"F0.wireOp",EDGE,"E972");
            var Q189;
            Q189=sQuery(id+"F0.wireOp",EDGE,"E852");
            var Q190;
            Q190=sQuery(id+"F0.wireOp",EDGE,"E897");
            var Q191;
            Q191=sQuery(id+"F0.wireOp",EDGE,"E863");
            var Q192;
            Q192=sQuery(id+"F0.wireOp",EDGE,"E825");
            var Q193;
            Q193=sQuery(id+"F0.wireOp",EDGE,"83cc3bc7-c428-4e94-ac31-b6e446562241");
            var Q194;
            Q194=sQuery(id+"F0.wireOp",EDGE,"E879");
            var Q195;
            Q195=sQuery(id+"F0.wireOp",EDGE,"54a5e1ec-1ecf-47fa-89bc-6a71472cd95e");
            var Q196;
            Q196=sQuery(id+"F0.wireOp",EDGE,"E1024");
            var Q197;
            Q197=sQuery(id+"F0.wireOp",EDGE,"E904");
            var Q198;
            Q198=sQuery(id+"F0.wireOp",EDGE,"E824");
            var Q199;
            Q199=sQuery(id+"F0.wireOp",EDGE,"E1002");
            var Q200;
            Q200=sQuery(id+"F0.wireOp",EDGE,"E983");
            var Q201;
            Q201=sQuery(id+"F0.wireOp",EDGE,"E827");
            var Q202;
            Q202=sQuery(id+"F0.wireOp",EDGE,"bbe12b69-1339-4445-98e5-bc8a7c76dc8a");
            var Q203;
            Q203=sQuery(id+"F0.wireOp",EDGE,"ff9602f2-77e2-4368-987a-6285d16a0c96");
            var Q204;
            Q204=sQuery(id+"F0.wireOp",EDGE,"0c64cd33-312b-416a-89a1-1da72ed71bd0");
            var Q205;
            Q205=sQuery(id+"F0.wireOp",EDGE,"c449b056-d35f-4f2e-a958-e9bf5da80a05");
            var Q206;
            Q206=sQuery(id+"F0.wireOp",EDGE,"f9394eab-178f-45c5-897e-ce77d937d24f");
            var Q207;
            Q207=sQuery(id+"F0.wireOp",EDGE,"a060e41b-989e-4451-ae43-0cfb2c1e98f5");
            var Q208;
            Q208=sQuery(id+"F0.wireOp",EDGE,"E867");
            var Q209;
            Q209=sQuery(id+"F0.wireOp",EDGE,"7a0d2995-c34d-4865-b9f3-07111121c4c4");
            var Q210;
            Q210=sQuery(id+"F0.wireOp",EDGE,"6d369d4c-ed45-4b99-8ca1-fbd43ed49f33");
            var Q211;
            Q211=sQuery(id+"F0.wireOp",EDGE,"72bba3b3-873d-447f-a342-fed4d893cd13");
            var Q212;
            Q212=sQuery(id+"F0.wireOp",EDGE,"bae28338-ddd6-4c6a-b9f6-02485098fde6");
            var Q213;
            Q213=sQuery(id+"F0.wireOp",EDGE,"d4c4c522-f95f-47e7-a99d-0df94f2807e5");
            var Q214;
            Q214=sQuery(id+"F0.wireOp",EDGE,"d9a67787-17b4-47ce-a9c6-cfeb8296acf9");
            var Q215;
            Q215=sQuery(id+"F0.wireOp",EDGE,"e5bf8433-dc89-4e04-81ee-7a8bb34c6838");
            var Q216;
            Q216=sQuery(id+"F0.wireOp",EDGE,"825093fd-8aa2-44ec-8f70-d18631b84c55");
            var Q217;
            Q217=sQuery(id+"F0.wireOp",EDGE,"5d2047ff-9164-452d-9cb9-88a478ec0fa3");
            var Q218;
            Q218=sQuery(id+"F0.wireOp",EDGE,"47876a35-bffe-4eb6-baaa-d4c3d486001d");
            var Q219;
            Q219=sQuery(id+"F0.wireOp",EDGE,"9ad84fa8-761a-443f-b740-1985d570915a");
            var Q220;
            Q220=sQuery(id+"F0.wireOp",EDGE,"6ec50b46-1b64-4e3d-b857-da350ce8e41d");
            var Q221;
            Q221=sQuery(id+"F0.wireOp",EDGE,"62cac10d-e5b1-4951-998b-e049fa1455c4");
            var Q222;
            Q222=sQuery(id+"F0.wireOp",EDGE,"512e75ab-63a2-4055-a3c7-f23ede31a562");
            var Q223;
            Q223=sQuery(id+"F0.wireOp",EDGE,"b739928d-7f18-4173-94c2-834139890039");
            var Q224;
            Q224=sQuery(id+"F0.wireOp",EDGE,"0b9ec59e-cc14-48af-a710-f9976c519150");
            var Q225;
            Q225=sQuery(id+"F0.wireOp",EDGE,"5deb0e7e-419e-4f0d-a7a9-13f0747407a0");
            var Q226;
            Q226=sQuery(id+"F0.wireOp",EDGE,"e1296081-e6fe-45e2-8fa3-eea8bf72fa41");
            var Q227;
            Q227=sQuery(id+"F0.wireOp",EDGE,"b9f2806e-95a8-45a6-8ec1-a161dd1ec68a");
            var Q228;
            Q228=sQuery(id+"F0.wireOp",EDGE,"4cf72698-9ecf-4465-9cce-3db976e7d02d");
            var Q229;
            Q229=sQuery(id+"F0.wireOp",EDGE,"c997236b-a306-452c-a95a-fcc6a9c51b76");
            var Q230;
            Q230=sQuery(id+"F0.wireOp",EDGE,"76471b3e-ed4f-4709-b69d-5cdf395d66fe");
            var Q231;
            Q231=sQuery(id+"F0.wireOp",EDGE,"b0d9f231-a6e8-4934-be0e-59488f2b0fa8");
            var Q232;
            Q232=sQuery(id+"F0.wireOp",EDGE,"4097a8aa-f8a1-448f-8927-2fffd177a227");
            var Q233;
            Q233=sQuery(id+"F0.wireOp",EDGE,"E843");
            var Q234;
            Q234=sQuery(id+"F0.wireOp",EDGE,"b1a72132-80b2-4fcc-943e-6907f23ef3dc");
            var Q235;
            Q235=sQuery(id+"F0.wireOp",EDGE,"E984");
            var Q236;
            Q236=sQuery(id+"F0.wireOp",EDGE,"06fed679-c378-4324-974f-901c71e4a27d");
            var Q237;
            Q237=sQuery(id+"F0.wireOp",EDGE,"2503f15e-fea5-4a69-b3a0-f0f7379b1eb2");
            var Q238;
            Q238=sQuery(id+"F0.wireOp",EDGE,"a2face15-2e22-416f-bc70-2698bcba3738");
            var Q239;
            Q239=sQuery(id+"F0.wireOp",EDGE,"da935abc-0fc6-41ad-a00a-e9e7717a88ad");
            var Q240;
            Q240=sQuery(id+"F0.wireOp",EDGE,"E1000");
            var Q241;
            Q241=sQuery(id+"F0.wireOp",EDGE,"b379f1f5-1bad-4337-affb-4b34963f9315");
            var Q242;
            Q242=sQuery(id+"F0.wireOp",EDGE,"7e499759-eef9-4783-a56c-cff78a9e3abc");
            var Q243;
            Q243=sQuery(id+"F0.wireOp",EDGE,"E1021");
            var Q244;
            Q244=sQuery(id+"F0.wireOp",EDGE,"E1008");
            var Q245;
            Q245=sQuery(id+"F0.wireOp",EDGE,"1a04b766-c9a5-48b2-8ae5-41076a6c997e");
            var Q246;
            Q246=sQuery(id+"F0.wireOp",EDGE,"E892");
            var Q247;
            Q247=sQuery(id+"F0.wireOp",EDGE,"322cda39-e27f-47c0-a6bc-b5473caf3b12");
            var Q248;
            Q248=sQuery(id+"F0.wireOp",EDGE,"E1018");
            var Q249;
            Q249=sQuery(id+"F0.wireOp",EDGE,"d3c9d076-696d-4f37-8d5a-000095cdc5d9");
            var Q250;
            Q250=sQuery(id+"F0.wireOp",EDGE,"574fa6f7-6ba7-4809-a873-41cd5075c195");
            var Q251;
            Q251=sQuery(id+"F0.wireOp",EDGE,"eae9e281-cfbd-481d-a72b-a17e7f3f8396");
            var Q252;
            Q252=sQuery(id+"F0.wireOp",EDGE,"E823");
            var Q253;
            Q253=sQuery(id+"F0.wireOp",EDGE,"3347e06c-3686-4eb5-9ad0-f2956d319f7b");
            var Q254;
            Q254=sQuery(id+"F0.wireOp",EDGE,"E1003");
            var Q255;
            Q255=sQuery(id+"F0.wireOp",EDGE,"ff4ffe44-eb2f-4a67-9829-d30d49ef5e2a");
            var Q256;
            Q256=sQuery(id+"F0.wireOp",EDGE,"94aba077-545a-4114-b0de-c06442fa6d05");
            var Q257;
            Q257=sQuery(id+"F0.wireOp",EDGE,"E985");
            var Q258;
            Q258=sQuery(id+"F0.wireOp",EDGE,"E977");
            var Q259;
            Q259=sQuery(id+"F0.wireOp",EDGE,"68a75019-cdc5-482e-bdab-0989c7975d1f");
            var Q260;
            Q260=sQuery(id+"F0.wireOp",EDGE,"4625a7d6-32b5-4c13-9cc2-4be30836bec0");
            var Q261;
            Q261=sQuery(id+"F0.wireOp",EDGE,"8df6b744-6bf7-4631-b5a1-4e5a65822869");
            var Q262;
            Q262=sQuery(id+"F0.wireOp",EDGE,"E829");
            var Q263;
            Q263=sQuery(id+"F0.wireOp",EDGE,"0287ac27-b1aa-43dd-8d99-8c5cee18e590");
            var Q264;
            Q264=sQuery(id+"F0.wireOp",EDGE,"42f5cbc7-aa84-4dbf-8367-f227c23708ba");
            var Q265;
            Q265=sQuery(id+"F0.wireOp",EDGE,"2bbe2262-2074-4fc3-a78f-68f10f7271c7");
            var Q266;
            Q266=sQuery(id+"F0.wireOp",EDGE,"E1030");
            var Q267;
            Q267=sQuery(id+"F0.wireOp",EDGE,"d6f7bc65-4a59-4f4d-8b18-00a0f1c0727b");
            var Q268;
            Q268=sQuery(id+"F0.wireOp",EDGE,"E1014");
            var Q269;
            Q269=sQuery(id+"F0.wireOp",EDGE,"E901");
            var Q270;
            Q270=sQuery(id+"F0.wireOp",EDGE,"2c7db86f-f387-471c-9791-867d9fdabf95");
            var Q271;
            Q271=sQuery(id+"F0.wireOp",EDGE,"E889");
            var Q272;
            Q272=sQuery(id+"F0.wireOp",EDGE,"E845");
            var Q273;
            Q273=sQuery(id+"F0.wireOp",EDGE,"E854");
            var Q274;
            Q274=sQuery(id+"F0.wireOp",EDGE,"609a37af-97ff-4365-b039-f565c52880ca");
            var Q275;
            Q275=sQuery(id+"F0.wireOp",EDGE,"c2140cea-6f73-493d-b4ad-d5984a63a3f7");
            var Q276;
            Q276=sQuery(id+"F0.wireOp",EDGE,"92ec2daa-221f-479b-a102-8d12d0d9b9bb");
            var Q277;
            Q277=sQuery(id+"F0.wireOp",EDGE,"bd7edcda-c087-4c16-815e-04a7961a16dc");
            var Q278;
            Q278=sQuery(id+"F0.wireOp",EDGE,"0895a20b-ebc3-44c2-88b5-9414cf76fb1c");
            var Q279;
            Q279=sQuery(id+"F0.wireOp",EDGE,"E915");
            var Q280;
            Q280=sQuery(id+"F0.wireOp",EDGE,"E841");
            var Q281;
            Q281=sQuery(id+"F0.wireOp",EDGE,"E963");
            var Q282;
            Q282=sQuery(id+"F0.wireOp",EDGE,"baf83a39-2ee5-4bd8-84a4-7186442840e7");
            var Q283;
            Q283=sQuery(id+"F0.wireOp",EDGE,"E959");
            var Q284;
            Q284=sQuery(id+"F0.wireOp",EDGE,"E859");
            var Q285;
            Q285=sQuery(id+"F0.wireOp",EDGE,"E1026");
            var Q286;
            Q286=sQuery(id+"F0.wireOp",EDGE,"E1013");
            var Q287;
            Q287=sQuery(id+"F0.wireOp",EDGE,"a1e67bd4-0821-4104-a0f2-3aa55e58fcb5");
            var Q288;
            Q288=sQuery(id+"F0.wireOp",EDGE,"E971");
            var Q289;
            Q289=sQuery(id+"F0.wireOp",EDGE,"962c5001-3d36-4d51-bb1e-a1e731ce15f7");
            var Q290;
            Q290=sQuery(id+"F0.wireOp",EDGE,"E945");
            var Q291;
            Q291=sQuery(id+"F0.wireOp",EDGE,"8e4a2f44-10bf-4950-a08c-941d8413bbf2");
            var Q292;
            Q292=sQuery(id+"F0.wireOp",EDGE,"c9618bfa-b404-436b-ad41-d31a25e11c55");
            var Q293;
            Q293=sQuery(id+"F0.wireOp",EDGE,"ad80cf75-1c2f-46aa-88a1-5ee16af714ee");
            var Q294;
            Q294=sQuery(id+"F0.wireOp",EDGE,"e8c1205a-5a77-4fd1-9301-6a95dbff5f1c");
            var Q295;
            Q295=sQuery(id+"F0.wireOp",EDGE,"E1006");
            var Q296;
            Q296=sQuery(id+"F0.wireOp",EDGE,"2771b44c-2e19-4826-b9d2-e3c3cc3c9675");
            var Q297;
            Q297=sQuery(id+"F0.wireOp",EDGE,"a821aa22-c915-4f13-a428-b72c5fd355c7");
            var Q298;
            Q298=sQuery(id+"F0.wireOp",EDGE,"5dc678d2-1053-44bf-a139-d94a8a6ad452");
            var Q299;
            Q299=sQuery(id+"F0.wireOp",EDGE,"8bf1d2ba-fd2b-48d2-bf5c-46e33ca34b55");
            var Q300;
            Q300=sQuery(id+"F0.wireOp",EDGE,"29ab85e9-d642-4a3a-a5e4-723f07f29d2a");
            var Q301;
            Q301=sQuery(id+"F0.wireOp",EDGE,"f4cadf86-af98-408b-8f87-9aa1b2f3a70c");
            var Q302;
            Q302=sQuery(id+"F0.wireOp",EDGE,"e4792239-90e6-4d6b-b65c-8a9bc76ea7e6");
            var Q303;
            Q303=sQuery(id+"F0.wireOp",EDGE,"ce387b29-bb8f-4fc7-b2a1-2ab5daa77b03");
            var Q304;
            Q304=sQuery(id+"F0.wireOp",EDGE,"db43410d-95d9-4df2-b210-1cb29ee2706c");
            var Q305;
            Q305=sQuery(id+"F0.wireOp",EDGE,"962e4d56-84b2-4428-9969-9f8ccd511e50");
            var Q306;
            Q306=sQuery(id+"F0.wireOp",EDGE,"eb7b9c8b-a3f1-428e-8edd-b146506a69b7");
            var Q307;
            Q307=sQuery(id+"F0.wireOp",EDGE,"01adead8-caab-4bd5-b094-2681d1e0e05c");
            var Q308;
            Q308=sQuery(id+"F0.wireOp",EDGE,"e60e44eb-0b74-4a1c-8386-9dcced35d97c");
            var Q309;
            Q309=sQuery(id+"F0.wireOp",EDGE,"0444f39a-ffc6-4234-9f76-a907715c76f7");
            var Q310;
            Q310=sQuery(id+"F0.wireOp",EDGE,"1898346c-e4c7-486e-916f-2e7f4a387cd6");
            var Q311;
            Q311=sQuery(id+"F0.wireOp",EDGE,"66ed40d4-8dc9-4648-bee7-e5e4e7dd7e9b");
            var Q312;
            Q312=sQuery(id+"F0.wireOp",EDGE,"9dccb327-35f5-4ac2-8b7d-8d81f978e2c1");
            var Q313;
            Q313=sQuery(id+"F0.wireOp",EDGE,"5777fa3e-7bb5-47b9-ac10-615e4ea5d59d");
            var Q314;
            Q314=sQuery(id+"F0.wireOp",EDGE,"8009bce4-192d-49b4-a337-6950730249ba");
            var Q315;
            Q315=sQuery(id+"F0.wireOp",EDGE,"09230063-8580-4e24-a287-6f2da9dbbf0f");
            var Q316;
            Q316=sQuery(id+"F0.wireOp",EDGE,"dc91e3a6-d7d9-40f3-80de-3a6bfaabbb9d");
            var Q317;
            Q317=sQuery(id+"F0.wireOp",EDGE,"a4c23b64-05f9-4ef3-a80f-bd60344bfe29");
            var Q318;
            Q318=sQuery(id+"F0.wireOp",EDGE,"f590e5ea-0877-439a-b6c0-cbd4b1aa47b3");
            var Q319;
            Q319=sQuery(id+"F0.wireOp",EDGE,"E930");
            var Q320;
            Q320=sQuery(id+"F0.wireOp",EDGE,"fe0454da-1e97-4748-aa08-4f6f4616a8b3");
            var Q321;
            Q321=sQuery(id+"F0.wireOp",EDGE,"0ee439c5-e576-43cc-9564-91bf15b2f0fd");
            var Q322;
            Q322=sQuery(id+"F0.wireOp",EDGE,"944ea9ee-5563-404e-8b09-fbb085500a0e");
            var Q323;
            Q323=sQuery(id+"F0.wireOp",EDGE,"697fe53e-25cd-4641-899a-709ec1092e21");
            var Q324;
            Q324=sQuery(id+"F0.wireOp",EDGE,"E873");
            var Q325;
            Q325=sQuery(id+"F0.wireOp",EDGE,"5eb74230-47f2-466b-9c8d-72e358125a43");
            var Q326;
            Q326=sQuery(id+"F0.wireOp",EDGE,"5e39a1cb-6b71-4dda-a2a0-18214ba4fc21");
            var Q327;
            Q327=sQuery(id+"F0.wireOp",EDGE,"14d3b580-9a93-4046-998e-70edd759602c");
            var Q328;
            Q328=sQuery(id+"F0.wireOp",EDGE,"288657c2-08e3-4bd5-b65e-4a861e63620c");
            var Q329;
            Q329=sQuery(id+"F0.wireOp",EDGE,"260f5ce1-0fb5-42ce-83ab-60cfa753a113");
            var Q330;
            Q330=sQuery(id+"F0.wireOp",EDGE,"334cb1f4-53b9-4fff-8bd9-cdc899bf692d");
            var Q331;
            Q331=sQuery(id+"F0.wireOp",EDGE,"E999");
            var Q332;
            Q332=sQuery(id+"F0.wireOp",EDGE,"E808");
            var Q333;
            Q333=sQuery(id+"F0.wireOp",EDGE,"144c2dc0-3634-41d5-bae4-fb9a6429f866");
            var Q334;
            Q334=sQuery(id+"F0.wireOp",EDGE,"0ffb3c8c-acd7-4940-bff6-8103a661c58b");
            var Q335;
            Q335=sQuery(id+"F0.wireOp",EDGE,"9dc785f0-25bf-423e-95f9-5c680652c30b");
            var Q336;
            Q336=sQuery(id+"F0.wireOp",EDGE,"422afe0e-c483-4bd5-958f-d303fff509a8");
            var Q337;
            Q337=sQuery(id+"F0.wireOp",EDGE,"E970");
            var Q338;
            Q338=sQuery(id+"F0.wireOp",EDGE,"f62bf0f7-813d-4fdc-9f0b-19ac61a75c1a");
            var Q339;
            Q339=sQuery(id+"F0.wireOp",EDGE,"ca25e040-1b5d-4877-9178-8d605860d4ed");
            var Q340;
            Q340=sQuery(id+"F0.wireOp",EDGE,"E899");
            var Q341;
            Q341=sQuery(id+"F0.wireOp",EDGE,"2d102040-a846-4325-8181-a7c8054a4ab6");
            var Q342;
            Q342=sQuery(id+"F0.wireOp",EDGE,"a12fe08b-7315-4c05-b842-d1f7bc39658a");
            var Q343;
            Q343=sQuery(id+"F0.wireOp",EDGE,"794285c3-05a8-4859-9dbf-b327305d75b3");
            var Q344;
            Q344=sQuery(id+"F0.wireOp",EDGE,"8fbd2b2f-def5-4bb2-9b99-2850dba940d9");
            var Q345;
            Q345=sQuery(id+"F0.wireOp",EDGE,"c6b047ca-e4c8-495f-a3cc-21cac800a887");
            var Q346;
            Q346=sQuery(id+"F0.wireOp",EDGE,"58701f04-344e-4b87-9c6a-0fcfec83a3ee");
            var Q347;
            Q347=sQuery(id+"F0.wireOp",EDGE,"8229c53b-4803-4d55-8c96-dea8f0ea775d");
            var Q348;
            Q348=sQuery(id+"F0.wireOp",EDGE,"3ac4a822-6ea2-4749-bd48-6e8364794825");
            var Q349;
            Q349=sQuery(id+"F0.wireOp",EDGE,"9c15eda4-8800-4b2d-b753-ccb06505193d");
            var Q350;
            Q350=sQuery(id+"F0.wireOp",EDGE,"4acc60c7-388a-4dc3-ac42-e45b993e9081");
            var Q351;
            Q351=sQuery(id+"F0.wireOp",EDGE,"7504fb77-443d-452d-a50e-72def5781a08");
            var Q352;
            Q352=sQuery(id+"F0.wireOp",EDGE,"f43d0577-76f9-4d7b-89fc-d403f9392459");
            var Q353;
            Q353=sQuery(id+"F0.wireOp",EDGE,"E891");
            var Q354;
            Q354=sQuery(id+"F0.wireOp",EDGE,"a500b31e-5ea3-4658-b31b-6ab24c514578");
            var Q355;
            Q355=sQuery(id+"F0.wireOp",EDGE,"667bc6cb-0bca-4a3b-a9de-d843004ac1f2");
            var Q356;
            Q356=sQuery(id+"F0.wireOp",EDGE,"E847");
            var Q357;
            Q357=sQuery(id+"F0.wireOp",EDGE,"8eda9b34-7263-4f39-b93e-9326c730d5d0");
            var Q358;
            Q358=sQuery(id+"F0.wireOp",EDGE,"E856");
            var Q359;
            Q359=sQuery(id+"F0.wireOp",EDGE,"df3065ab-c28e-43bb-be7b-b37a5f2b5e30");
            var Q360;
            Q360=sQuery(id+"F0.wireOp",EDGE,"8e8442d9-479a-42dc-aa18-399aa399897e");
            var Q361;
            Q361=sQuery(id+"F0.wireOp",EDGE,"d3c7662d-d3dd-4d54-8648-fe943810d137");
            var Q362;
            Q362=sQuery(id+"F0.wireOp",EDGE,"E828");
            var Q363;
            Q363=sQuery(id+"F0.wireOp",EDGE,"74ff2ead-e5c3-4528-8ac3-b6686c5ddf08");
            var Q364;
            Q364=sQuery(id+"F0.wireOp",EDGE,"E975");
            var Q365;
            Q365=sQuery(id+"F0.wireOp",EDGE,"da7f3f3c-af03-43c8-a6e7-d43b24c7f7c1");
            var Q366;
            Q366=sQuery(id+"F0.wireOp",EDGE,"c13d3fb2-5ca2-4450-8b27-90f43d2e407a");
            var Q367;
            Q367=sQuery(id+"F0.wireOp",EDGE,"53936a19-08c9-4d20-b9f8-16be3742736c");
            var Q368;
            Q368=sQuery(id+"F0.wireOp",EDGE,"e89c2fff-b5b3-4877-8d92-0d3eefcffa27");
            var Q369;
            Q369=sQuery(id+"F0.wireOp",EDGE,"8c665c69-41ee-4d2d-b8f3-c2186e4a0584");
            var Q370;
            Q370=sQuery(id+"F0.wireOp",EDGE,"798ba0b1-0cd3-420b-82d7-f4c250af2a17");
            var Q371;
            Q371=sQuery(id+"F0.wireOp",EDGE,"b2616e62-406d-40e4-8c7b-4552a27a096e");
            var Q372;
            Q372=sQuery(id+"F0.wireOp",EDGE,"9351aec0-119b-4154-856a-320406b930db");
            var Q373;
            Q373=sQuery(id+"F0.wireOp",EDGE,"7577e5e3-1ebc-4e34-a30e-19b66d2a4027");
            var Q374;
            Q374=sQuery(id+"F0.wireOp",EDGE,"824f91da-6e62-40ff-9131-d3cf8db559e9");
            var Q375;
            Q375=sQuery(id+"F0.wireOp",EDGE,"6d016c04-86d9-4909-bfd5-871686835899");
            var Q376;
            Q376=sQuery(id+"F0.wireOp",EDGE,"488b71d9-aaa3-41f3-9dab-c114febdabb3");
            var Q377;
            Q377=sQuery(id+"F0.wireOp",EDGE,"E1019");
            var Q378;
            Q378=sQuery(id+"F0.wireOp",EDGE,"b27adb1e-0ad8-47cf-85be-6eaaab53ffed");
            var Q379;
            Q379=sQuery(id+"F0.wireOp",EDGE,"576fe0fb-72e4-4773-b968-bcc8a9823b42");
            var Q380;
            Q380=sQuery(id+"F0.wireOp",EDGE,"249b726a-b8af-489e-9a1d-83cee191e77f");
            var Q381;
            Q381=sQuery(id+"F0.wireOp",EDGE,"7f442ec8-8b06-4776-a0c1-ceaa7d053cb9");
            var Q382;
            Q382=sQuery(id+"F0.wireOp",EDGE,"c3f43872-2e25-426d-9bbb-c56da974beb1");
            var Q383;
            Q383=sQuery(id+"F0.wireOp",EDGE,"76a6b08f-6e62-4b33-b204-411812e5ad29");
            var Q384;
            Q384=sQuery(id+"F0.wireOp",EDGE,"E1010");
            var Q385;
            Q385=sQuery(id+"F0.wireOp",EDGE,"E995");
            var Q386;
            Q386=sQuery(id+"F0.wireOp",EDGE,"E1016");
            var Q387;
            Q387=sQuery(id+"F0.wireOp",EDGE,"27d582e7-14e9-4102-a524-274e76b22159");
            var Q388;
            Q388=sQuery(id+"F0.wireOp",EDGE,"4ce418c3-933e-4631-8a2c-692f15465339");
            var Q389;
            Q389=sQuery(id+"F0.wireOp",EDGE,"19f18548-1ceb-492c-9b99-b0b926571fdc");
            var Q390;
            Q390=sQuery(id+"F0.wireOp",EDGE,"6b22f77d-6811-4f3f-bbb8-f97fe59a24bb");
            var Q391;
            Q391=sQuery(id+"F0.wireOp",EDGE,"ec1f1de5-f2f4-4b79-8117-240645458c7b");
            var Q392;
            Q392=sQuery(id+"F0.wireOp",EDGE,"b8280172-94eb-4a06-9a6b-7bf1fb2692c5");
            var Q393;
            Q393=sQuery(id+"F0.wireOp",EDGE,"ed418bd0-8737-46f3-a725-07382cf5fe16");
            var Q394;
            Q394=sQuery(id+"F0.wireOp",EDGE,"95b5ff18-5fb1-42d5-8d0e-9188ebd57b54");
            var Q395;
            Q395=sQuery(id+"F0.wireOp",EDGE,"E839");
            var Q396;
            Q396=sQuery(id+"F0.wireOp",EDGE,"0462b1a8-ae60-4876-bb23-e7d27baba8b5");
            var Q397;
            Q397=sQuery(id+"F0.wireOp",EDGE,"ab570da4-77a8-40cb-b942-e5b709a26c00");
            var Q398;
            Q398=sQuery(id+"F0.wireOp",EDGE,"5bb571ac-6344-4a70-9319-e8369ee6cdbf");
            var Q399;
            Q399=sQuery(id+"F0.wireOp",EDGE,"b9613d34-02e0-4986-ac00-5444b133e690");
            var Q400;
            Q400=sQuery(id+"F0.wireOp",EDGE,"E994");
            var Q401;
            Q401=sQuery(id+"F0.wireOp",EDGE,"4ead381f-7aae-487b-a4ae-28d807b9e44f");
            var Q402;
            Q402=sQuery(id+"F0.wireOp",EDGE,"55d38448-261e-40d6-b89c-4b759f8821d6");
            var Q403;
            Q403=sQuery(id+"F0.wireOp",EDGE,"65763cf2-b856-49f0-b912-ee49d4150ab0");
            var Q404;
            Q404=sQuery(id+"F0.wireOp",EDGE,"00e3f4b1-1edc-4e9e-ac9a-bc02a6b7f2b4");
            var Q405;
            Q405=sQuery(id+"F0.wireOp",EDGE,"43b25094-7da1-4a93-912a-b2dd187738ea");
            var Q406;
            Q406=sQuery(id+"F0.wireOp",EDGE,"E1012");
            var Q407;
            Q407=sQuery(id+"F0.wireOp",EDGE,"accce7f7-1d05-4107-987e-b21e7e182c8a");
            var Q408;
            Q408=sQuery(id+"F0.wireOp",EDGE,"9624ebfd-bc3d-438b-a005-7d4f84a0f6a1");
            var Q409;
            Q409=sQuery(id+"F0.wireOp",EDGE,"fd42b984-01ed-490c-98c6-19d2c28b9150");
            var Q410;
            Q410=sQuery(id+"F0.wireOp",EDGE,"3711b7d3-dd82-4b83-b370-1c11a62b489a");
            var Q411;
            Q411=sQuery(id+"F0.wireOp",EDGE,"d3b9f2e9-0099-4e5f-974d-8179f7d3def4");
            var Q412;
            Q412=sQuery(id+"F0.wireOp",EDGE,"cf82a6e8-b48c-4aee-959b-edf2f47bd973");
            var Q413;
            Q413=sQuery(id+"F0.wireOp",EDGE,"b04c9a94-077f-4dbe-af55-f5a8fef62fb2");
            var Q414;
            Q414=sQuery(id+"F0.wireOp",EDGE,"E993");
            var Q415;
            Q415=sQuery(id+"F0.wireOp",EDGE,"6831b5af-558b-4b2a-bc8c-14abbc131d31");
            var Q416;
            Q416=sQuery(id+"F0.wireOp",EDGE,"1add2aac-fe33-4b21-a940-2eb45125e954");
            var Q417;
            Q417=sQuery(id+"F0.wireOp",EDGE,"86b7d8a0-2b92-4d84-b4bc-6690516fe7b2");
            var Q418;
            Q418=sQuery(id+"F0.wireOp",EDGE,"d0cc756a-f3e9-460f-8731-c1e943a631e5");
            var Q419;
            Q419=sQuery(id+"F0.wireOp",EDGE,"aaaf1c15-d134-416a-ac3b-f1fd17da8ea7");
            var Q420;
            Q420=sQuery(id+"F0.wireOp",EDGE,"111c2811-3065-4301-863d-0fba40a10008");
            var Q421;
            Q421=sQuery(id+"F0.wireOp",EDGE,"E807");
            var Q422;
            Q422=sQuery(id+"F0.wireOp",EDGE,"72110a64-596f-48fd-a8c1-f2c2006914f2");
            var Q423;
            Q423=sQuery(id+"F0.wireOp",EDGE,"e78ec1bd-2165-4f5e-ae24-297ae42f2223");
            var Q424;
            Q424=sQuery(id+"F0.wireOp",EDGE,"ba71f3a5-f54a-45dc-8a84-c00c16684f82");
            var Q425;
            Q425=sQuery(id+"F0.wireOp",EDGE,"580be2e5-d7a5-42b7-9151-916367c06abf");
            var Q426;
            Q426=sQuery(id+"F0.wireOp",EDGE,"da702d13-d1e6-4f09-ab54-6e6efe085d7a");
            var Q427;
            Q427=sQuery(id+"F0.wireOp",EDGE,"2a229516-efd7-44df-b1fc-3456b3fbba21");
            var Q428;
            Q428=sQuery(id+"F0.wireOp",EDGE,"49441a34-d703-41f0-8eaf-17c93d027547");
            var Q429;
            Q429=sQuery(id+"F0.wireOp",EDGE,"d83767a0-cb18-483f-b3fc-db13c80cb105");
            var Q430;
            Q430=sQuery(id+"F0.wireOp",EDGE,"E992");
            var Q431;
            Q431=sQuery(id+"F0.wireOp",EDGE,"c753922b-bef4-4564-b7e6-cf777146c8cb");
            var Q432;
            Q432=sQuery(id+"F0.wireOp",EDGE,"0ae07f46-b224-438c-84a1-5899bcc70ab1");
            var Q433;
            Q433=sQuery(id+"F0.wireOp",EDGE,"815ad818-d36c-4b1f-9bc9-827c0dffe5d4");
            var Q434;
            Q434=sQuery(id+"F0.wireOp",EDGE,"E814");
            var Q435;
            Q435=sQuery(id+"F0.wireOp",EDGE,"53e0a3f9-b461-41c0-a58e-dc23914a821d");
            var Q436;
            Q436=sQuery(id+"F0.wireOp",EDGE,"56bc0f3f-8ecd-4908-a735-d8e2b2aa5f79");
            var Q437;
            Q437=sQuery(id+"F0.wireOp",EDGE,"09b6fa1e-499d-49bc-9323-418cfc5a36a1");
            var Q438;
            Q438=sQuery(id+"F0.wireOp",EDGE,"E989");
            var Q439;
            Q439=sQuery(id+"F0.wireOp",EDGE,"a8ba6ce4-d652-47e9-9a5d-e343d79b1e8c");
            var Q440;
            Q440=sQuery(id+"F0.wireOp",EDGE,"9df087b0-41a5-4c65-8bca-e863bf3a727a");
            var Q441;
            Q441=sQuery(id+"F0.wireOp",EDGE,"57f98894-d9a2-4f38-862f-5e8a553039ca");
            var Q442;
            Q442=sQuery(id+"F0.wireOp",EDGE,"5724e3f6-ada3-49ec-b8b6-e62c6e324bf6");
            var Q443;
            Q443=sQuery(id+"F0.wireOp",EDGE,"22163893-96d8-45b3-bfc7-b890366f9851");
            var Q444;
            Q444=sQuery(id+"F0.wireOp",EDGE,"E997");
            var Q445;
            Q445=sQuery(id+"F0.wireOp",EDGE,"b0e365f7-9a71-4c75-a489-c81fa5f9cab0");
            var Q446;
            Q446=sQuery(id+"F0.wireOp",EDGE,"E991");
            var Q447;
            Q447=sQuery(id+"F0.wireOp",EDGE,"d37510bd-46f4-413c-87c8-0ba2cd4a6333");
            var Q448;
            Q448=sQuery(id+"F0.wireOp",EDGE,"3bd421ed-c2ac-42a5-b2e0-e2a51bbc301e");
            var Q449;
            Q449=sQuery(id+"F0.wireOp",EDGE,"d8b301e5-287a-4cf0-9b0d-ef2cdf519a13");
            var Q450;
            Q450=sQuery(id+"F0.wireOp",EDGE,"be9fe4ff-a39e-4d29-b50b-6e4054b6fe27");
            var Q451;
            Q451=sQuery(id+"F0.wireOp",EDGE,"2c3caccb-dfe3-4bb8-8d5a-4f0fe1ac84dd");
            var Q452;
            Q452=sQuery(id+"F0.wireOp",EDGE,"517b4d46-a341-4410-a54f-5a08f3fe55b8");
            var Q453;
            Q453=sQuery(id+"F0.wireOp",EDGE,"6ee76791-6987-49d8-8862-ef2f8ae81109");
            var Q454;
            Q454=sQuery(id+"F0.wireOp",EDGE,"7abc97d6-afd9-4ab4-834d-8372ee43eb68");
            var Q455;
            Q455=sQuery(id+"F0.wireOp",EDGE,"f435cfca-cf31-4e59-8c1f-7c4b925fd815");
            var Q456;
            Q456=sQuery(id+"F0.wireOp",EDGE,"e4418318-01eb-430f-98d1-0e757f5d104c");
            var Q457;
            Q457=sQuery(id+"F0.wireOp",EDGE,"9af42774-cfcb-402e-8bb4-c2d0581ec12a");
            var Q458;
            Q458=sQuery(id+"F0.wireOp",EDGE,"E1011");
            var Q459;
            Q459=sQuery(id+"F0.wireOp",EDGE,"09a223a5-4633-493b-a59c-263dee0a1aa9");
            var Q460;
            Q460=sQuery(id+"F0.wireOp",EDGE,"2479478a-da84-4838-844a-079949297298");
            var Q461;
            Q461=sQuery(id+"F0.wireOp",EDGE,"7efebebf-a1da-4aae-af74-b82fd2d2953f");
            var Q462;
            Q462=sQuery(id+"F0.wireOp",EDGE,"b7e441af-f540-47f9-8dca-2c452251cdcb");
            var Q463;
            Q463=sQuery(id+"F0.wireOp",EDGE,"6b096960-5ff1-4e29-99f8-b9d8a9366f81");
            var Q464;
            Q464=sQuery(id+"F0.wireOp",EDGE,"e05d5cc1-1232-46ee-88b3-890b53c53c4a");
            var Q465;
            Q465=sQuery(id+"F0.wireOp",EDGE,"E896");
            var Q466;
            Q466=sQuery(id+"F0.wireOp",EDGE,"b105fd50-2016-4939-8c22-a1aa931629f0");
            var Q467;
            Q467=sQuery(id+"F0.wireOp",EDGE,"c581d4a2-dcf7-4fb2-9cd4-4807128d9b45");
            var Q468;
            Q468=sQuery(id+"F0.wireOp",EDGE,"2b871284-a070-4284-be5d-6eb2a2715021");
            var Q469;
            Q469=sQuery(id+"F0.wireOp",EDGE,"8465a1d2-1c81-410c-98b1-5e66c4747f40");
            var Q470;
            Q470=sQuery(id+"F0.wireOp",EDGE,"51303a86-5447-4b0e-aff4-e5f6b5ea0327");
            var Q471;
            Q471=sQuery(id+"F0.wireOp",EDGE,"bf501977-9729-4758-8af2-76bf67a0fabc");
            var Q472;
            Q472=sQuery(id+"F0.wireOp",EDGE,"E898");
            var Q473;
            Q473=sQuery(id+"F0.wireOp",EDGE,"e9f0beda-055a-4d5c-87c1-949b464e1855");
            var Q474;
            Q474=sQuery(id+"F0.wireOp",EDGE,"828457b8-24cb-42db-9c51-800d6db92909");
            var Q475;
            Q475=sQuery(id+"F0.wireOp",EDGE,"2e0d8273-81fc-4f72-b0f3-8daf22550274");
            var Q476;
            Q476=sQuery(id+"F0.wireOp",EDGE,"d7487c61-654a-4ef3-953a-2680dd1fb559");
            var Q477;
            Q477=sQuery(id+"F0.wireOp",EDGE,"6825f87d-77aa-4121-b49d-a064865198ab");
            var Q478;
            Q478=sQuery(id+"F0.wireOp",EDGE,"ff19a59d-0b08-46ac-94c9-a86ca510f83f");
            var Q479;
            Q479=sQuery(id+"F0.wireOp",EDGE,"E929");
            var Q480;
            Q480=sQuery(id+"F0.wireOp",EDGE,"fd0326dd-568e-4723-830e-b9212018742b");
            var Q481;
            Q481=sQuery(id+"F0.wireOp",EDGE,"3dea49d8-f5aa-4034-b916-9c9fa873e314");
            var Q482;
            Q482=sQuery(id+"F0.wireOp",EDGE,"7a7bf2c0-c343-4467-a23d-57d6c53baf9f");
            var Q483;
            Q483=sQuery(id+"F0.wireOp",EDGE,"c5df3c47-90a9-4e6d-b239-5975d8290d28");
            var Q484;
            Q484=sQuery(id+"F0.wireOp",EDGE,"E990");
            var Q485;
            Q485=sQuery(id+"F0.wireOp",EDGE,"76e0016f-fb3d-498e-a623-4e76cf710045");
            var Q486;
            Q486=sQuery(id+"F0.wireOp",EDGE,"a9d63bf8-2bdc-4b50-8864-1a49c3b61afb");
            var Q487;
            Q487=sQuery(id+"F0.wireOp",EDGE,"E996");
            var Q488;
            Q488=sQuery(id+"F0.wireOp",EDGE,"60bf6f6e-3b62-4edc-bb09-c51b1c2ff835");
            var Q489;
            Q489=sQuery(id+"F0.wireOp",EDGE,"2bee0e97-ceb5-410a-85a7-0fc6854225cf");
            var Q490;
            Q490=sQuery(id+"F0.wireOp",EDGE,"e1ef0c3a-dca7-4e92-b7cd-acff2b52feb4");
            var Q491;
            Q491=sQuery(id+"F0.wireOp",EDGE,"980f7fed-a50b-4e67-8c0c-8745dbfa9a5d");
            var Q492;
            Q492=sQuery(id+"F0.wireOp",EDGE,"203c9b9c-fb45-4296-bd5a-be519bbd3228");
            var Q493;
            Q493=sQuery(id+"F0.wireOp",EDGE,"5259ce18-0b1a-4ec3-bf07-914564c1a3f5");
            var Q494;
            Q494=sQuery(id+"F0.wireOp",EDGE,"3118706d-1e47-476d-b6a5-7393a50af668");
            var Q495;
            Q495=sQuery(id+"F0.wireOp",EDGE,"dd267f34-46b2-4058-913f-2b822de52076");
            var Q496;
            Q496=sQuery(id+"F0.wireOp",EDGE,"2824aa6b-456d-4543-b18a-818bd8823873");
            var Q497;
            Q497=sQuery(id+"F0.wireOp",EDGE,"904985df-6eca-4101-ae62-bd93f6a8fe37");
            var Q498;
            Q498=sQuery(id+"F0.wireOp",EDGE,"8259fe79-1fe7-4242-926b-9f2b6477bd51");
            var Q499;
            Q499=sQuery(id+"F0.wireOp",EDGE,"4b59ea09-b12b-4d2b-b2c6-63f1ad0777d8");
            var Q500;
            Q500=sQuery(id+"F0.wireOp",EDGE,"E910");
            var Q501;
            Q501=sQuery(id+"F0.wireOp",EDGE,"7c40316a-7472-4062-b2ee-550bdde0893f");
            var Q502;
            Q502=sQuery(id+"F0.wireOp",EDGE,"142925ff-f166-49ae-88e3-e020eb0b4309");
            var Q503;
            Q503=sQuery(id+"F0.wireOp",EDGE,"c1ea459c-3bc3-4184-9705-c36a47e096ce");
            var Q504;
            Q504=sQuery(id+"F0.wireOp",EDGE,"e873705b-affc-4d2d-b929-194993f265ca");
            var Q505;
            Q505=sQuery(id+"F0.wireOp",EDGE,"390d4829-1acf-47e7-9232-39c035a6fafd");
            var Q506;
            Q506=sQuery(id+"F0.wireOp",EDGE,"32fe8947-d7f4-4a0d-b4ce-eaee9533c170");
            var Q507;
            Q507=sQuery(id+"F0.wireOp",EDGE,"9b5f61d8-7636-43bd-b426-2898c4dcd077");
            var Q508;
            Q508=sQuery(id+"F0.wireOp",EDGE,"3dfc4098-3366-4e19-ab4f-73be5c954e8b");
            var Q509;
            Q509=sQuery(id+"F0.wireOp",EDGE,"74b22888-ff3c-4930-a957-bcdace39639c");
            var Q510;
            Q510=sQuery(id+"F0.wireOp",EDGE,"9ced5b8b-8811-4711-adcd-9f04695d6aed");
            var Q511;
            Q511=sQuery(id+"F0.wireOp",EDGE,"2fe543ee-8558-46a9-acd8-6118f65fe2fc");
            var Q512;
            Q512=sQuery(id+"F0.wireOp",EDGE,"be848d55-30a1-4e0f-8d9d-ed919b6d0dc0");
            var Q513;
            Q513=sQuery(id+"F0.wireOp",EDGE,"c47f56a4-a907-4588-968d-0000e786967a");
            var Q514;
            Q514=sQuery(id+"F0.wireOp",EDGE,"bb1eab34-1c6b-400e-b9b9-a6ee53b61011");
            var Q515;
            Q515=sQuery(id+"F0.wireOp",EDGE,"30423f99-4825-4a0b-83db-2b0e8aed8b15");
            var Q516;
            Q516=sQuery(id+"F0.wireOp",EDGE,"ea843acf-3952-4d17-968f-18de3df30b27");
            var Q517;
            Q517=sQuery(id+"F0.wireOp",EDGE,"45a0b8bc-94a2-4fca-9d62-12421b70a076");
            var Q518;
            Q518=sQuery(id+"F0.wireOp",EDGE,"23afc704-1b98-4b9b-ab16-23fd8038e32c");
            var Q519;
            Q519=sQuery(id+"F0.wireOp",EDGE,"1a5350ce-675d-40a3-9769-ff05d86d51ae");
            var Q520;
            Q520=sQuery(id+"F0.wireOp",EDGE,"9d9b7622-16d4-45a2-ae40-f113cb7f3c2d");
            var Q521;
            Q521=sQuery(id+"F0.wireOp",EDGE,"1e393b8a-6e36-4e42-8cbe-ae5e1ec57be1");
            var Q522;
            Q522=sQuery(id+"F0.wireOp",EDGE,"f9e22850-cec8-46e1-abb8-c86683553ede");
            var Q523;
            Q523=sQuery(id+"F0.wireOp",EDGE,"faeba22f-dcf6-4559-ba73-911cfb7d3897");
            var Q524;
            Q524=sQuery(id+"F0.wireOp",EDGE,"aaf7d139-f0fd-4339-9928-b454845de16e");
            var Q525;
            Q525=sQuery(id+"F0.wireOp",EDGE,"6256bf15-eb71-441a-9870-c6b32a01288d");
            var Q526;
            Q526=sQuery(id+"F0.wireOp",EDGE,"ad5bb771-e828-4b3e-af76-f8a6327b8f86");
            var Q527;
            Q527=sQuery(id+"F0.wireOp",EDGE,"3508dda7-5464-4e1a-8ae8-8f63d447ffb6");
            var Q528;
            Q528=sQuery(id+"F0.wireOp",EDGE,"3d043524-cf2d-4c1a-a3a4-0282f72d0127");
            var Q529;
            Q529=sQuery(id+"F0.wireOp",EDGE,"4a6fc7f8-9287-48b5-8b2e-cff1def414aa");
            var Q530;
            Q530=sQuery(id+"F0.wireOp",EDGE,"30b7d2c9-a3c1-4ada-931e-289e06e3faa3");
            var Q531;
            Q531=sQuery(id+"F0.wireOp",EDGE,"216235d5-c404-4d47-a80a-a29f500b2eb4");
            var Q532;
            Q532=sQuery(id+"F0.wireOp",EDGE,"35178881-f403-405d-b679-f2186ab3e5a5");
            var Q533;
            Q533=sQuery(id+"F0.wireOp",EDGE,"1c738439-f851-49e8-a5d5-596ffa55766a");
            var Q534;
            Q534=sQuery(id+"F0.wireOp",EDGE,"c8e3ff84-d87c-4e7b-a9eb-6dccf92b7c5f");
            var Q535;
            Q535=sQuery(id+"F0.wireOp",EDGE,"99c5797b-fda6-4118-972f-b170f9e1a903");
            var Q536;
            Q536=sQuery(id+"F0.wireOp",EDGE,"d5fefb1d-2308-4c30-a2df-ddf66d34e0dd");
            var Q537;
            Q537=sQuery(id+"F0.wireOp",EDGE,"f98baf39-a972-40b3-824f-76d43d1f0077");
            extrude(context, id + "F1", {"entities" : qUnion([Q0]), "surfaceEntities" : qUnion([Q1, Q2, Q3, Q4, Q5, Q6, Q7, Q8, Q9, Q10, Q11, Q12, Q13, Q14, Q15, Q16, Q17, Q18, Q19, Q20, Q21, Q22, Q23, Q24, Q25, Q26, Q27, Q28, Q29, Q30, Q31, Q32, Q33, Q34, Q35, Q36, Q37, Q38, Q39, Q40, Q41, Q42, Q43, Q44, Q45, Q46, Q47, Q48, Q49, Q50, Q51, Q52, Q53, Q54, Q55, Q56, Q57, Q58, Q59, Q60, Q61, Q62, Q63, Q64, Q65, Q66, Q67, Q68, Q69, Q70, Q71, Q72, Q73, Q74, Q75, Q76, Q77, Q78, Q79, Q80, Q81, Q82, Q83, Q84, Q85, Q86, Q87, Q88, Q89, Q90, Q91, Q92, Q93, Q94, Q95, Q96, Q97, Q98, Q99, Q100, Q101, Q102, Q103, Q104, Q105, Q106, Q107, Q108, Q109, Q110, Q111, Q112, Q113, Q114, Q115, Q116, Q117, Q118, Q119, Q120, Q121, Q122, Q123, Q124, Q125, Q126, Q127, Q128, Q129, Q130, Q131, Q132, Q133, Q134, Q135, Q136, Q137, Q138, Q139, Q140, Q141, Q142, Q143, Q144, Q145, Q146, Q147, Q148, Q149, Q150, Q151, Q152, Q153, Q154, Q155, Q156, Q157, Q158, Q159, Q160, Q161, Q162, Q163, Q164, Q165, Q166, Q167, Q168, Q169, Q170, Q171, Q172, Q173, Q174, Q175, Q176, Q177, Q178, Q179, Q180, Q181, Q182, Q183, Q184, Q185, Q186, Q187, Q188, Q189, Q190, Q191, Q192, Q193, Q194, Q195, Q196, Q197, Q198, Q199, Q200, Q201, Q202, Q203, Q204, Q205, Q206, Q207, Q208, Q209, Q210, Q211, Q212, Q213, Q214, Q215, Q216, Q217, Q218, Q219, Q220, Q221, Q222, Q223, Q224, Q225, Q226, Q227, Q228, Q229, Q230, Q231, Q232, Q233, Q234, Q235, Q236, Q237, Q238, Q239, Q240, Q241, Q242, Q243, Q244, Q245, Q246, Q247, Q248, Q249, Q250, Q251, Q252, Q253, Q254, Q255, Q256, Q257, Q258, Q259, Q260, Q261, Q262, Q263, Q264, Q265, Q266, Q267, Q268, Q269, Q270, Q271, Q272, Q273, Q274, Q275, Q276, Q277, Q278, Q279, Q280, Q281, Q282, Q283, Q284, Q285, Q286, Q287, Q288, Q289, Q290, Q291, Q292, Q293, Q294, Q295, Q296, Q297, Q298, Q299, Q300, Q301, Q302, Q303, Q304, Q305, Q306, Q307, Q308, Q309, Q310, Q311, Q312, Q313, Q314, Q315, Q316, Q317, Q318, Q319, Q320, Q321, Q322, Q323, Q324, Q325, Q326, Q327, Q328, Q329, Q330, Q331, Q332, Q333, Q334, Q335, Q336, Q337, Q338, Q339, Q340, Q341, Q342, Q343, Q344, Q345, Q346, Q347, Q348, Q349, Q350, Q351, Q352, Q353, Q354, Q355, Q356, Q357, Q358, Q359, Q360, Q361, Q362, Q363, Q364, Q365, Q366, Q367, Q368, Q369, Q370, Q371, Q372, Q373, Q374, Q375, Q376, Q377, Q378, Q379, Q380, Q381, Q382, Q383, Q384, Q385, Q386, Q387, Q388, Q389, Q390, Q391, Q392, Q393, Q394, Q395, Q396, Q397, Q398, Q399, Q400, Q401, Q402, Q403, Q404, Q405, Q406, Q407, Q408, Q409, Q410, Q411, Q412, Q413, Q414, Q415, Q416, Q417, Q418, Q419, Q420, Q421, Q422, Q423, Q424, Q425, Q426, Q427, Q428, Q429, Q430, Q431, Q432, Q433, Q434, Q435, Q436, Q437, Q438, Q439, Q440, Q441, Q442, Q443, Q444, Q445, Q446, Q447, Q448, Q449, Q450, Q451, Q452, Q453, Q454, Q455, Q456, Q457, Q458, Q459, Q460, Q461, Q462, Q463, Q464, Q465, Q466, Q467, Q468, Q469, Q470, Q471, Q472, Q473, Q474, Q475, Q476, Q477, Q478, Q479, Q480, Q481, Q482, Q483, Q484, Q485, Q486, Q487, Q488, Q489, Q490, Q491, Q492, Q493, Q494, Q495, Q496, Q497, Q498, Q499, Q500, Q501, Q502, Q503, Q504, Q505, Q506, Q507, Q508, Q509, Q510, Q511, Q512, Q513, Q514, Q515, Q516, Q517, Q518, Q519, Q520, Q521, Q522, Q523, Q524, Q525, Q526, Q527, Q528, Q529, Q530, Q531, Q532, Q533, Q534, Q535, Q536, Q537]), "depth" : 6 * mm});
        }
        {
            var Q0;
            Q0=makeQuery(id+"F0.imprint","IMPRINT",FACE,{"disambiguationData":[TD([[makeQuery(id+"F0.imprint","IMPRINT",EDGE,{"derivedFrom":sQuery(id+"F0.wireOp",EDGE,"E8")}),-1.0]])]});
            extrude(context, id + "F2", {"entities" : qUnion([Q0]), "depth" : 6 * mm});
        }
        {
            var Q0;
            Q0=makeQuery(id+"F0.imprint","IMPRINT",FACE,{"disambiguationData":[TD([[makeQuery(id+"F0.imprint","IMPRINT",EDGE,{"derivedFrom":sQuery(id+"F0.wireOp",EDGE,"E136")}),1.0]])]});
            extrude(context, id + "F3", {"entities" : qUnion([Q0]), "depth" : 6 * mm});
        }
        {
            var Q0;
            Q0=makeQuery(id+"F0.imprint","IMPRINT",FACE,{"disambiguationData":[TD([[makeQuery(id+"F0.imprint","IMPRINT",EDGE,{"derivedFrom":sQuery(id+"F0.wireOp",EDGE,"E131")}),1.0]])]});
            extrude(context, id + "F4", {"entities" : qUnion([Q0]), "depth" : 6 * mm});
        }
        {
            var Q0;
            Q0=makeQuery(id+"F1.opExtrude","CAP_EDGE",EDGE,{"disambiguationData":[OSD([sQuery(id+"F0.wireOp",EDGE,"E837")])],"isStart":false});
            cPoint(context, id + "F5", {"entities" : qUnion([Q0]), "parameter" : 0.5});
        }
        {
            var Q0;
            Q0=makeQuery(id+"F1.opExtrude","CAP_EDGE",EDGE,{"disambiguationData":[OSD([sQuery(id+"F0.wireOp",EDGE,"E837")])],"isStart":true});
            cPoint(context, id + "F6", {"entities" : qUnion([Q0]), "parameter" : 0.5});
        }
        {
            var Q0;
            Q0=makeQuery(id+"F1.opExtrude","CAP_EDGE",EDGE,{"disambiguationData":[OSD([sQuery(id+"F0.wireOp",EDGE,"E805")])],"isStart":true});
            cPoint(context, id + "F7", {"entities" : qUnion([Q0]), "parameter" : 0.5});
        }
        {
            var Q0;
            Q0=qCreatedBy(id+"F5",VERTEX);
            var Q1;
            Q1=qCreatedBy(id+"F6",VERTEX);
            var Q2;
            Q2=qCreatedBy(id+"F7",VERTEX);
            cPlane(context, id + "F8", {"entities" : qUnion([Q0, Q1, Q2]), "cplaneType" : CPlaneType.THREE_POINT, "offset" : 25 * mm, "width" : 150 * mm, "height" : 150 * mm});
        }
        {
            var Q0;
            Q0=qCreatedBy(id+"F8.planeOp",FACE);
            var sketch = newSketch(context, id + "F9", { "sketchPlane" : qUnion([Q0])});
            skCircle(sketch, "E1247", {"center": v(225.54, 11.6) * mm, "radius": 7.5 * mm});
            skSolve(sketch);
        }
        {
            var Q0;
            Q0=makeQuery(id+"F1.opExtrude","CAP_EDGE",EDGE,{"disambiguationData":[OSD([sQuery(id+"F0.wireOp",EDGE,"E877")])],"isStart":true});
            cPoint(context, id + "F10", {"entities" : qUnion([Q0]), "parameter" : 0.5});
        }
        {
            var Q0;
            Q0=makeQuery(id+"F1.opExtrude","CAP_EDGE",EDGE,{"disambiguationData":[OSD([sQuery(id+"F0.wireOp",EDGE,"E877")])],"isStart":false});
            cPoint(context, id + "F11", {"entities" : qUnion([Q0]), "parameter" : 0.5});
        }
        {
            var Q0;
            Q0=makeQuery(id+"F1.opExtrude","CAP_EDGE",EDGE,{"disambiguationData":[OSD([sQuery(id+"F0.wireOp",EDGE,"E1033")])],"isStart":true});
            cPoint(context, id + "F12", {"entities" : qUnion([Q0]), "parameter" : 0.5});
        }
        {
            var Q0;
            Q0=qCreatedBy(id+"F10",VERTEX);
            var Q1;
            Q1=qCreatedBy(id+"F11",VERTEX);
            var Q2;
            Q2=qCreatedBy(id+"F12",VERTEX);
            cPlane(context, id + "F13", {"entities" : qUnion([Q0, Q1, Q2]), "cplaneType" : CPlaneType.THREE_POINT, "offset" : 25 * mm, "width" : 150 * mm, "height" : 150 * mm});
        }
        {
            var Q0;
            Q0=qCreatedBy(id+"F13.planeOp",FACE);
            var sketch = newSketch(context, id + "F14", { "sketchPlane" : qUnion([Q0])});
            skCircle(sketch, "E1248", {"center": v(-225.54, 11.6) * mm, "radius": 7.5 * mm});
            skPoint(sketch, "E1248.first.point", {"position": v(-230.54, 6) * mm});
            skPoint(sketch, "E1248.second.point", {"position": v(-220.54, 6) * mm});
            skPoint(sketch, "E1248.third.point", {"position": v(-218.32, 13.61) * mm});
            skSolve(sketch);
        }
        {
            var Q0;
            Q0=makeQuery(id+"F1.opExtrude","CAP_EDGE",EDGE,{"disambiguationData":[OSD([sQuery(id+"F0.wireOp",EDGE,"E965")])],"isStart":true});
            cPoint(context, id + "F15", {"entities" : qUnion([Q0]), "parameter" : 0.5});
        }
        {
            var Q0;
            Q0=makeQuery(id+"F1.opExtrude","CAP_EDGE",EDGE,{"disambiguationData":[OSD([sQuery(id+"F0.wireOp",EDGE,"E965")])],"isStart":false});
            cPoint(context, id + "F16", {"entities" : qUnion([Q0]), "parameter" : 0.5});
        }
        {
            var Q0;
            Q0=makeQuery(id+"F1.opExtrude","CAP_EDGE",EDGE,{"disambiguationData":[OSD([sQuery(id+"F0.wireOp",EDGE,"E914")])],"isStart":true});
            cPoint(context, id + "F17", {"entities" : qUnion([Q0]), "parameter" : 0.5});
        }
        {
            var Q0;
            Q0=qCreatedBy(id+"F15",VERTEX);
            var Q1;
            Q1=qCreatedBy(id+"F16",VERTEX);
            var Q2;
            Q2=qCreatedBy(id+"F17",VERTEX);
            cPlane(context, id + "F18", {"entities" : qUnion([Q0, Q1, Q2]), "cplaneType" : CPlaneType.THREE_POINT, "offset" : 25 * mm, "width" : 150 * mm, "height" : 150 * mm});
        }
        {
            var Q0;
            Q0=qCreatedBy(id+"F18.planeOp",FACE);
            var sketch = newSketch(context, id + "F19", { "sketchPlane" : qUnion([Q0])});
            skCircle(sketch, "E1249", {"center": v(-55.54, 11.6) * mm, "radius": 7.5 * mm});
            skSolve(sketch);
        }
        {
            var Q0;
            Q0=makeQuery(id+"F1.opExtrude","CAP_FACE",FACE,{"disambiguationData":[OSD([sQuery(id+"F0.wireOp",EDGE,"E0"),sQuery(id+"F0.wireOp",EDGE,"E1"),sQuery(id+"F0.wireOp",EDGE,"E3"),sQuery(id+"F0.wireOp",EDGE,"E5"),sQuery(id+"F0.wireOp",EDGE,"E6"),sQuery(id+"F0.wireOp",EDGE,"E7"),sQuery(id+"F0.wireOp",EDGE,"E803"),sQuery(id+"F0.wireOp",EDGE,"E804"),sQuery(id+"F0.wireOp",EDGE,"E805"),sQuery(id+"F0.wireOp",EDGE,"E806"),sQuery(id+"F0.wireOp",EDGE,"E807"),sQuery(id+"F0.wireOp",EDGE,"E808"),sQuery(id+"F0.wireOp",EDGE,"E809"),sQuery(id+"F0.wireOp",EDGE,"E810"),sQuery(id+"F0.wireOp",EDGE,"E811"),sQuery(id+"F0.wireOp",EDGE,"E812"),sQuery(id+"F0.wireOp",EDGE,"E813"),sQuery(id+"F0.wireOp",EDGE,"E814"),sQuery(id+"F0.wireOp",EDGE,"E815"),sQuery(id+"F0.wireOp",EDGE,"E816"),sQuery(id+"F0.wireOp",EDGE,"E817"),sQuery(id+"F0.wireOp",EDGE,"E818"),sQuery(id+"F0.wireOp",EDGE,"E819"),sQuery(id+"F0.wireOp",EDGE,"E820"),sQuery(id+"F0.wireOp",EDGE,"E821"),sQuery(id+"F0.wireOp",EDGE,"E822"),sQuery(id+"F0.wireOp",EDGE,"E823"),sQuery(id+"F0.wireOp",EDGE,"E824"),sQuery(id+"F0.wireOp",EDGE,"E825"),sQuery(id+"F0.wireOp",EDGE,"E826"),sQuery(id+"F0.wireOp",EDGE,"E827"),sQuery(id+"F0.wireOp",EDGE,"E828"),sQuery(id+"F0.wireOp",EDGE,"E829"),sQuery(id+"F0.wireOp",EDGE,"E830"),sQuery(id+"F0.wireOp",EDGE,"E831"),sQuery(id+"F0.wireOp",EDGE,"E832"),sQuery(id+"F0.wireOp",EDGE,"E833"),sQuery(id+"F0.wireOp",EDGE,"E834"),sQuery(id+"F0.wireOp",EDGE,"E835"),sQuery(id+"F0.wireOp",EDGE,"E836"),sQuery(id+"F0.wireOp",EDGE,"E837"),sQuery(id+"F0.wireOp",EDGE,"E838"),sQuery(id+"F0.wireOp",EDGE,"E839"),sQuery(id+"F0.wireOp",EDGE,"E840"),sQuery(id+"F0.wireOp",EDGE,"E841"),sQuery(id+"F0.wireOp",EDGE,"E842"),sQuery(id+"F0.wireOp",EDGE,"E843"),sQuery(id+"F0.wireOp",EDGE,"E844"),sQuery(id+"F0.wireOp",EDGE,"E845"),sQuery(id+"F0.wireOp",EDGE,"E846"),sQuery(id+"F0.wireOp",EDGE,"E847"),sQuery(id+"F0.wireOp",EDGE,"E848"),sQuery(id+"F0.wireOp",EDGE,"E849"),sQuery(id+"F0.wireOp",EDGE,"E850"),sQuery(id+"F0.wireOp",EDGE,"E851"),sQuery(id+"F0.wireOp",EDGE,"E852"),sQuery(id+"F0.wireOp",EDGE,"E853"),sQuery(id+"F0.wireOp",EDGE,"E854"),sQuery(id+"F0.wireOp",EDGE,"E855"),sQuery(id+"F0.wireOp",EDGE,"E856"),sQuery(id+"F0.wireOp",EDGE,"E857"),sQuery(id+"F0.wireOp",EDGE,"E858"),sQuery(id+"F0.wireOp",EDGE,"E859"),sQuery(id+"F0.wireOp",EDGE,"E860"),sQuery(id+"F0.wireOp",EDGE,"E861"),sQuery(id+"F0.wireOp",EDGE,"E862"),sQuery(id+"F0.wireOp",EDGE,"E863"),sQuery(id+"F0.wireOp",EDGE,"E864"),sQuery(id+"F0.wireOp",EDGE,"E865"),sQuery(id+"F0.wireOp",EDGE,"E866"),sQuery(id+"F0.wireOp",EDGE,"E867"),sQuery(id+"F0.wireOp",EDGE,"E868"),sQuery(id+"F0.wireOp",EDGE,"E869"),sQuery(id+"F0.wireOp",EDGE,"E870"),sQuery(id+"F0.wireOp",EDGE,"E871"),sQuery(id+"F0.wireOp",EDGE,"E872"),sQuery(id+"F0.wireOp",EDGE,"E873"),sQuery(id+"F0.wireOp",EDGE,"E874"),sQuery(id+"F0.wireOp",EDGE,"E875"),sQuery(id+"F0.wireOp",EDGE,"E876"),sQuery(id+"F0.wireOp",EDGE,"E877"),sQuery(id+"F0.wireOp",EDGE,"E878"),sQuery(id+"F0.wireOp",EDGE,"E879"),sQuery(id+"F0.wireOp",EDGE,"E880"),sQuery(id+"F0.wireOp",EDGE,"E881"),sQuery(id+"F0.wireOp",EDGE,"E882"),sQuery(id+"F0.wireOp",EDGE,"E883"),sQuery(id+"F0.wireOp",EDGE,"E884"),sQuery(id+"F0.wireOp",EDGE,"E885"),sQuery(id+"F0.wireOp",EDGE,"E886"),sQuery(id+"F0.wireOp",EDGE,"E887"),sQuery(id+"F0.wireOp",EDGE,"E888"),sQuery(id+"F0.wireOp",EDGE,"E889"),sQuery(id+"F0.wireOp",EDGE,"E890"),sQuery(id+"F0.wireOp",EDGE,"E891"),sQuery(id+"F0.wireOp",EDGE,"E892"),sQuery(id+"F0.wireOp",EDGE,"E893"),sQuery(id+"F0.wireOp",EDGE,"E894"),sQuery(id+"F0.wireOp",EDGE,"E895"),sQuery(id+"F0.wireOp",EDGE,"E896"),sQuery(id+"F0.wireOp",EDGE,"E897"),sQuery(id+"F0.wireOp",EDGE,"E898"),sQuery(id+"F0.wireOp",EDGE,"E899"),sQuery(id+"F0.wireOp",EDGE,"E900"),sQuery(id+"F0.wireOp",EDGE,"E901"),sQuery(id+"F0.wireOp",EDGE,"E902"),sQuery(id+"F0.wireOp",EDGE,"E903"),sQuery(id+"F0.wireOp",EDGE,"E904"),sQuery(id+"F0.wireOp",EDGE,"E905"),sQuery(id+"F0.wireOp",EDGE,"E906"),sQuery(id+"F0.wireOp",EDGE,"E907"),sQuery(id+"F0.wireOp",EDGE,"E908"),sQuery(id+"F0.wireOp",EDGE,"E909"),sQuery(id+"F0.wireOp",EDGE,"E910"),sQuery(id+"F0.wireOp",EDGE,"E911"),sQuery(id+"F0.wireOp",EDGE,"E912"),sQuery(id+"F0.wireOp",EDGE,"E913"),sQuery(id+"F0.wireOp",EDGE,"E914"),sQuery(id+"F0.wireOp",EDGE,"E915"),sQuery(id+"F0.wireOp",EDGE,"E916"),sQuery(id+"F0.wireOp",EDGE,"E917"),sQuery(id+"F0.wireOp",EDGE,"E918"),sQuery(id+"F0.wireOp",EDGE,"E919"),sQuery(id+"F0.wireOp",EDGE,"E920"),sQuery(id+"F0.wireOp",EDGE,"E921"),sQuery(id+"F0.wireOp",EDGE,"E922"),sQuery(id+"F0.wireOp",EDGE,"E923"),sQuery(id+"F0.wireOp",EDGE,"E924"),sQuery(id+"F0.wireOp",EDGE,"E925"),sQuery(id+"F0.wireOp",EDGE,"E926"),sQuery(id+"F0.wireOp",EDGE,"E927"),sQuery(id+"F0.wireOp",EDGE,"E928"),sQuery(id+"F0.wireOp",EDGE,"E929"),sQuery(id+"F0.wireOp",EDGE,"E930"),sQuery(id+"F0.wireOp",EDGE,"E931"),sQuery(id+"F0.wireOp",EDGE,"E932"),sQuery(id+"F0.wireOp",EDGE,"E933"),sQuery(id+"F0.wireOp",EDGE,"E934"),sQuery(id+"F0.wireOp",EDGE,"E935"),sQuery(id+"F0.wireOp",EDGE,"E936"),sQuery(id+"F0.wireOp",EDGE,"E938"),sQuery(id+"F0.wireOp",EDGE,"E939"),sQuery(id+"F0.wireOp",EDGE,"E940"),sQuery(id+"F0.wireOp",EDGE,"E942"),sQuery(id+"F0.wireOp",EDGE,"E943"),sQuery(id+"F0.wireOp",EDGE,"E944"),sQuery(id+"F0.wireOp",EDGE,"E945"),sQuery(id+"F0.wireOp",EDGE,"E946"),sQuery(id+"F0.wireOp",EDGE,"E947"),sQuery(id+"F0.wireOp",EDGE,"E948"),sQuery(id+"F0.wireOp",EDGE,"E949"),sQuery(id+"F0.wireOp",EDGE,"E950"),sQuery(id+"F0.wireOp",EDGE,"E951"),sQuery(id+"F0.wireOp",EDGE,"E952"),sQuery(id+"F0.wireOp",EDGE,"E953"),sQuery(id+"F0.wireOp",EDGE,"E955"),sQuery(id+"F0.wireOp",EDGE,"E956"),sQuery(id+"F0.wireOp",EDGE,"E957"),sQuery(id+"F0.wireOp",EDGE,"E959"),sQuery(id+"F0.wireOp",EDGE,"E960"),sQuery(id+"F0.wireOp",EDGE,"E961"),sQuery(id+"F0.wireOp",EDGE,"E962"),sQuery(id+"F0.wireOp",EDGE,"E963"),sQuery(id+"F0.wireOp",EDGE,"E964"),sQuery(id+"F0.wireOp",EDGE,"E965"),sQuery(id+"F0.wireOp",EDGE,"E966"),sQuery(id+"F0.wireOp",EDGE,"E967"),sQuery(id+"F0.wireOp",EDGE,"E968"),sQuery(id+"F0.wireOp",EDGE,"E969"),sQuery(id+"F0.wireOp",EDGE,"E970"),sQuery(id+"F0.wireOp",EDGE,"E971"),sQuery(id+"F0.wireOp",EDGE,"E972"),sQuery(id+"F0.wireOp",EDGE,"E973"),sQuery(id+"F0.wireOp",EDGE,"E974"),sQuery(id+"F0.wireOp",EDGE,"E975"),sQuery(id+"F0.wireOp",EDGE,"E976"),sQuery(id+"F0.wireOp",EDGE,"E977"),sQuery(id+"F0.wireOp",EDGE,"E978"),sQuery(id+"F0.wireOp",EDGE,"E979"),sQuery(id+"F0.wireOp",EDGE,"E980"),sQuery(id+"F0.wireOp",EDGE,"E981"),sQuery(id+"F0.wireOp",EDGE,"E982"),sQuery(id+"F0.wireOp",EDGE,"E983"),sQuery(id+"F0.wireOp",EDGE,"E984"),sQuery(id+"F0.wireOp",EDGE,"E985"),sQuery(id+"F0.wireOp",EDGE,"E986"),sQuery(id+"F0.wireOp",EDGE,"E987"),sQuery(id+"F0.wireOp",EDGE,"E988"),sQuery(id+"F0.wireOp",EDGE,"E989"),sQuery(id+"F0.wireOp",EDGE,"E990"),sQuery(id+"F0.wireOp",EDGE,"E991"),sQuery(id+"F0.wireOp",EDGE,"E992"),sQuery(id+"F0.wireOp",EDGE,"E993"),sQuery(id+"F0.wireOp",EDGE,"E994"),sQuery(id+"F0.wireOp",EDGE,"E995"),sQuery(id+"F0.wireOp",EDGE,"E996"),sQuery(id+"F0.wireOp",EDGE,"E997"),sQuery(id+"F0.wireOp",EDGE,"E998"),sQuery(id+"F0.wireOp",EDGE,"E999"),sQuery(id+"F0.wireOp",EDGE,"E1000"),sQuery(id+"F0.wireOp",EDGE,"E1001"),sQuery(id+"F0.wireOp",EDGE,"E1002"),sQuery(id+"F0.wireOp",EDGE,"E1003"),sQuery(id+"F0.wireOp",EDGE,"E1004"),sQuery(id+"F0.wireOp",EDGE,"E1005"),sQuery(id+"F0.wireOp",EDGE,"E1006"),sQuery(id+"F0.wireOp",EDGE,"E1007"),sQuery(id+"F0.wireOp",EDGE,"E1008"),sQuery(id+"F0.wireOp",EDGE,"E1009"),sQuery(id+"F0.wireOp",EDGE,"E1010"),sQuery(id+"F0.wireOp",EDGE,"E1011"),sQuery(id+"F0.wireOp",EDGE,"E1012"),sQuery(id+"F0.wireOp",EDGE,"E1013"),sQuery(id+"F0.wireOp",EDGE,"E1014"),sQuery(id+"F0.wireOp",EDGE,"E1015"),sQuery(id+"F0.wireOp",EDGE,"E1016"),sQuery(id+"F0.wireOp",EDGE,"E1017"),sQuery(id+"F0.wireOp",EDGE,"E1018"),sQuery(id+"F0.wireOp",EDGE,"E1019"),sQuery(id+"F0.wireOp",EDGE,"E1020"),sQuery(id+"F0.wireOp",EDGE,"E1021"),sQuery(id+"F0.wireOp",EDGE,"E1022"),sQuery(id+"F0.wireOp",EDGE,"E1023"),sQuery(id+"F0.wireOp",EDGE,"E1024"),sQuery(id+"F0.wireOp",EDGE,"E1025"),sQuery(id+"F0.wireOp",EDGE,"E1026"),sQuery(id+"F0.wireOp",EDGE,"E1027"),sQuery(id+"F0.wireOp",EDGE,"E1028"),sQuery(id+"F0.wireOp",EDGE,"E1029"),sQuery(id+"F0.wireOp",EDGE,"E1030"),sQuery(id+"F0.wireOp",EDGE,"E1031"),sQuery(id+"F0.wireOp",EDGE,"E1032"),sQuery(id+"F0.wireOp",EDGE,"E1033"),sQuery(id+"F0.wireOp",EDGE,"E1034"),sQuery(id+"F0.wireOp",EDGE,"E1220"),sQuery(id+"F0.wireOp",EDGE,"E1221"),sQuery(id+"F0.wireOp",EDGE,"E1222"),sQuery(id+"F0.wireOp",EDGE,"E1223"),sQuery(id+"F0.wireOp",EDGE,"E1224"),sQuery(id+"F0.wireOp",EDGE,"E1225"),sQuery(id+"F0.wireOp",EDGE,"E1226"),sQuery(id+"F0.wireOp",EDGE,"E1227"),sQuery(id+"F0.wireOp",EDGE,"E1228"),sQuery(id+"F0.wireOp",EDGE,"E1229"),sQuery(id+"F0.wireOp",EDGE,"E1230")])],"isStart":false});
            var sketch = newSketch(context, id + "F20", { "sketchPlane" : qUnion([Q0])});
            skCircle(sketch, "E1250", {"center": v(-245.05, 134.48) * mm, "radius": 1.6 * mm});
            skCircle(sketch, "E1251", {"center": v(-36.03, 134.48) * mm, "radius": 1.6 * mm});
            skCircle(sketch, "E1252", {"center": v(-36.03, -74.54) * mm, "radius": 1.6 * mm});
            skCircle(sketch, "E1253", {"center": v(-245.05, -74.52) * mm, "radius": 1.6 * mm});
            skLineSegment(sketch, "E1254.bottom", {"start": v(-247.35, 136.7) * mm, "end": v(-33.35, 136.7) * mm});
            skLineSegment(sketch, "E1254.top", {"start": v(-247.35, -77.3) * mm, "end": v(-33.35, -77.3) * mm});
            skLineSegment(sketch, "E1254.left", {"start": v(-247.35, 136.7) * mm, "end": v(-247.35, -77.3) * mm});
            skLineSegment(sketch, "E1254.right", {"start": v(-33.35, 136.7) * mm, "end": v(-33.35, -77.3) * mm});
            skSolve(sketch);
        }
        {
            var Q0;
            {var subQ5=makeQuery(id+"F1.opExtrude","CAP_EDGE",EDGE,{"disambiguationData":[OSD([sQuery(id+"F0.wireOp",EDGE,"E853")])],"isStart":false});Q0=makeQuery(id+"F20.imprint","IMPRINT",FACE,{"disambiguationData":[TD([[makeQuery(id+"F20.imprint","IMPRINT",EDGE,{"derivedFrom":subQ5}),1.0]])]});}
            var Q1;
            {var subQ5=makeQuery(id+"F1.opExtrude","CAP_EDGE",EDGE,{"disambiguationData":[OSD([sQuery(id+"F0.wireOp",EDGE,"E803")])],"isStart":false});Q1=makeQuery(id+"F20.imprint","IMPRINT",FACE,{"disambiguationData":[TD([[makeQuery(id+"F20.imprint","IMPRINT",EDGE,{"derivedFrom":subQ5}),-1.0]])]});}
            var Q2;
            {var subQ5=makeQuery(id+"F1.opExtrude","CAP_EDGE",EDGE,{"disambiguationData":[OSD([sQuery(id+"F0.wireOp",EDGE,"E917")])],"isStart":false});Q2=makeQuery(id+"F20.imprint","IMPRINT",FACE,{"disambiguationData":[TD([[makeQuery(id+"F20.imprint","IMPRINT",EDGE,{"derivedFrom":subQ5}),-1.0]])]});}
            var Q3;
            Q3=makeQuery(id+"F20.imprint","IMPRINT",FACE,{"disambiguationData":[TD([[makeQuery(id+"F20.imprint","IMPRINT",EDGE,{"derivedFrom":makeQuery(id+"F1.opExtrude","CAP_EDGE",EDGE,{"disambiguationData":[OSD([sQuery(id+"F0.wireOp",EDGE,"E3")])],"isStart":false})}),1.0]])]});
            var Q4;
            Q4=makeQuery(id+"F20.imprint","IMPRINT",FACE,{"disambiguationData":[TD([[makeQuery(id+"F20.imprint","IMPRINT",EDGE,{"derivedFrom":makeQuery(id+"F1.opExtrude","CAP_EDGE",EDGE,{"disambiguationData":[OSD([sQuery(id+"F0.wireOp",EDGE,"E804")])],"isStart":false})}),1.0]])]});
            var Q5;
            Q5=makeQuery(id+"F20.imprint","IMPRINT",FACE,{"disambiguationData":[TD([[makeQuery(id+"F20.imprint","IMPRINT",EDGE,{"derivedFrom":makeQuery(id+"F1.opExtrude","CAP_EDGE",EDGE,{"disambiguationData":[OSD([sQuery(id+"F0.wireOp",EDGE,"E835")])],"isStart":false})}),-1.0]])]});
            var Q6;
            Q6=makeQuery(id+"F20.imprint","IMPRINT",FACE,{"disambiguationData":[TD([[makeQuery(id+"F20.imprint","IMPRINT",EDGE,{"derivedFrom":makeQuery(id+"F1.opExtrude","CAP_EDGE",EDGE,{"disambiguationData":[OSD([sQuery(id+"F0.wireOp",EDGE,"E818")])],"isStart":false})}),-1.0]])]});
            var Q7;
            Q7=makeQuery(id+"F20.imprint","IMPRINT",FACE,{"disambiguationData":[TD([[makeQuery(id+"F20.imprint","IMPRINT",EDGE,{"derivedFrom":makeQuery(id+"F1.opExtrude","CAP_EDGE",EDGE,{"disambiguationData":[OSD([sQuery(id+"F0.wireOp",EDGE,"E945")])],"isStart":false})}),-1.0]])]});
            var Q8;
            Q8=makeQuery(id+"F20.imprint","IMPRINT",FACE,{"disambiguationData":[TD([[makeQuery(id+"F20.imprint","IMPRINT",EDGE,{"derivedFrom":makeQuery(id+"F1.opExtrude","CAP_EDGE",EDGE,{"disambiguationData":[OSD([sQuery(id+"F0.wireOp",EDGE,"E3")])],"isStart":false})}),-1.0]])]});
            var Q9;
            Q9=makeQuery(id+"F20.imprint","IMPRINT",FACE,{"disambiguationData":[TD([[makeQuery(id+"F20.imprint","IMPRINT",EDGE,{"derivedFrom":makeQuery(id+"F1.opExtrude","CAP_EDGE",EDGE,{"disambiguationData":[OSD([sQuery(id+"F0.wireOp",EDGE,"E822")])],"isStart":false})}),1.0]])]});
            var Q10;
            Q10=makeQuery(id+"F20.imprint","IMPRINT",FACE,{"disambiguationData":[TD([[makeQuery(id+"F20.imprint","IMPRINT",EDGE,{"derivedFrom":makeQuery(id+"F1.opExtrude","CAP_EDGE",EDGE,{"disambiguationData":[OSD([sQuery(id+"F0.wireOp",EDGE,"E806")])],"isStart":false})}),1.0]])]});
            var Q11;
            Q11=makeQuery(id+"F20.imprint","IMPRINT",FACE,{"disambiguationData":[TD([[makeQuery(id+"F20.imprint","IMPRINT",EDGE,{"derivedFrom":makeQuery(id+"F1.opExtrude","CAP_EDGE",EDGE,{"disambiguationData":[OSD([sQuery(id+"F0.wireOp",EDGE,"E805")])],"isStart":false})}),-1.0]])]});
            var Q12;
            Q12=makeQuery(id+"F20.imprint","IMPRINT",FACE,{"disambiguationData":[TD([[makeQuery(id+"F20.imprint","IMPRINT",EDGE,{"derivedFrom":makeQuery(id+"F1.opExtrude","CAP_EDGE",EDGE,{"disambiguationData":[OSD([sQuery(id+"F0.wireOp",EDGE,"E1225")])],"isStart":false})}),1.0]])]});
            var Q13;
            Q13=makeQuery(id+"F20.imprint","IMPRINT",FACE,{"disambiguationData":[TD([[makeQuery(id+"F20.imprint","IMPRINT",EDGE,{"derivedFrom":makeQuery(id+"F1.opExtrude","CAP_EDGE",EDGE,{"disambiguationData":[OSD([sQuery(id+"F0.wireOp",EDGE,"E1224")])],"isStart":false})}),1.0]])]});
            var Q14;
            Q14=makeQuery(id+"F20.imprint","IMPRINT",FACE,{"disambiguationData":[TD([[makeQuery(id+"F20.imprint","IMPRINT",EDGE,{"derivedFrom":makeQuery(id+"F1.opExtrude","CAP_EDGE",EDGE,{"disambiguationData":[OSD([sQuery(id+"F0.wireOp",EDGE,"E1228")])],"isStart":false})}),1.0]])]});
            var Q15;
            Q15=makeQuery(id+"F20.imprint","IMPRINT",FACE,{"disambiguationData":[TD([[makeQuery(id+"F20.imprint","IMPRINT",EDGE,{"derivedFrom":makeQuery(id+"F1.opExtrude","CAP_EDGE",EDGE,{"disambiguationData":[OSD([sQuery(id+"F0.wireOp",EDGE,"E1226")])],"isStart":false})}),1.0]])]});
            var Q16;
            Q16=makeQuery(id+"F20.imprint","IMPRINT",FACE,{"disambiguationData":[TD([[makeQuery(id+"F20.imprint","IMPRINT",EDGE,{"derivedFrom":makeQuery(id+"F1.opExtrude","CAP_EDGE",EDGE,{"disambiguationData":[OSD([sQuery(id+"F0.wireOp",EDGE,"E1227")])],"isStart":false})}),1.0]])]});
            var Q17;
            Q17=makeQuery(id+"F20.imprint","IMPRINT",FACE,{"disambiguationData":[TD([[makeQuery(id+"F20.imprint","IMPRINT",EDGE,{"derivedFrom":makeQuery(id+"F1.opExtrude","CAP_EDGE",EDGE,{"disambiguationData":[OSD([sQuery(id+"F0.wireOp",EDGE,"E1223")])],"isStart":false})}),1.0]])]});
            var Q18;
            Q18=makeQuery(id+"F20.imprint","IMPRINT",FACE,{"disambiguationData":[TD([[makeQuery(id+"F20.imprint","IMPRINT",EDGE,{"derivedFrom":makeQuery(id+"F1.opExtrude","CAP_EDGE",EDGE,{"disambiguationData":[OSD([sQuery(id+"F0.wireOp",EDGE,"E1222")])],"isStart":false})}),1.0]])]});
            extrude(context, id + "F21", {"entities" : qUnion([Q0, Q1, Q2, Q3, Q4, Q5, Q6, Q7, Q8, Q9, Q10, Q11, Q12, Q13, Q14, Q15, Q16, Q17, Q18]), "depth" : 2.5 * mm});
        }
    });
